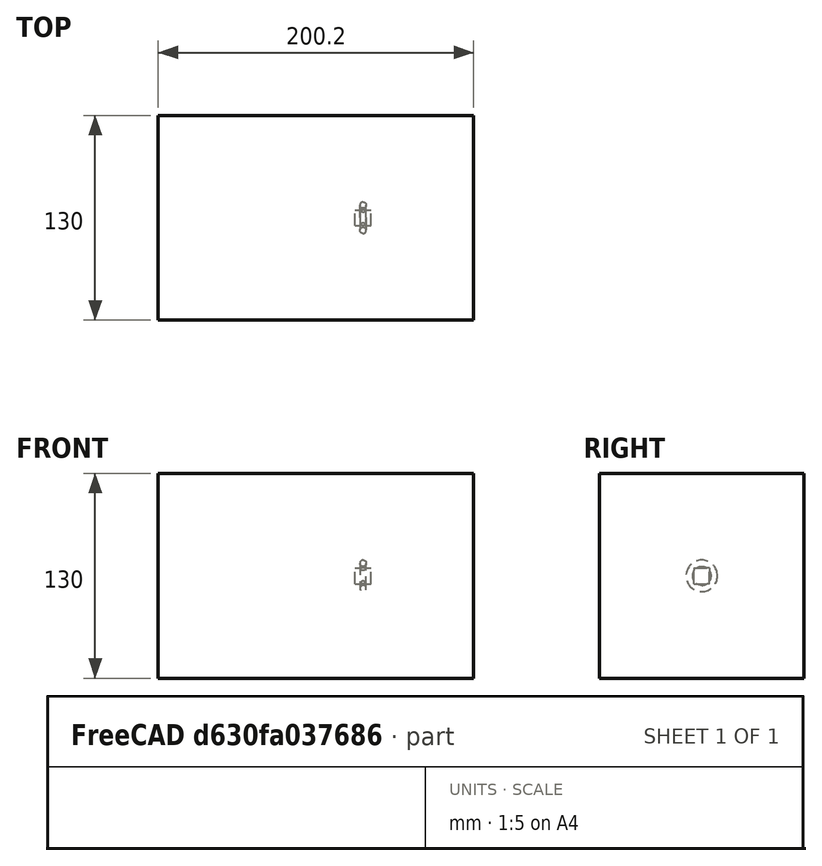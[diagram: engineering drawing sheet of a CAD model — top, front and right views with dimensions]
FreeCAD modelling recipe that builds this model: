
FCSTD DOCUMENT  (FreeCAD 1.0R39109 (Git))
Label: polarArray-7-array-rotated-translated
License: All rights reserved
objects: App::DocumentObjectGroupPython×1251, Part::FeaturePython×4, App::Part×2, Part::MultiFuse×1
note: 4 computed .brp shape members not serialized (recipe doc carries the construction recipe); baked Part::Feature solids carry a one-line shape summary decoded from their .brp

FEATURE [App::DocumentObjectGroupPython] HALFPI  # scripted group (container) (typed FeaturePython)
  name = HALFPI
  value = pi/2.
FEATURE [App::DocumentObjectGroupPython] PI  # scripted group (container) (typed FeaturePython)
  name = PI
  value = 1.*pi
FEATURE [App::DocumentObjectGroupPython] TWOPI  # scripted group (container) (typed FeaturePython)
  name = TWOPI
  value = 2.*pi
FEATURE [App::DocumentObjectGroupPython] Constants  # scripted group (container) (typed FeaturePython)
  Group = -> [HALFPI,PI,TWOPI]
FEATURE [App::DocumentObjectGroupPython] Variables  # scripted group (container) (typed FeaturePython)
FEATURE [App::DocumentObjectGroupPython] Quantities  # scripted group (container) (typed FeaturePython)
FEATURE [App::DocumentObjectGroupPython] Isotopes  # scripted group (container) (typed FeaturePython)
FEATURE [App::DocumentObjectGroupPython] Elements  # scripted group (container) (typed FeaturePython)
FEATURE [App::DocumentObjectGroupPython] Matrix  # scripted group (container) (typed FeaturePython)
FEATURE [App::DocumentObjectGroupPython] Surfaces  # scripted group (container) (typed FeaturePython)
FEATURE [App::DocumentObjectGroupPython] Opticals  # scripted group (container) (typed FeaturePython)
  Group = -> [Matrix,Surfaces]
FEATURE [App::DocumentObjectGroupPython] G4Isotopes  # scripted group (container) (typed FeaturePython)
FEATURE [App::DocumentObjectGroupPython] H_element  # scripted group (container) (typed FeaturePython)
  Z = 1
  atom_value = 1.008
  formula = H
  name = H_element
FEATURE [App::DocumentObjectGroupPython] He_element  # scripted group (container) (typed FeaturePython)
  Z = 2
  atom_value = 4.0026
  formula = He
  name = He_element
FEATURE [App::DocumentObjectGroupPython] Li_element  # scripted group (container) (typed FeaturePython)
  Z = 3
  atom_value = 6.94
  formula = Li
  name = Li_element
FEATURE [App::DocumentObjectGroupPython] Be_element  # scripted group (container) (typed FeaturePython)
  Z = 4
  atom_value = 9.01218
  formula = Be
  name = Be_element
FEATURE [App::DocumentObjectGroupPython] B_element  # scripted group (container) (typed FeaturePython)
  Z = 5
  atom_value = 10.81
  formula = B
  name = B_element
FEATURE [App::DocumentObjectGroupPython] C_element  # scripted group (container) (typed FeaturePython)
  Z = 6
  atom_value = 12.011
  formula = C
  name = C_element
FEATURE [App::DocumentObjectGroupPython] N_element  # scripted group (container) (typed FeaturePython)
  Z = 7
  atom_value = 14.007
  formula = N
  name = N_element
FEATURE [App::DocumentObjectGroupPython] O_element  # scripted group (container) (typed FeaturePython)
  Z = 8
  atom_value = 15.999
  formula = O
  name = O_element
FEATURE [App::DocumentObjectGroupPython] F_element  # scripted group (container) (typed FeaturePython)
  Z = 9
  atom_value = 18.9984
  formula = F
  name = F_element
FEATURE [App::DocumentObjectGroupPython] Ne_element  # scripted group (container) (typed FeaturePython)
  Z = 10
  atom_value = 20.1797
  formula = Ne
  name = Ne_element
FEATURE [App::DocumentObjectGroupPython] Na_element  # scripted group (container) (typed FeaturePython)
  Z = 11
  atom_value = 22.9898
  formula = Na
  name = Na_element
FEATURE [App::DocumentObjectGroupPython] Mg_element  # scripted group (container) (typed FeaturePython)
  Z = 12
  atom_value = 24.305
  formula = Mg
  name = Mg_element
FEATURE [App::DocumentObjectGroupPython] Al_element  # scripted group (container) (typed FeaturePython)
  Z = 13
  atom_value = 26.9815
  formula = Al
  name = Al_element
FEATURE [App::DocumentObjectGroupPython] Si_element  # scripted group (container) (typed FeaturePython)
  Z = 14
  atom_value = 28.085
  formula = Si
  name = Si_element
FEATURE [App::DocumentObjectGroupPython] P_element  # scripted group (container) (typed FeaturePython)
  Z = 15
  atom_value = 30.9738
  formula = P
  name = P_element
FEATURE [App::DocumentObjectGroupPython] S_element  # scripted group (container) (typed FeaturePython)
  Z = 16
  atom_value = 32.06
  formula = S
  name = S_element
FEATURE [App::DocumentObjectGroupPython] Cl_element  # scripted group (container) (typed FeaturePython)
  Z = 17
  atom_value = 35.45
  formula = Cl
  name = Cl_element
FEATURE [App::DocumentObjectGroupPython] Ar_element  # scripted group (container) (typed FeaturePython)
  Z = 18
  atom_value = 39.95
  formula = Ar
  name = Ar_element
FEATURE [App::DocumentObjectGroupPython] K_element  # scripted group (container) (typed FeaturePython)
  Z = 19
  atom_value = 39.0983
  formula = K
  name = K_element
FEATURE [App::DocumentObjectGroupPython] Ca_element  # scripted group (container) (typed FeaturePython)
  Z = 20
  atom_value = 40.078
  formula = Ca
  name = Ca_element
FEATURE [App::DocumentObjectGroupPython] Sc_element  # scripted group (container) (typed FeaturePython)
  Z = 21
  atom_value = 44.9559
  formula = Sc
  name = Sc_element
FEATURE [App::DocumentObjectGroupPython] Ti_element  # scripted group (container) (typed FeaturePython)
  Z = 22
  atom_value = 47.867
  formula = Ti
  name = Ti_element
FEATURE [App::DocumentObjectGroupPython] V_element  # scripted group (container) (typed FeaturePython)
  Z = 23
  atom_value = 50.9415
  formula = V
  name = V_element
FEATURE [App::DocumentObjectGroupPython] Cr_element  # scripted group (container) (typed FeaturePython)
  Z = 24
  atom_value = 51.9961
  formula = Cr
  name = Cr_element
FEATURE [App::DocumentObjectGroupPython] Mn_element  # scripted group (container) (typed FeaturePython)
  Z = 25
  atom_value = 54.938
  formula = Mn
  name = Mn_element
FEATURE [App::DocumentObjectGroupPython] Fe_element  # scripted group (container) (typed FeaturePython)
  Z = 26
  atom_value = 55.845
  formula = Fe
  name = Fe_element
FEATURE [App::DocumentObjectGroupPython] Co_element  # scripted group (container) (typed FeaturePython)
  Z = 27
  atom_value = 58.9332
  formula = Co
  name = Co_element
FEATURE [App::DocumentObjectGroupPython] Ni_element  # scripted group (container) (typed FeaturePython)
  Z = 28
  atom_value = 58.6934
  formula = Ni
  name = Ni_element
FEATURE [App::DocumentObjectGroupPython] Cu_element  # scripted group (container) (typed FeaturePython)
  Z = 29
  atom_value = 63.546
  formula = Cu
  name = Cu_element
FEATURE [App::DocumentObjectGroupPython] Zn_element  # scripted group (container) (typed FeaturePython)
  Z = 30
  atom_value = 65.38
  formula = Zn
  name = Zn_element
FEATURE [App::DocumentObjectGroupPython] Ga_element  # scripted group (container) (typed FeaturePython)
  Z = 31
  atom_value = 69.723
  formula = Ga
  name = Ga_element
FEATURE [App::DocumentObjectGroupPython] Ge_element  # scripted group (container) (typed FeaturePython)
  Z = 32
  atom_value = 72.63
  formula = Ge
  name = Ge_element
FEATURE [App::DocumentObjectGroupPython] As_element  # scripted group (container) (typed FeaturePython)
  Z = 33
  atom_value = 74.9216
  formula = As
  name = As_element
FEATURE [App::DocumentObjectGroupPython] Se_element  # scripted group (container) (typed FeaturePython)
  Z = 34
  atom_value = 78.971
  formula = Se
  name = Se_element
FEATURE [App::DocumentObjectGroupPython] Br_element  # scripted group (container) (typed FeaturePython)
  Z = 35
  atom_value = 79.904
  formula = Br
  name = Br_element
FEATURE [App::DocumentObjectGroupPython] Kr_element  # scripted group (container) (typed FeaturePython)
  Z = 36
  atom_value = 83.798
  formula = Kr
  name = Kr_element
FEATURE [App::DocumentObjectGroupPython] Rb_element  # scripted group (container) (typed FeaturePython)
  Z = 37
  atom_value = 85.4678
  formula = Rb
  name = Rb_element
FEATURE [App::DocumentObjectGroupPython] Sr_element  # scripted group (container) (typed FeaturePython)
  Z = 38
  atom_value = 87.62
  formula = Sr
  name = Sr_element
FEATURE [App::DocumentObjectGroupPython] Y_element  # scripted group (container) (typed FeaturePython)
  Z = 39
  atom_value = 88.9058
  formula = Y
  name = Y_element
FEATURE [App::DocumentObjectGroupPython] Zr_element  # scripted group (container) (typed FeaturePython)
  Z = 40
  atom_value = 91.224
  formula = Zr
  name = Zr_element
FEATURE [App::DocumentObjectGroupPython] Nb_element  # scripted group (container) (typed FeaturePython)
  Z = 41
  atom_value = 92.9064
  formula = Nb
  name = Nb_element
FEATURE [App::DocumentObjectGroupPython] Mo_element  # scripted group (container) (typed FeaturePython)
  Z = 42
  atom_value = 95.95
  formula = Mo
  name = Mo_element
FEATURE [App::DocumentObjectGroupPython] Tc_element  # scripted group (container) (typed FeaturePython)
  Z = 43
  atom_value = 97
  formula = Tc
  name = Tc_element
FEATURE [App::DocumentObjectGroupPython] Ru_element  # scripted group (container) (typed FeaturePython)
  Z = 44
  atom_value = 101.07
  formula = Ru
  name = Ru_element
FEATURE [App::DocumentObjectGroupPython] Rh_element  # scripted group (container) (typed FeaturePython)
  Z = 45
  atom_value = 102.905
  formula = Rh
  name = Rh_element
FEATURE [App::DocumentObjectGroupPython] Pd_element  # scripted group (container) (typed FeaturePython)
  Z = 46
  atom_value = 106.42
  formula = Pd
  name = Pd_element
FEATURE [App::DocumentObjectGroupPython] Ag_element  # scripted group (container) (typed FeaturePython)
  Z = 47
  atom_value = 107.868
  formula = Ag
  name = Ag_element
FEATURE [App::DocumentObjectGroupPython] Cd_element  # scripted group (container) (typed FeaturePython)
  Z = 48
  atom_value = 112.414
  formula = Cd
  name = Cd_element
FEATURE [App::DocumentObjectGroupPython] In_element  # scripted group (container) (typed FeaturePython)
  Z = 49
  atom_value = 114.818
  formula = In
  name = In_element
FEATURE [App::DocumentObjectGroupPython] Sn_element  # scripted group (container) (typed FeaturePython)
  Z = 50
  atom_value = 118.71
  formula = Sn
  name = Sn_element
FEATURE [App::DocumentObjectGroupPython] Sb_element  # scripted group (container) (typed FeaturePython)
  Z = 51
  atom_value = 121.76
  formula = Sb
  name = Sb_element
FEATURE [App::DocumentObjectGroupPython] Te_element  # scripted group (container) (typed FeaturePython)
  Z = 52
  atom_value = 127.6
  formula = Te
  name = Te_element
FEATURE [App::DocumentObjectGroupPython] I_element  # scripted group (container) (typed FeaturePython)
  Z = 53
  atom_value = 126.904
  formula = I
  name = I_element
FEATURE [App::DocumentObjectGroupPython] Xe_element  # scripted group (container) (typed FeaturePython)
  Z = 54
  atom_value = 131.293
  formula = Xe
  name = Xe_element
FEATURE [App::DocumentObjectGroupPython] Cs_element  # scripted group (container) (typed FeaturePython)
  Z = 55
  atom_value = 132.905
  formula = Cs
  name = Cs_element
FEATURE [App::DocumentObjectGroupPython] Ba_element  # scripted group (container) (typed FeaturePython)
  Z = 56
  atom_value = 137.327
  formula = Ba
  name = Ba_element
FEATURE [App::DocumentObjectGroupPython] La_element  # scripted group (container) (typed FeaturePython)
  Z = 57
  atom_value = 138.905
  formula = La
  name = La_element
FEATURE [App::DocumentObjectGroupPython] Ce_element  # scripted group (container) (typed FeaturePython)
  Z = 58
  atom_value = 140.116
  formula = Ce
  name = Ce_element
FEATURE [App::DocumentObjectGroupPython] Pr_element  # scripted group (container) (typed FeaturePython)
  Z = 59
  atom_value = 140.908
  formula = Pr
  name = Pr_element
FEATURE [App::DocumentObjectGroupPython] Nd_element  # scripted group (container) (typed FeaturePython)
  Z = 60
  atom_value = 144.242
  formula = Nd
  name = Nd_element
FEATURE [App::DocumentObjectGroupPython] Pm_element  # scripted group (container) (typed FeaturePython)
  Z = 61
  atom_value = 145
  formula = Pm
  name = Pm_element
FEATURE [App::DocumentObjectGroupPython] Sm_element  # scripted group (container) (typed FeaturePython)
  Z = 62
  atom_value = 150.36
  formula = Sm
  name = Sm_element
FEATURE [App::DocumentObjectGroupPython] Eu_element  # scripted group (container) (typed FeaturePython)
  Z = 63
  atom_value = 151.964
  formula = Eu
  name = Eu_element
FEATURE [App::DocumentObjectGroupPython] Gd_element  # scripted group (container) (typed FeaturePython)
  Z = 64
  atom_value = 157.25
  formula = Gd
  name = Gd_element
FEATURE [App::DocumentObjectGroupPython] Tb_element  # scripted group (container) (typed FeaturePython)
  Z = 65
  atom_value = 158.925
  formula = Tb
  name = Tb_element
FEATURE [App::DocumentObjectGroupPython] Dy_element  # scripted group (container) (typed FeaturePython)
  Z = 66
  atom_value = 162.5
  formula = Dy
  name = Dy_element
FEATURE [App::DocumentObjectGroupPython] Ho_element  # scripted group (container) (typed FeaturePython)
  Z = 67
  atom_value = 164.93
  formula = Ho
  name = Ho_element
FEATURE [App::DocumentObjectGroupPython] Er_element  # scripted group (container) (typed FeaturePython)
  Z = 68
  atom_value = 167.259
  formula = Er
  name = Er_element
FEATURE [App::DocumentObjectGroupPython] Tm_element  # scripted group (container) (typed FeaturePython)
  Z = 69
  atom_value = 168.934
  formula = Tm
  name = Tm_element
FEATURE [App::DocumentObjectGroupPython] Yb_element  # scripted group (container) (typed FeaturePython)
  Z = 70
  atom_value = 173.045
  formula = Yb
  name = Yb_element
FEATURE [App::DocumentObjectGroupPython] Lu_element  # scripted group (container) (typed FeaturePython)
  Z = 71
  atom_value = 174.967
  formula = Lu
  name = Lu_element
FEATURE [App::DocumentObjectGroupPython] Hf_element  # scripted group (container) (typed FeaturePython)
  Z = 72
  atom_value = 178.49
  formula = Hf
  name = Hf_element
FEATURE [App::DocumentObjectGroupPython] Ta_element  # scripted group (container) (typed FeaturePython)
  Z = 73
  atom_value = 180.948
  formula = Ta
  name = Ta_element
FEATURE [App::DocumentObjectGroupPython] W_element  # scripted group (container) (typed FeaturePython)
  Z = 74
  atom_value = 183.84
  formula = W
  name = W_element
FEATURE [App::DocumentObjectGroupPython] Re_element  # scripted group (container) (typed FeaturePython)
  Z = 75
  atom_value = 186.207
  formula = Re
  name = Re_element
FEATURE [App::DocumentObjectGroupPython] Os_element  # scripted group (container) (typed FeaturePython)
  Z = 76
  atom_value = 190.23
  formula = Os
  name = Os_element
FEATURE [App::DocumentObjectGroupPython] Ir_element  # scripted group (container) (typed FeaturePython)
  Z = 77
  atom_value = 192.217
  formula = Ir
  name = Ir_element
FEATURE [App::DocumentObjectGroupPython] Pt_element  # scripted group (container) (typed FeaturePython)
  Z = 78
  atom_value = 195.084
  formula = Pt
  name = Pt_element
FEATURE [App::DocumentObjectGroupPython] Au_element  # scripted group (container) (typed FeaturePython)
  Z = 79
  atom_value = 196.967
  formula = Au
  name = Au_element
FEATURE [App::DocumentObjectGroupPython] Hg_element  # scripted group (container) (typed FeaturePython)
  Z = 80
  atom_value = 200.592
  formula = Hg
  name = Hg_element
FEATURE [App::DocumentObjectGroupPython] Tl_element  # scripted group (container) (typed FeaturePython)
  Z = 81
  atom_value = 204.38
  formula = Tl
  name = Tl_element
FEATURE [App::DocumentObjectGroupPython] Pb_element  # scripted group (container) (typed FeaturePython)
  Z = 82
  atom_value = 207.2
  formula = Pb
  name = Pb_element
FEATURE [App::DocumentObjectGroupPython] Bi_element  # scripted group (container) (typed FeaturePython)
  Z = 83
  atom_value = 208.98
  formula = Bi
  name = Bi_element
FEATURE [App::DocumentObjectGroupPython] Po_element  # scripted group (container) (typed FeaturePython)
  Z = 84
  atom_value = 209
  formula = Po
  name = Po_element
FEATURE [App::DocumentObjectGroupPython] At_element  # scripted group (container) (typed FeaturePython)
  Z = 85
  atom_value = 210
  formula = At
  name = At_element
FEATURE [App::DocumentObjectGroupPython] Rn_element  # scripted group (container) (typed FeaturePython)
  Z = 86
  atom_value = 222
  formula = Rn
  name = Rn_element
FEATURE [App::DocumentObjectGroupPython] Fr_element  # scripted group (container) (typed FeaturePython)
  Z = 87
  atom_value = 223
  formula = Fr
  name = Fr_element
FEATURE [App::DocumentObjectGroupPython] Ra_element  # scripted group (container) (typed FeaturePython)
  Z = 88
  atom_value = 226
  formula = Ra
  name = Ra_element
FEATURE [App::DocumentObjectGroupPython] Ac_element  # scripted group (container) (typed FeaturePython)
  Z = 89
  atom_value = 227
  formula = Ac
  name = Ac_element
FEATURE [App::DocumentObjectGroupPython] Th_element  # scripted group (container) (typed FeaturePython)
  Z = 90
  atom_value = 232.038
  formula = Th
  name = Th_element
FEATURE [App::DocumentObjectGroupPython] Pa_element  # scripted group (container) (typed FeaturePython)
  Z = 91
  atom_value = 231.036
  formula = Pa
  name = Pa_element
FEATURE [App::DocumentObjectGroupPython] U_element  # scripted group (container) (typed FeaturePython)
  Z = 92
  atom_value = 238.029
  formula = U
  name = U_element
FEATURE [App::DocumentObjectGroupPython] Np_element  # scripted group (container) (typed FeaturePython)
  Z = 93
  atom_value = 237
  formula = Np
  name = Np_element
FEATURE [App::DocumentObjectGroupPython] Pu_element  # scripted group (container) (typed FeaturePython)
  Z = 94
  atom_value = 244
  formula = Pu
  name = Pu_element
FEATURE [App::DocumentObjectGroupPython] Am_element  # scripted group (container) (typed FeaturePython)
  Z = 95
  atom_value = 243
  formula = Am
  name = Am_element
FEATURE [App::DocumentObjectGroupPython] Cm_element  # scripted group (container) (typed FeaturePython)
  Z = 96
  atom_value = 247
  formula = Cm
  name = Cm_element
FEATURE [App::DocumentObjectGroupPython] Bk_element  # scripted group (container) (typed FeaturePython)
  Z = 97
  atom_value = 247
  formula = Bk
  name = Bk_element
FEATURE [App::DocumentObjectGroupPython] Cf_element  # scripted group (container) (typed FeaturePython)
  Z = 98
  atom_value = 251
  formula = Cf
  name = Cf_element
FEATURE [App::DocumentObjectGroupPython] G4Elements  # scripted group (container) (typed FeaturePython)
  Group = -> [H_element,He_element,Li_element,Be_element,B_element,C_element,N_element,O_element,F_element,Ne_element,Na_element,Mg_element,Al_element,Si_element,P_element,S_element,Cl_element,Ar_element,K_element,Ca_element,Sc_element,Ti_element,V_element,Cr_element,Mn_element,Fe_element,Co_element,Ni_element,Cu_element,Zn_element,Ga_element,Ge_element,As_element,Se_element,Br_element,Kr_element,Rb_element,+61 more]
FEATURE [App::DocumentObjectGroupPython] H_element001  label="H_element : 0.101"  # scripted group (container) (typed FeaturePython)
  n = 0.101327
FEATURE [App::DocumentObjectGroupPython] C_element001  label="C_element : 0.775"  # scripted group (container) (typed FeaturePython)
  n = 0.7755
FEATURE [App::DocumentObjectGroupPython] N_element001  label="N_element : 0.035"  # scripted group (container) (typed FeaturePython)
  n = 0.035057
FEATURE [App::DocumentObjectGroupPython] O_element001  label="O_element : 0.052"  # scripted group (container) (typed FeaturePython)
  n = 0.0523159
FEATURE [App::DocumentObjectGroupPython] F_element001  label="F_element : 0.017"  # scripted group (container) (typed FeaturePython)
  n = 0.017422
FEATURE [App::DocumentObjectGroupPython] Ca_element001  label="Ca_element : 0.018"  # scripted group (container) (typed FeaturePython)
  n = 0.018378
FEATURE [App::DocumentObjectGroupPython] G4_A_150_TISSUE  label="G4_A-150_TISSUE"  # scripted group (container) (typed FeaturePython)
  Dunit = g/cm3
  Dvalue = 1.127
  Group = -> [H_element001,C_element001,N_element001,O_element001,F_element001,Ca_element001]
  conduct = 2
  density = 1
  expand = 3
  formula = G4_A-150_TISSUE
  name = G4_A-150_TISSUE
  specific = 4
FEATURE [App::DocumentObjectGroupPython] C_element002  label="C_element : 3"  # scripted group (container) (typed FeaturePython)
  n = 3
  ref = C_element
FEATURE [App::DocumentObjectGroupPython] H_element002  label="H_element : 6"  # scripted group (container) (typed FeaturePython)
  n = 6
  ref = H_element
FEATURE [App::DocumentObjectGroupPython] O_element002  label="O_element : 1"  # scripted group (container) (typed FeaturePython)
  n = 1
  ref = O_element
FEATURE [App::DocumentObjectGroupPython] G4_ACETONE  # scripted group (container) (typed FeaturePython)
  Dunit = g/cm3
  Dvalue = 0.7899
  Group = -> [C_element002,H_element002,O_element002]
  conduct = 2
  density = 1
  expand = 3
  formula = G4_ACETONE
  name = G4_ACETONE
  specific = 4
FEATURE [App::DocumentObjectGroupPython] C_element003  label="C_element : 2"  # scripted group (container) (typed FeaturePython)
  n = 2
  ref = C_element
FEATURE [App::DocumentObjectGroupPython] H_element003  label="H_element : 2"  # scripted group (container) (typed FeaturePython)
  n = 2
  ref = H_element
FEATURE [App::DocumentObjectGroupPython] G4_ACETYLENE  # scripted group (container) (typed FeaturePython)
  Dunit = g/cm3
  Dvalue = 0.0010967
  Group = -> [C_element003,H_element003]
  conduct = 2
  density = 1
  expand = 3
  formula = G4_ACETYLENE
  name = G4_ACETYLENE
  specific = 4
FEATURE [App::DocumentObjectGroupPython] C_element004  label="C_element : 5"  # scripted group (container) (typed FeaturePython)
  n = 5
  ref = C_element
FEATURE [App::DocumentObjectGroupPython] H_element004  label="H_element : 5"  # scripted group (container) (typed FeaturePython)
  n = 5
  ref = H_element
FEATURE [App::DocumentObjectGroupPython] N_element002  label="N_element : 5"  # scripted group (container) (typed FeaturePython)
  n = 5
  ref = N_element
FEATURE [App::DocumentObjectGroupPython] G4_ADENINE  # scripted group (container) (typed FeaturePython)
  Dunit = g/cm3
  Dvalue = 1.6
  Group = -> [C_element004,H_element004,N_element002]
  conduct = 2
  density = 1
  expand = 3
  formula = G4_ADENINE
  name = G4_ADENINE
  specific = 4
FEATURE [App::DocumentObjectGroupPython] H_element005  label="H_element : 0.114"  # scripted group (container) (typed FeaturePython)
  n = 0.114
FEATURE [App::DocumentObjectGroupPython] C_element005  label="C_element : 0.598"  # scripted group (container) (typed FeaturePython)
  n = 0.598
FEATURE [App::DocumentObjectGroupPython] N_element003  label="N_element : 0.007"  # scripted group (container) (typed FeaturePython)
  n = 0.007
FEATURE [App::DocumentObjectGroupPython] O_element003  label="O_element : 0.278"  # scripted group (container) (typed FeaturePython)
  n = 0.278
FEATURE [App::DocumentObjectGroupPython] Na_element001  label="Na_element : 0.001"  # scripted group (container) (typed FeaturePython)
  n = 0.001
FEATURE [App::DocumentObjectGroupPython] S_element001  label="S_element : 0.001"  # scripted group (container) (typed FeaturePython)
  n = 0.001
FEATURE [App::DocumentObjectGroupPython] Cl_element001  label="Cl_element : 0.001"  # scripted group (container) (typed FeaturePython)
  n = 0.001
FEATURE [App::DocumentObjectGroupPython] G4_ADIPOSE_TISSUE_ICRP  # scripted group (container) (typed FeaturePython)
  Dunit = g/cm3
  Dvalue = 0.95
  Group = -> [H_element005,C_element005,N_element003,O_element003,Na_element001,S_element001,Cl_element001]
  conduct = 2
  density = 1
  expand = 3
  formula = G4_ADIPOSE_TISSUE_ICRP
  name = G4_ADIPOSE_TISSUE_ICRP
  specific = 4
FEATURE [App::DocumentObjectGroupPython] C_element006  label="C_element : 0.000"  # scripted group (container) (typed FeaturePython)
  n = 0.000124
FEATURE [App::DocumentObjectGroupPython] N_element004  label="N_element : 0.755"  # scripted group (container) (typed FeaturePython)
  n = 0.755268
FEATURE [App::DocumentObjectGroupPython] O_element004  label="O_element : 0.232"  # scripted group (container) (typed FeaturePython)
  n = 0.231781
FEATURE [App::DocumentObjectGroupPython] Ar_element001  label="Ar_element : 0.013"  # scripted group (container) (typed FeaturePython)
  n = 0.012827
FEATURE [App::DocumentObjectGroupPython] G4_AIR  # scripted group (container) (typed FeaturePython)
  Dunit = g/cm3
  Dvalue = 0.00120479
  Group = -> [C_element006,N_element004,O_element004,Ar_element001]
  conduct = 2
  density = 1
  expand = 3
  formula = G4_AIR
  name = G4_AIR
  specific = 4
FEATURE [App::DocumentObjectGroupPython] C_element007  label="C_element : 006"  # scripted group (container) (typed FeaturePython)
  n = 3
  ref = C_element
FEATURE [App::DocumentObjectGroupPython] H_element006  label="H_element : 7"  # scripted group (container) (typed FeaturePython)
  n = 7
  ref = H_element
FEATURE [App::DocumentObjectGroupPython] N_element005  label="N_element : 1"  # scripted group (container) (typed FeaturePython)
  n = 1
  ref = N_element
FEATURE [App::DocumentObjectGroupPython] O_element005  label="O_element : 2"  # scripted group (container) (typed FeaturePython)
  n = 2
  ref = O_element
FEATURE [App::DocumentObjectGroupPython] G4_ALANINE  # scripted group (container) (typed FeaturePython)
  Dunit = g/cm3
  Dvalue = 1.42
  Group = -> [C_element007,H_element006,N_element005,O_element005]
  conduct = 2
  density = 1
  expand = 3
  formula = G4_ALANINE
  name = G4_ALANINE
  specific = 4
FEATURE [App::DocumentObjectGroupPython] Al_element001  label="Al_element : 2"  # scripted group (container) (typed FeaturePython)
  n = 2
  ref = Al_element
FEATURE [App::DocumentObjectGroupPython] O_element006  label="O_element : 3"  # scripted group (container) (typed FeaturePython)
  n = 3
  ref = O_element
FEATURE [App::DocumentObjectGroupPython] G4_ALUMINUM_OXIDE  # scripted group (container) (typed FeaturePython)
  Dunit = g/cm3
  Dvalue = 3.97
  Group = -> [Al_element001,O_element006]
  conduct = 2
  density = 1
  expand = 3
  formula = G4_ALUMINUM_OXIDE
  name = G4_ALUMINUM_OXIDE
  specific = 4
FEATURE [App::DocumentObjectGroupPython] H_element007  label="H_element : 0.106"  # scripted group (container) (typed FeaturePython)
  n = 0.10593
FEATURE [App::DocumentObjectGroupPython] C_element008  label="C_element : 0.789"  # scripted group (container) (typed FeaturePython)
  n = 0.788974
FEATURE [App::DocumentObjectGroupPython] O_element007  label="O_element : 0.105"  # scripted group (container) (typed FeaturePython)
  n = 0.105096
FEATURE [App::DocumentObjectGroupPython] G4_AMBER  # scripted group (container) (typed FeaturePython)
  Dunit = g/cm3
  Dvalue = 1.1
  Group = -> [H_element007,C_element008,O_element007]
  conduct = 2
  density = 1
  expand = 3
  formula = G4_AMBER
  name = G4_AMBER
  specific = 4
FEATURE [App::DocumentObjectGroupPython] N_element006  label="N_element : 006"  # scripted group (container) (typed FeaturePython)
  n = 1
  ref = N_element
FEATURE [App::DocumentObjectGroupPython] H_element008  label="H_element : 3"  # scripted group (container) (typed FeaturePython)
  n = 3
  ref = H_element
FEATURE [App::DocumentObjectGroupPython] G4_AMMONIA  # scripted group (container) (typed FeaturePython)
  Dunit = g/cm3
  Dvalue = 0.000826019
  Group = -> [N_element006,H_element008]
  conduct = 2
  density = 1
  expand = 3
  formula = G4_AMMONIA
  name = G4_AMMONIA
  specific = 4
FEATURE [App::DocumentObjectGroupPython] C_element009  label="C_element : 6"  # scripted group (container) (typed FeaturePython)
  n = 6
  ref = C_element
FEATURE [App::DocumentObjectGroupPython] H_element009  label="H_element : 008"  # scripted group (container) (typed FeaturePython)
  n = 7
  ref = H_element
FEATURE [App::DocumentObjectGroupPython] N_element007  label="N_element : 007"  # scripted group (container) (typed FeaturePython)
  n = 1
  ref = N_element
FEATURE [App::DocumentObjectGroupPython] G4_ANILINE  # scripted group (container) (typed FeaturePython)
  Dunit = g/cm3
  Dvalue = 1.0235
  Group = -> [C_element009,H_element009,N_element007]
  conduct = 2
  density = 1
  expand = 3
  formula = G4_ANILINE
  name = G4_ANILINE
  specific = 4
FEATURE [App::DocumentObjectGroupPython] C_element010  label="C_element : 14"  # scripted group (container) (typed FeaturePython)
  n = 14
  ref = C_element
FEATURE [App::DocumentObjectGroupPython] H_element010  label="H_element : 10"  # scripted group (container) (typed FeaturePython)
  n = 10
  ref = H_element
FEATURE [App::DocumentObjectGroupPython] G4_ANTHRACENE  # scripted group (container) (typed FeaturePython)
  Dunit = g/cm3
  Dvalue = 1.283
  Group = -> [C_element010,H_element010]
  conduct = 2
  density = 1
  expand = 3
  formula = G4_ANTHRACENE
  name = G4_ANTHRACENE
  specific = 4
FEATURE [App::DocumentObjectGroupPython] H_element011  label="H_element : 0.065"  # scripted group (container) (typed FeaturePython)
  n = 0.0654709
FEATURE [App::DocumentObjectGroupPython] C_element011  label="C_element : 0.537"  # scripted group (container) (typed FeaturePython)
  n = 0.536944
FEATURE [App::DocumentObjectGroupPython] N_element008  label="N_element : 0.021"  # scripted group (container) (typed FeaturePython)
  n = 0.0215
FEATURE [App::DocumentObjectGroupPython] O_element008  label="O_element : 0.032"  # scripted group (container) (typed FeaturePython)
  n = 0.032085
FEATURE [App::DocumentObjectGroupPython] F_element002  label="F_element : 0.167"  # scripted group (container) (typed FeaturePython)
  n = 0.167411
FEATURE [App::DocumentObjectGroupPython] Ca_element002  label="Ca_element : 0.177"  # scripted group (container) (typed FeaturePython)
  n = 0.176589
FEATURE [App::DocumentObjectGroupPython] G4_B_100_BONE  label="G4_B-100_BONE"  # scripted group (container) (typed FeaturePython)
  Dunit = g/cm3
  Dvalue = 1.45
  Group = -> [H_element011,C_element011,N_element008,O_element008,F_element002,Ca_element002]
  conduct = 2
  density = 1
  expand = 3
  formula = G4_B-100_BONE
  name = G4_B-100_BONE
  specific = 4
FEATURE [App::DocumentObjectGroupPython] H_element012  label="H_element : 0.057"  # scripted group (container) (typed FeaturePython)
  n = 0.057441
FEATURE [App::DocumentObjectGroupPython] C_element012  label="C_element : 0.790"  # scripted group (container) (typed FeaturePython)
  n = 0.774591
FEATURE [App::DocumentObjectGroupPython] O_element009  label="O_element : 0.168"  # scripted group (container) (typed FeaturePython)
  n = 0.167968
FEATURE [App::DocumentObjectGroupPython] G4_BAKELITE  # scripted group (container) (typed FeaturePython)
  Dunit = g/cm3
  Dvalue = 1.25
  Group = -> [H_element012,C_element012,O_element009]
  conduct = 2
  density = 1
  expand = 3
  formula = G4_BAKELITE
  name = G4_BAKELITE
  specific = 4
FEATURE [App::DocumentObjectGroupPython] Ba_element001  label="Ba_element : 1"  # scripted group (container) (typed FeaturePython)
  n = 1
  ref = Ba_element
FEATURE [App::DocumentObjectGroupPython] F_element003  label="F_element : 2"  # scripted group (container) (typed FeaturePython)
  n = 2
  ref = F_element
FEATURE [App::DocumentObjectGroupPython] G4_BARIUM_FLUORIDE  # scripted group (container) (typed FeaturePython)
  Dunit = g/cm3
  Dvalue = 4.89
  Group = -> [Ba_element001,F_element003]
  conduct = 2
  density = 1
  expand = 3
  formula = G4_BARIUM_FLUORIDE
  name = G4_BARIUM_FLUORIDE
  specific = 4
FEATURE [App::DocumentObjectGroupPython] Ba_element002  label="Ba_element : 002"  # scripted group (container) (typed FeaturePython)
  n = 1
  ref = Ba_element
FEATURE [App::DocumentObjectGroupPython] S_element002  label="S_element : 1"  # scripted group (container) (typed FeaturePython)
  n = 1
  ref = S_element
FEATURE [App::DocumentObjectGroupPython] O_element010  label="O_element : 4"  # scripted group (container) (typed FeaturePython)
  n = 4
  ref = O_element
FEATURE [App::DocumentObjectGroupPython] G4_BARIUM_SULFATE  # scripted group (container) (typed FeaturePython)
  Dunit = g/cm3
  Dvalue = 4.5
  Group = -> [Ba_element002,S_element002,O_element010]
  conduct = 2
  density = 1
  expand = 3
  formula = G4_BARIUM_SULFATE
  name = G4_BARIUM_SULFATE
  specific = 4
FEATURE [App::DocumentObjectGroupPython] C_element013  label="C_element : 007"  # scripted group (container) (typed FeaturePython)
  n = 6
  ref = C_element
FEATURE [App::DocumentObjectGroupPython] H_element013  label="H_element : 009"  # scripted group (container) (typed FeaturePython)
  n = 6
  ref = H_element
FEATURE [App::DocumentObjectGroupPython] G4_BENZENE  # scripted group (container) (typed FeaturePython)
  Dunit = g/cm3
  Dvalue = 0.87865
  Group = -> [C_element013,H_element013]
  conduct = 2
  density = 1
  expand = 3
  formula = G4_BENZENE
  name = G4_BENZENE
  specific = 4
FEATURE [App::DocumentObjectGroupPython] Be_element001  label="Be_element : 1"  # scripted group (container) (typed FeaturePython)
  n = 1
  ref = Be_element
FEATURE [App::DocumentObjectGroupPython] O_element011  label="O_element : 005"  # scripted group (container) (typed FeaturePython)
  n = 1
  ref = O_element
FEATURE [App::DocumentObjectGroupPython] G4_BERYLLIUM_OXIDE  # scripted group (container) (typed FeaturePython)
  Dunit = g/cm3
  Dvalue = 3.01
  Group = -> [Be_element001,O_element011]
  conduct = 2
  density = 1
  expand = 3
  formula = G4_BERYLLIUM_OXIDE
  name = G4_BERYLLIUM_OXIDE
  specific = 4
FEATURE [App::DocumentObjectGroupPython] Bi_element001  label="Bi_element : 4"  # scripted group (container) (typed FeaturePython)
  n = 4
  ref = Bi_element
FEATURE [App::DocumentObjectGroupPython] Ge_element001  label="Ge_element : 3"  # scripted group (container) (typed FeaturePython)
  n = 3
  ref = Ge_element
FEATURE [App::DocumentObjectGroupPython] O_element012  label="O_element : 12"  # scripted group (container) (typed FeaturePython)
  n = 12
  ref = O_element
FEATURE [App::DocumentObjectGroupPython] G4_BGO  # scripted group (container) (typed FeaturePython)
  Dunit = g/cm3
  Dvalue = 7.13
  Group = -> [Bi_element001,Ge_element001,O_element012]
  conduct = 2
  density = 1
  expand = 3
  formula = G4_BGO
  name = G4_BGO
  specific = 4
FEATURE [App::DocumentObjectGroupPython] H_element014  label="H_element : 0.102"  # scripted group (container) (typed FeaturePython)
  n = 0.102
FEATURE [App::DocumentObjectGroupPython] C_element014  label="C_element : 0.110"  # scripted group (container) (typed FeaturePython)
  n = 0.11
FEATURE [App::DocumentObjectGroupPython] N_element009  label="N_element : 0.033"  # scripted group (container) (typed FeaturePython)
  n = 0.033
FEATURE [App::DocumentObjectGroupPython] O_element013  label="O_element : 0.745"  # scripted group (container) (typed FeaturePython)
  n = 0.745
FEATURE [App::DocumentObjectGroupPython] Na_element002  label="Na_element : 0.002"  # scripted group (container) (typed FeaturePython)
  n = 0.001
FEATURE [App::DocumentObjectGroupPython] P_element001  label="P_element : 0.001"  # scripted group (container) (typed FeaturePython)
  n = 0.001
FEATURE [App::DocumentObjectGroupPython] S_element003  label="S_element : 0.002"  # scripted group (container) (typed FeaturePython)
  n = 0.002
FEATURE [App::DocumentObjectGroupPython] Cl_element002  label="Cl_element : 0.003"  # scripted group (container) (typed FeaturePython)
  n = 0.003
FEATURE [App::DocumentObjectGroupPython] K_element001  label="K_element : 0.002"  # scripted group (container) (typed FeaturePython)
  n = 0.002
FEATURE [App::DocumentObjectGroupPython] Fe_element001  label="Fe_element : 0.001"  # scripted group (container) (typed FeaturePython)
  n = 0.001
FEATURE [App::DocumentObjectGroupPython] G4_BLOOD_ICRP  # scripted group (container) (typed FeaturePython)
  Dunit = g/cm3
  Dvalue = 1.06
  Group = -> [H_element014,C_element014,N_element009,O_element013,Na_element002,P_element001,S_element003,Cl_element002,K_element001,Fe_element001]
  conduct = 2
  density = 1
  expand = 3
  formula = G4_BLOOD_ICRP
  name = G4_BLOOD_ICRP
  specific = 4
FEATURE [App::DocumentObjectGroupPython] H_element015  label="H_element : 0.064"  # scripted group (container) (typed FeaturePython)
  n = 0.064
FEATURE [App::DocumentObjectGroupPython] C_element015  label="C_element : 0.278"  # scripted group (container) (typed FeaturePython)
  n = 0.278
FEATURE [App::DocumentObjectGroupPython] N_element010  label="N_element : 0.027"  # scripted group (container) (typed FeaturePython)
  n = 0.027
FEATURE [App::DocumentObjectGroupPython] O_element014  label="O_element : 0.410"  # scripted group (container) (typed FeaturePython)
  n = 0.41
FEATURE [App::DocumentObjectGroupPython] Mg_element001  label="Mg_element : 0.002"  # scripted group (container) (typed FeaturePython)
  n = 0.002
FEATURE [App::DocumentObjectGroupPython] P_element002  label="P_element : 0.070"  # scripted group (container) (typed FeaturePython)
  n = 0.07
FEATURE [App::DocumentObjectGroupPython] S_element004  label="S_element : 0.003"  # scripted group (container) (typed FeaturePython)
  n = 0.002
FEATURE [App::DocumentObjectGroupPython] Ca_element003  label="Ca_element : 0.147"  # scripted group (container) (typed FeaturePython)
  n = 0.147
FEATURE [App::DocumentObjectGroupPython] G4_BONE_COMPACT_ICRU  # scripted group (container) (typed FeaturePython)
  Dunit = g/cm3
  Dvalue = 1.85
  Group = -> [H_element015,C_element015,N_element010,O_element014,Mg_element001,P_element002,S_element004,Ca_element003]
  conduct = 2
  density = 1
  expand = 3
  formula = G4_BONE_COMPACT_ICRU
  name = G4_BONE_COMPACT_ICRU
  specific = 4
FEATURE [App::DocumentObjectGroupPython] H_element016  label="H_element : 0.034"  # scripted group (container) (typed FeaturePython)
  n = 0.034
FEATURE [App::DocumentObjectGroupPython] C_element016  label="C_element : 0.155"  # scripted group (container) (typed FeaturePython)
  n = 0.155
FEATURE [App::DocumentObjectGroupPython] N_element011  label="N_element : 0.042"  # scripted group (container) (typed FeaturePython)
  n = 0.042
FEATURE [App::DocumentObjectGroupPython] O_element015  label="O_element : 0.435"  # scripted group (container) (typed FeaturePython)
  n = 0.435
FEATURE [App::DocumentObjectGroupPython] Na_element003  label="Na_element : 0.003"  # scripted group (container) (typed FeaturePython)
  n = 0.001
FEATURE [App::DocumentObjectGroupPython] Mg_element002  label="Mg_element : 0.003"  # scripted group (container) (typed FeaturePython)
  n = 0.002
FEATURE [App::DocumentObjectGroupPython] P_element003  label="P_element : 0.103"  # scripted group (container) (typed FeaturePython)
  n = 0.103
FEATURE [App::DocumentObjectGroupPython] S_element005  label="S_element : 0.004"  # scripted group (container) (typed FeaturePython)
  n = 0.003
FEATURE [App::DocumentObjectGroupPython] Ca_element004  label="Ca_element : 0.225"  # scripted group (container) (typed FeaturePython)
  n = 0.225
FEATURE [App::DocumentObjectGroupPython] G4_BONE_CORTICAL_ICRP  # scripted group (container) (typed FeaturePython)
  Dunit = g/cm3
  Dvalue = 1.92
  Group = -> [H_element016,C_element016,N_element011,O_element015,Na_element003,Mg_element002,P_element003,S_element005,Ca_element004]
  conduct = 2
  density = 1
  expand = 3
  formula = G4_BONE_CORTICAL_ICRP
  name = G4_BONE_CORTICAL_ICRP
  specific = 4
FEATURE [App::DocumentObjectGroupPython] B_element001  label="B_element : 4"  # scripted group (container) (typed FeaturePython)
  n = 4
  ref = B_element
FEATURE [App::DocumentObjectGroupPython] C_element017  label="C_element : 1"  # scripted group (container) (typed FeaturePython)
  n = 1
  ref = C_element
FEATURE [App::DocumentObjectGroupPython] G4_BORON_CARBIDE  # scripted group (container) (typed FeaturePython)
  Dunit = g/cm3
  Dvalue = 2.52
  Group = -> [B_element001,C_element017]
  conduct = 2
  density = 1
  expand = 3
  formula = G4_BORON_CARBIDE
  name = G4_BORON_CARBIDE
  specific = 4
FEATURE [App::DocumentObjectGroupPython] B_element002  label="B_element : 2"  # scripted group (container) (typed FeaturePython)
  n = 2
  ref = B_element
FEATURE [App::DocumentObjectGroupPython] O_element016  label="O_element : 006"  # scripted group (container) (typed FeaturePython)
  n = 3
  ref = O_element
FEATURE [App::DocumentObjectGroupPython] G4_BORON_OXIDE  # scripted group (container) (typed FeaturePython)
  Dunit = g/cm3
  Dvalue = 1.812
  Group = -> [B_element002,O_element016]
  conduct = 2
  density = 1
  expand = 3
  formula = G4_BORON_OXIDE
  name = G4_BORON_OXIDE
  specific = 4
FEATURE [App::DocumentObjectGroupPython] H_element017  label="H_element : 0.107"  # scripted group (container) (typed FeaturePython)
  n = 0.107
FEATURE [App::DocumentObjectGroupPython] C_element018  label="C_element : 0.145"  # scripted group (container) (typed FeaturePython)
  n = 0.145
FEATURE [App::DocumentObjectGroupPython] N_element012  label="N_element : 0.022"  # scripted group (container) (typed FeaturePython)
  n = 0.022
FEATURE [App::DocumentObjectGroupPython] O_element017  label="O_element : 0.712"  # scripted group (container) (typed FeaturePython)
  n = 0.712
FEATURE [App::DocumentObjectGroupPython] Na_element004  label="Na_element : 0.004"  # scripted group (container) (typed FeaturePython)
  n = 0.002
FEATURE [App::DocumentObjectGroupPython] P_element004  label="P_element : 0.004"  # scripted group (container) (typed FeaturePython)
  n = 0.004
FEATURE [App::DocumentObjectGroupPython] S_element006  label="S_element : 0.005"  # scripted group (container) (typed FeaturePython)
  n = 0.002
FEATURE [App::DocumentObjectGroupPython] Cl_element003  label="Cl_element : 0.004"  # scripted group (container) (typed FeaturePython)
  n = 0.003
FEATURE [App::DocumentObjectGroupPython] K_element002  label="K_element : 0.003"  # scripted group (container) (typed FeaturePython)
  n = 0.003
FEATURE [App::DocumentObjectGroupPython] G4_BRAIN_ICRP  # scripted group (container) (typed FeaturePython)
  Dunit = g/cm3
  Dvalue = 1.04
  Group = -> [H_element017,C_element018,N_element012,O_element017,Na_element004,P_element004,S_element006,Cl_element003,K_element002]
  conduct = 2
  density = 1
  expand = 3
  formula = G4_BRAIN_ICRP
  name = G4_BRAIN_ICRP
  specific = 4
FEATURE [App::DocumentObjectGroupPython] C_element019  label="C_element : 4"  # scripted group (container) (typed FeaturePython)
  n = 4
  ref = C_element
FEATURE [App::DocumentObjectGroupPython] H_element018  label="H_element : 010"  # scripted group (container) (typed FeaturePython)
  n = 10
  ref = H_element
FEATURE [App::DocumentObjectGroupPython] G4_BUTANE  # scripted group (container) (typed FeaturePython)
  Dunit = g/cm3
  Dvalue = 0.00249343
  Group = -> [C_element019,H_element018]
  conduct = 2
  density = 1
  expand = 3
  formula = G4_BUTANE
  name = G4_BUTANE
  specific = 4
FEATURE [App::DocumentObjectGroupPython] C_element020  label="C_element : 008"  # scripted group (container) (typed FeaturePython)
  n = 4
  ref = C_element
FEATURE [App::DocumentObjectGroupPython] H_element019  label="H_element : 011"  # scripted group (container) (typed FeaturePython)
  n = 10
  ref = H_element
FEATURE [App::DocumentObjectGroupPython] O_element018  label="O_element : 007"  # scripted group (container) (typed FeaturePython)
  n = 1
  ref = O_element
FEATURE [App::DocumentObjectGroupPython] G4_N_BUTYL_ALCOHOL  label="G4_N-BUTYL_ALCOHOL"  # scripted group (container) (typed FeaturePython)
  Dunit = g/cm3
  Dvalue = 0.8098
  Group = -> [C_element020,H_element019,O_element018]
  conduct = 2
  density = 1
  expand = 3
  formula = G4_N-BUTYL_ALCOHOL
  name = G4_N-BUTYL_ALCOHOL
  specific = 4
FEATURE [App::DocumentObjectGroupPython] H_element020  label="H_element : 0.025"  # scripted group (container) (typed FeaturePython)
  n = 0.02468
FEATURE [App::DocumentObjectGroupPython] C_element021  label="C_element : 0.502"  # scripted group (container) (typed FeaturePython)
  n = 0.501611
FEATURE [App::DocumentObjectGroupPython] O_element019  label="O_element : 0.005"  # scripted group (container) (typed FeaturePython)
  n = 0.004527
FEATURE [App::DocumentObjectGroupPython] F_element004  label="F_element : 0.465"  # scripted group (container) (typed FeaturePython)
  n = 0.465209
FEATURE [App::DocumentObjectGroupPython] Si_element001  label="Si_element : 0.004"  # scripted group (container) (typed FeaturePython)
  n = 0.003973
FEATURE [App::DocumentObjectGroupPython] G4_C_552  label="G4_C-552"  # scripted group (container) (typed FeaturePython)
  Dunit = g/cm3
  Dvalue = 1.76
  Group = -> [H_element020,C_element021,O_element019,F_element004,Si_element001]
  conduct = 2
  density = 1
  expand = 3
  formula = G4_C-552
  name = G4_C-552
  specific = 4
FEATURE [App::DocumentObjectGroupPython] Cd_element001  label="Cd_element : 1"  # scripted group (container) (typed FeaturePython)
  n = 1
  ref = Cd_element
FEATURE [App::DocumentObjectGroupPython] Te_element001  label="Te_element : 1"  # scripted group (container) (typed FeaturePython)
  n = 1
  ref = Te_element
FEATURE [App::DocumentObjectGroupPython] G4_CADMIUM_TELLURIDE  # scripted group (container) (typed FeaturePython)
  Dunit = g/cm3
  Dvalue = 6.2
  Group = -> [Cd_element001,Te_element001]
  conduct = 2
  density = 1
  expand = 3
  formula = G4_CADMIUM_TELLURIDE
  name = G4_CADMIUM_TELLURIDE
  specific = 4
FEATURE [App::DocumentObjectGroupPython] Cd_element002  label="Cd_element : 002"  # scripted group (container) (typed FeaturePython)
  n = 1
  ref = Cd_element
FEATURE [App::DocumentObjectGroupPython] W_element001  label="W_element : 1"  # scripted group (container) (typed FeaturePython)
  n = 1
  ref = W_element
FEATURE [App::DocumentObjectGroupPython] O_element020  label="O_element : 008"  # scripted group (container) (typed FeaturePython)
  n = 4
  ref = O_element
FEATURE [App::DocumentObjectGroupPython] G4_CADMIUM_TUNGSTATE  # scripted group (container) (typed FeaturePython)
  Dunit = g/cm3
  Dvalue = 7.9
  Group = -> [Cd_element002,W_element001,O_element020]
  conduct = 2
  density = 1
  expand = 3
  formula = G4_CADMIUM_TUNGSTATE
  name = G4_CADMIUM_TUNGSTATE
  specific = 4
FEATURE [App::DocumentObjectGroupPython] Ca_element005  label="Ca_element : 1"  # scripted group (container) (typed FeaturePython)
  n = 1
  ref = Ca_element
FEATURE [App::DocumentObjectGroupPython] C_element022  label="C_element : 009"  # scripted group (container) (typed FeaturePython)
  n = 1
  ref = C_element
FEATURE [App::DocumentObjectGroupPython] O_element021  label="O_element : 009"  # scripted group (container) (typed FeaturePython)
  n = 3
  ref = O_element
FEATURE [App::DocumentObjectGroupPython] G4_CALCIUM_CARBONATE  # scripted group (container) (typed FeaturePython)
  Dunit = g/cm3
  Dvalue = 2.8
  Group = -> [Ca_element005,C_element022,O_element021]
  conduct = 2
  density = 1
  expand = 3
  formula = G4_CALCIUM_CARBONATE
  name = G4_CALCIUM_CARBONATE
  specific = 4
FEATURE [App::DocumentObjectGroupPython] Ca_element006  label="Ca_element : 002"  # scripted group (container) (typed FeaturePython)
  n = 1
  ref = Ca_element
FEATURE [App::DocumentObjectGroupPython] F_element005  label="F_element : 003"  # scripted group (container) (typed FeaturePython)
  n = 2
  ref = F_element
FEATURE [App::DocumentObjectGroupPython] G4_CALCIUM_FLUORIDE  # scripted group (container) (typed FeaturePython)
  Dunit = g/cm3
  Dvalue = 3.18
  Group = -> [Ca_element006,F_element005]
  conduct = 2
  density = 1
  expand = 3
  formula = G4_CALCIUM_FLUORIDE
  name = G4_CALCIUM_FLUORIDE
  specific = 4
FEATURE [App::DocumentObjectGroupPython] Ca_element007  label="Ca_element : 003"  # scripted group (container) (typed FeaturePython)
  n = 1
  ref = Ca_element
FEATURE [App::DocumentObjectGroupPython] O_element022  label="O_element : 010"  # scripted group (container) (typed FeaturePython)
  n = 1
  ref = O_element
FEATURE [App::DocumentObjectGroupPython] G4_CALCIUM_OXIDE  # scripted group (container) (typed FeaturePython)
  Dunit = g/cm3
  Dvalue = 3.3
  Group = -> [Ca_element007,O_element022]
  conduct = 2
  density = 1
  expand = 3
  formula = G4_CALCIUM_OXIDE
  name = G4_CALCIUM_OXIDE
  specific = 4
FEATURE [App::DocumentObjectGroupPython] Ca_element008  label="Ca_element : 004"  # scripted group (container) (typed FeaturePython)
  n = 1
  ref = Ca_element
FEATURE [App::DocumentObjectGroupPython] S_element007  label="S_element : 002"  # scripted group (container) (typed FeaturePython)
  n = 1
  ref = S_element
FEATURE [App::DocumentObjectGroupPython] O_element023  label="O_element : 011"  # scripted group (container) (typed FeaturePython)
  n = 4
  ref = O_element
FEATURE [App::DocumentObjectGroupPython] G4_CALCIUM_SULFATE  # scripted group (container) (typed FeaturePython)
  Dunit = g/cm3
  Dvalue = 2.96
  Group = -> [Ca_element008,S_element007,O_element023]
  conduct = 2
  density = 1
  expand = 3
  formula = G4_CALCIUM_SULFATE
  name = G4_CALCIUM_SULFATE
  specific = 4
FEATURE [App::DocumentObjectGroupPython] Ca_element009  label="Ca_element : 005"  # scripted group (container) (typed FeaturePython)
  n = 1
  ref = Ca_element
FEATURE [App::DocumentObjectGroupPython] W_element002  label="W_element : 002"  # scripted group (container) (typed FeaturePython)
  n = 1
  ref = W_element
FEATURE [App::DocumentObjectGroupPython] O_element024  label="O_element : 012"  # scripted group (container) (typed FeaturePython)
  n = 4
  ref = O_element
FEATURE [App::DocumentObjectGroupPython] G4_CALCIUM_TUNGSTATE  # scripted group (container) (typed FeaturePython)
  Dunit = g/cm3
  Dvalue = 6.062
  Group = -> [Ca_element009,W_element002,O_element024]
  conduct = 2
  density = 1
  expand = 3
  formula = G4_CALCIUM_TUNGSTATE
  name = G4_CALCIUM_TUNGSTATE
  specific = 4
FEATURE [App::DocumentObjectGroupPython] C_element023  label="C_element : 010"  # scripted group (container) (typed FeaturePython)
  n = 1
  ref = C_element
FEATURE [App::DocumentObjectGroupPython] O_element025  label="O_element : 013"  # scripted group (container) (typed FeaturePython)
  n = 2
  ref = O_element
FEATURE [App::DocumentObjectGroupPython] G4_CARBON_DIOXIDE  # scripted group (container) (typed FeaturePython)
  Dunit = g/cm3
  Dvalue = 0.00184212
  Group = -> [C_element023,O_element025]
  conduct = 2
  density = 1
  expand = 3
  formula = G4_CARBON_DIOXIDE
  name = G4_CARBON_DIOXIDE
  specific = 4
FEATURE [App::DocumentObjectGroupPython] C_element024  label="C_element : 011"  # scripted group (container) (typed FeaturePython)
  n = 1
  ref = C_element
FEATURE [App::DocumentObjectGroupPython] Cl_element004  label="Cl_element : 4"  # scripted group (container) (typed FeaturePython)
  n = 4
  ref = Cl_element
FEATURE [App::DocumentObjectGroupPython] G4_CARBON_TETRACHLORIDE  # scripted group (container) (typed FeaturePython)
  Dunit = g/cm3
  Dvalue = 1.594
  Group = -> [C_element024,Cl_element004]
  conduct = 2
  density = 1
  expand = 3
  formula = G4_CARBON_TETRACHLORIDE
  name = G4_CARBON_TETRACHLORIDE
  specific = 4
FEATURE [App::DocumentObjectGroupPython] C_element025  label="C_element : 012"  # scripted group (container) (typed FeaturePython)
  n = 6
  ref = C_element
FEATURE [App::DocumentObjectGroupPython] H_element021  label="H_element : 012"  # scripted group (container) (typed FeaturePython)
  n = 10
  ref = H_element
FEATURE [App::DocumentObjectGroupPython] O_element026  label="O_element : 5"  # scripted group (container) (typed FeaturePython)
  n = 5
  ref = O_element
FEATURE [App::DocumentObjectGroupPython] G4_CELLULOSE_CELLOPHANE  # scripted group (container) (typed FeaturePython)
  Dunit = g/cm3
  Dvalue = 1.42
  Group = -> [C_element025,H_element021,O_element026]
  conduct = 2
  density = 1
  expand = 3
  formula = G4_CELLULOSE_CELLOPHANE
  name = G4_CELLULOSE_CELLOPHANE
  specific = 4
FEATURE [App::DocumentObjectGroupPython] H_element022  label="H_element : 0.067"  # scripted group (container) (typed FeaturePython)
  n = 0.067125
FEATURE [App::DocumentObjectGroupPython] C_element026  label="C_element : 0.545"  # scripted group (container) (typed FeaturePython)
  n = 0.545403
FEATURE [App::DocumentObjectGroupPython] O_element027  label="O_element : 0.387"  # scripted group (container) (typed FeaturePython)
  n = 0.387472
FEATURE [App::DocumentObjectGroupPython] G4_CELLULOSE_BUTYRATE  # scripted group (container) (typed FeaturePython)
  Dunit = g/cm3
  Dvalue = 1.2
  Group = -> [H_element022,C_element026,O_element027]
  conduct = 2
  density = 1
  expand = 3
  formula = G4_CELLULOSE_BUTYRATE
  name = G4_CELLULOSE_BUTYRATE
  specific = 4
FEATURE [App::DocumentObjectGroupPython] H_element023  label="H_element : 0.029"  # scripted group (container) (typed FeaturePython)
  n = 0.029216
FEATURE [App::DocumentObjectGroupPython] C_element027  label="C_element : 0.271"  # scripted group (container) (typed FeaturePython)
  n = 0.271296
FEATURE [App::DocumentObjectGroupPython] N_element013  label="N_element : 0.121"  # scripted group (container) (typed FeaturePython)
  n = 0.121276
FEATURE [App::DocumentObjectGroupPython] O_element028  label="O_element : 0.578"  # scripted group (container) (typed FeaturePython)
  n = 0.578212
FEATURE [App::DocumentObjectGroupPython] G4_CELLULOSE_NITRATE  # scripted group (container) (typed FeaturePython)
  Dunit = g/cm3
  Dvalue = 1.49
  Group = -> [H_element023,C_element027,N_element013,O_element028]
  conduct = 2
  density = 1
  expand = 3
  formula = G4_CELLULOSE_NITRATE
  name = G4_CELLULOSE_NITRATE
  specific = 4
FEATURE [App::DocumentObjectGroupPython] H_element024  label="H_element : 0.108"  # scripted group (container) (typed FeaturePython)
  n = 0.107596
FEATURE [App::DocumentObjectGroupPython] N_element014  label="N_element : 0.001"  # scripted group (container) (typed FeaturePython)
  n = 0.0008
FEATURE [App::DocumentObjectGroupPython] O_element029  label="O_element : 0.875"  # scripted group (container) (typed FeaturePython)
  n = 0.874976
FEATURE [App::DocumentObjectGroupPython] S_element008  label="S_element : 0.015"  # scripted group (container) (typed FeaturePython)
  n = 0.014627
FEATURE [App::DocumentObjectGroupPython] Ce_element001  label="Ce_element : 0.002"  # scripted group (container) (typed FeaturePython)
  n = 0.002001
FEATURE [App::DocumentObjectGroupPython] G4_CERIC_SULFATE  # scripted group (container) (typed FeaturePython)
  Dunit = g/cm3
  Dvalue = 1.03
  Group = -> [H_element024,N_element014,O_element029,S_element008,Ce_element001]
  conduct = 2
  density = 1
  expand = 3
  formula = G4_CERIC_SULFATE
  name = G4_CERIC_SULFATE
  specific = 4
FEATURE [App::DocumentObjectGroupPython] Cs_element001  label="Cs_element : 1"  # scripted group (container) (typed FeaturePython)
  n = 1
  ref = Cs_element
FEATURE [App::DocumentObjectGroupPython] F_element006  label="F_element : 1"  # scripted group (container) (typed FeaturePython)
  n = 1
  ref = F_element
FEATURE [App::DocumentObjectGroupPython] G4_CESIUM_FLUORIDE  # scripted group (container) (typed FeaturePython)
  Dunit = g/cm3
  Dvalue = 4.115
  Group = -> [Cs_element001,F_element006]
  conduct = 2
  density = 1
  expand = 3
  formula = G4_CESIUM_FLUORIDE
  name = G4_CESIUM_FLUORIDE
  specific = 4
FEATURE [App::DocumentObjectGroupPython] Cs_element002  label="Cs_element : 002"  # scripted group (container) (typed FeaturePython)
  n = 1
  ref = Cs_element
FEATURE [App::DocumentObjectGroupPython] I_element001  label="I_element : 1"  # scripted group (container) (typed FeaturePython)
  n = 1
  ref = I_element
FEATURE [App::DocumentObjectGroupPython] G4_CESIUM_IODIDE  # scripted group (container) (typed FeaturePython)
  Dunit = g/cm3
  Dvalue = 4.51
  Group = -> [Cs_element002,I_element001]
  conduct = 2
  density = 1
  expand = 3
  formula = G4_CESIUM_IODIDE
  name = G4_CESIUM_IODIDE
  specific = 4
FEATURE [App::DocumentObjectGroupPython] C_element028  label="C_element : 013"  # scripted group (container) (typed FeaturePython)
  n = 6
  ref = C_element
FEATURE [App::DocumentObjectGroupPython] H_element025  label="H_element : 013"  # scripted group (container) (typed FeaturePython)
  n = 5
  ref = H_element
FEATURE [App::DocumentObjectGroupPython] Cl_element005  label="Cl_element : 1"  # scripted group (container) (typed FeaturePython)
  n = 1
  ref = Cl_element
FEATURE [App::DocumentObjectGroupPython] G4_CHLOROBENZENE  # scripted group (container) (typed FeaturePython)
  Dunit = g/cm3
  Dvalue = 1.1058
  Group = -> [C_element028,H_element025,Cl_element005]
  conduct = 2
  density = 1
  expand = 3
  formula = G4_CHLOROBENZENE
  name = G4_CHLOROBENZENE
  specific = 4
FEATURE [App::DocumentObjectGroupPython] C_element029  label="C_element : 014"  # scripted group (container) (typed FeaturePython)
  n = 1
  ref = C_element
FEATURE [App::DocumentObjectGroupPython] H_element026  label="H_element : 1"  # scripted group (container) (typed FeaturePython)
  n = 1
  ref = H_element
FEATURE [App::DocumentObjectGroupPython] Cl_element006  label="Cl_element : 3"  # scripted group (container) (typed FeaturePython)
  n = 3
  ref = Cl_element
FEATURE [App::DocumentObjectGroupPython] G4_CHLOROFORM  # scripted group (container) (typed FeaturePython)
  Dunit = g/cm3
  Dvalue = 1.4832
  Group = -> [C_element029,H_element026,Cl_element006]
  conduct = 2
  density = 1
  expand = 3
  formula = G4_CHLOROFORM
  name = G4_CHLOROFORM
  specific = 4
FEATURE [App::DocumentObjectGroupPython] H_element027  label="H_element : 0.010"  # scripted group (container) (typed FeaturePython)
  n = 0.01
FEATURE [App::DocumentObjectGroupPython] C_element030  label="C_element : 0.001"  # scripted group (container) (typed FeaturePython)
  n = 0.001
FEATURE [App::DocumentObjectGroupPython] O_element030  label="O_element : 0.529"  # scripted group (container) (typed FeaturePython)
  n = 0.529107
FEATURE [App::DocumentObjectGroupPython] Na_element005  label="Na_element : 0.016"  # scripted group (container) (typed FeaturePython)
  n = 0.016
FEATURE [App::DocumentObjectGroupPython] Mg_element003  label="Mg_element : 0.004"  # scripted group (container) (typed FeaturePython)
  n = 0.002
FEATURE [App::DocumentObjectGroupPython] Al_element002  label="Al_element : 0.034"  # scripted group (container) (typed FeaturePython)
  n = 0.033872
FEATURE [App::DocumentObjectGroupPython] Si_element002  label="Si_element : 0.337"  # scripted group (container) (typed FeaturePython)
  n = 0.337021
FEATURE [App::DocumentObjectGroupPython] K_element003  label="K_element : 0.013"  # scripted group (container) (typed FeaturePython)
  n = 0.013
FEATURE [App::DocumentObjectGroupPython] Ca_element010  label="Ca_element : 0.044"  # scripted group (container) (typed FeaturePython)
  n = 0.044
FEATURE [App::DocumentObjectGroupPython] Fe_element002  label="Fe_element : 0.014"  # scripted group (container) (typed FeaturePython)
  n = 0.014
FEATURE [App::DocumentObjectGroupPython] G4_CONCRETE  # scripted group (container) (typed FeaturePython)
  Dunit = g/cm3
  Dvalue = 2.3
  Group = -> [H_element027,C_element030,O_element030,Na_element005,Mg_element003,Al_element002,Si_element002,K_element003,Ca_element010,Fe_element002]
  conduct = 2
  density = 1
  expand = 3
  formula = G4_CONCRETE
  name = G4_CONCRETE
  specific = 4
FEATURE [App::DocumentObjectGroupPython] C_element031  label="C_element : 015"  # scripted group (container) (typed FeaturePython)
  n = 6
  ref = C_element
FEATURE [App::DocumentObjectGroupPython] H_element028  label="H_element : 12"  # scripted group (container) (typed FeaturePython)
  n = 12
  ref = H_element
FEATURE [App::DocumentObjectGroupPython] G4_CYCLOHEXANE  # scripted group (container) (typed FeaturePython)
  Dunit = g/cm3
  Dvalue = 0.779
  Group = -> [C_element031,H_element028]
  conduct = 2
  density = 1
  expand = 3
  formula = G4_CYCLOHEXANE
  name = G4_CYCLOHEXANE
  specific = 4
FEATURE [App::DocumentObjectGroupPython] C_element032  label="C_element : 016"  # scripted group (container) (typed FeaturePython)
  n = 6
  ref = C_element
FEATURE [App::DocumentObjectGroupPython] H_element029  label="H_element : 4"  # scripted group (container) (typed FeaturePython)
  n = 4
  ref = H_element
FEATURE [App::DocumentObjectGroupPython] Cl_element007  label="Cl_element : 2"  # scripted group (container) (typed FeaturePython)
  n = 2
  ref = Cl_element
FEATURE [App::DocumentObjectGroupPython] G4_1_2_DICHLOROBENZENE  label="G4_1.2-DICHLOROBENZENE"  # scripted group (container) (typed FeaturePython)
  Dunit = g/cm3
  Dvalue = 1.3048
  Group = -> [C_element032,H_element029,Cl_element007]
  conduct = 2
  density = 1
  expand = 3
  formula = G4_1.2-DICHLOROBENZENE
  name = G4_1.2-DICHLOROBENZENE
  specific = 4
FEATURE [App::DocumentObjectGroupPython] C_element033  label="C_element : 017"  # scripted group (container) (typed FeaturePython)
  n = 4
  ref = C_element
FEATURE [App::DocumentObjectGroupPython] H_element030  label="H_element : 8"  # scripted group (container) (typed FeaturePython)
  n = 8
  ref = H_element
FEATURE [App::DocumentObjectGroupPython] O_element031  label="O_element : 014"  # scripted group (container) (typed FeaturePython)
  n = 1
  ref = O_element
FEATURE [App::DocumentObjectGroupPython] Cl_element008  label="Cl_element : 005"  # scripted group (container) (typed FeaturePython)
  n = 2
  ref = Cl_element
FEATURE [App::DocumentObjectGroupPython] G4_DICHLORODIETHYL_ETHER  # scripted group (container) (typed FeaturePython)
  Dunit = g/cm3
  Dvalue = 1.2199
  Group = -> [C_element033,H_element030,O_element031,Cl_element008]
  conduct = 2
  density = 1
  expand = 3
  formula = G4_DICHLORODIETHYL_ETHER
  name = G4_DICHLORODIETHYL_ETHER
  specific = 4
FEATURE [App::DocumentObjectGroupPython] C_element034  label="C_element : 018"  # scripted group (container) (typed FeaturePython)
  n = 2
  ref = C_element
FEATURE [App::DocumentObjectGroupPython] H_element031  label="H_element : 014"  # scripted group (container) (typed FeaturePython)
  n = 4
  ref = H_element
FEATURE [App::DocumentObjectGroupPython] Cl_element009  label="Cl_element : 006"  # scripted group (container) (typed FeaturePython)
  n = 2
  ref = Cl_element
FEATURE [App::DocumentObjectGroupPython] G4_1_2_DICHLOROETHANE  label="G4_1.2-DICHLOROETHANE"  # scripted group (container) (typed FeaturePython)
  Dunit = g/cm3
  Dvalue = 1.2351
  Group = -> [C_element034,H_element031,Cl_element009]
  conduct = 2
  density = 1
  expand = 3
  formula = G4_1.2-DICHLOROETHANE
  name = G4_1.2-DICHLOROETHANE
  specific = 4
FEATURE [App::DocumentObjectGroupPython] C_element035  label="C_element : 019"  # scripted group (container) (typed FeaturePython)
  n = 4
  ref = C_element
FEATURE [App::DocumentObjectGroupPython] H_element032  label="H_element : 015"  # scripted group (container) (typed FeaturePython)
  n = 10
  ref = H_element
FEATURE [App::DocumentObjectGroupPython] O_element032  label="O_element : 015"  # scripted group (container) (typed FeaturePython)
  n = 1
  ref = O_element
FEATURE [App::DocumentObjectGroupPython] G4_DIETHYL_ETHER  # scripted group (container) (typed FeaturePython)
  Dunit = g/cm3
  Dvalue = 0.71378
  Group = -> [C_element035,H_element032,O_element032]
  conduct = 2
  density = 1
  expand = 3
  formula = G4_DIETHYL_ETHER
  name = G4_DIETHYL_ETHER
  specific = 4
FEATURE [App::DocumentObjectGroupPython] C_element036  label="C_element : 020"  # scripted group (container) (typed FeaturePython)
  n = 3
  ref = C_element
FEATURE [App::DocumentObjectGroupPython] H_element033  label="H_element : 016"  # scripted group (container) (typed FeaturePython)
  n = 7
  ref = H_element
FEATURE [App::DocumentObjectGroupPython] N_element015  label="N_element : 008"  # scripted group (container) (typed FeaturePython)
  n = 1
  ref = N_element
FEATURE [App::DocumentObjectGroupPython] O_element033  label="O_element : 016"  # scripted group (container) (typed FeaturePython)
  n = 1
  ref = O_element
FEATURE [App::DocumentObjectGroupPython] G4_N_N_DIMETHYL_FORMAMIDE  label="G4_N.N-DIMETHYL_FORMAMIDE"  # scripted group (container) (typed FeaturePython)
  Dunit = g/cm3
  Dvalue = 0.9487
  Group = -> [C_element036,H_element033,N_element015,O_element033]
  conduct = 2
  density = 1
  expand = 3
  formula = G4_N.N-DIMETHYL_FORMAMIDE
  name = G4_N.N-DIMETHYL_FORMAMIDE
  specific = 4
FEATURE [App::DocumentObjectGroupPython] C_element037  label="C_element : 021"  # scripted group (container) (typed FeaturePython)
  n = 2
  ref = C_element
FEATURE [App::DocumentObjectGroupPython] H_element034  label="H_element : 017"  # scripted group (container) (typed FeaturePython)
  n = 6
  ref = H_element
FEATURE [App::DocumentObjectGroupPython] O_element034  label="O_element : 017"  # scripted group (container) (typed FeaturePython)
  n = 1
  ref = O_element
FEATURE [App::DocumentObjectGroupPython] S_element009  label="S_element : 003"  # scripted group (container) (typed FeaturePython)
  n = 1
  ref = S_element
FEATURE [App::DocumentObjectGroupPython] G4_DIMETHYL_SULFOXIDE  # scripted group (container) (typed FeaturePython)
  Dunit = g/cm3
  Dvalue = 1.1014
  Group = -> [C_element037,H_element034,O_element034,S_element009]
  conduct = 2
  density = 1
  expand = 3
  formula = G4_DIMETHYL_SULFOXIDE
  name = G4_DIMETHYL_SULFOXIDE
  specific = 4
FEATURE [App::DocumentObjectGroupPython] C_element038  label="C_element : 022"  # scripted group (container) (typed FeaturePython)
  n = 2
  ref = C_element
FEATURE [App::DocumentObjectGroupPython] H_element035  label="H_element : 018"  # scripted group (container) (typed FeaturePython)
  n = 6
  ref = H_element
FEATURE [App::DocumentObjectGroupPython] G4_ETHANE  # scripted group (container) (typed FeaturePython)
  Dunit = g/cm3
  Dvalue = 0.00125324
  Group = -> [C_element038,H_element035]
  conduct = 2
  density = 1
  expand = 3
  formula = G4_ETHANE
  name = G4_ETHANE
  specific = 4
FEATURE [App::DocumentObjectGroupPython] C_element039  label="C_element : 023"  # scripted group (container) (typed FeaturePython)
  n = 2
  ref = C_element
FEATURE [App::DocumentObjectGroupPython] H_element036  label="H_element : 019"  # scripted group (container) (typed FeaturePython)
  n = 6
  ref = H_element
FEATURE [App::DocumentObjectGroupPython] O_element035  label="O_element : 018"  # scripted group (container) (typed FeaturePython)
  n = 1
  ref = O_element
FEATURE [App::DocumentObjectGroupPython] G4_ETHYL_ALCOHOL  # scripted group (container) (typed FeaturePython)
  Dunit = g/cm3
  Dvalue = 0.7893
  Group = -> [C_element039,H_element036,O_element035]
  conduct = 2
  density = 1
  expand = 3
  formula = G4_ETHYL_ALCOHOL
  name = G4_ETHYL_ALCOHOL
  specific = 4
FEATURE [App::DocumentObjectGroupPython] H_element037  label="H_element : 0.090"  # scripted group (container) (typed FeaturePython)
  n = 0.090027
FEATURE [App::DocumentObjectGroupPython] C_element040  label="C_element : 0.585"  # scripted group (container) (typed FeaturePython)
  n = 0.585182
FEATURE [App::DocumentObjectGroupPython] O_element036  label="O_element : 0.325"  # scripted group (container) (typed FeaturePython)
  n = 0.324791
FEATURE [App::DocumentObjectGroupPython] G4_ETHYL_CELLULOSE  # scripted group (container) (typed FeaturePython)
  Dunit = g/cm3
  Dvalue = 1.13
  Group = -> [H_element037,C_element040,O_element036]
  conduct = 2
  density = 1
  expand = 3
  formula = G4_ETHYL_CELLULOSE
  name = G4_ETHYL_CELLULOSE
  specific = 4
FEATURE [App::DocumentObjectGroupPython] C_element041  label="C_element : 024"  # scripted group (container) (typed FeaturePython)
  n = 2
  ref = C_element
FEATURE [App::DocumentObjectGroupPython] H_element038  label="H_element : 020"  # scripted group (container) (typed FeaturePython)
  n = 4
  ref = H_element
FEATURE [App::DocumentObjectGroupPython] G4_ETHYLENE  # scripted group (container) (typed FeaturePython)
  Dunit = g/cm3
  Dvalue = 0.00117497
  Group = -> [C_element041,H_element038]
  conduct = 2
  density = 1
  expand = 3
  formula = G4_ETHYLENE
  name = G4_ETHYLENE
  specific = 4
FEATURE [App::DocumentObjectGroupPython] H_element039  label="H_element : 0.096"  # scripted group (container) (typed FeaturePython)
  n = 0.096
FEATURE [App::DocumentObjectGroupPython] C_element042  label="C_element : 0.195"  # scripted group (container) (typed FeaturePython)
  n = 0.195
FEATURE [App::DocumentObjectGroupPython] N_element016  label="N_element : 0.057"  # scripted group (container) (typed FeaturePython)
  n = 0.057
FEATURE [App::DocumentObjectGroupPython] O_element037  label="O_element : 0.646"  # scripted group (container) (typed FeaturePython)
  n = 0.646
FEATURE [App::DocumentObjectGroupPython] Na_element006  label="Na_element : 0.017"  # scripted group (container) (typed FeaturePython)
  n = 0.001
FEATURE [App::DocumentObjectGroupPython] P_element005  label="P_element : 0.104"  # scripted group (container) (typed FeaturePython)
  n = 0.001
FEATURE [App::DocumentObjectGroupPython] S_element010  label="S_element : 0.016"  # scripted group (container) (typed FeaturePython)
  n = 0.003
FEATURE [App::DocumentObjectGroupPython] Cl_element010  label="Cl_element : 0.005"  # scripted group (container) (typed FeaturePython)
  n = 0.001
FEATURE [App::DocumentObjectGroupPython] G4_EYE_LENS_ICRP  # scripted group (container) (typed FeaturePython)
  Dunit = g/cm3
  Dvalue = 1.07
  Group = -> [H_element039,C_element042,N_element016,O_element037,Na_element006,P_element005,S_element010,Cl_element010]
  conduct = 2
  density = 1
  expand = 3
  formula = G4_EYE_LENS_ICRP
  name = G4_EYE_LENS_ICRP
  specific = 4
FEATURE [App::DocumentObjectGroupPython] Fe_element003  label="Fe_element : 2"  # scripted group (container) (typed FeaturePython)
  n = 2
  ref = Fe_element
FEATURE [App::DocumentObjectGroupPython] O_element038  label="O_element : 019"  # scripted group (container) (typed FeaturePython)
  n = 3
  ref = O_element
FEATURE [App::DocumentObjectGroupPython] G4_FERRIC_OXIDE  # scripted group (container) (typed FeaturePython)
  Dunit = g/cm3
  Dvalue = 5.2
  Group = -> [Fe_element003,O_element038]
  conduct = 2
  density = 1
  expand = 3
  formula = G4_FERRIC_OXIDE
  name = G4_FERRIC_OXIDE
  specific = 4
FEATURE [App::DocumentObjectGroupPython] Fe_element004  label="Fe_element : 1"  # scripted group (container) (typed FeaturePython)
  n = 1
  ref = Fe_element
FEATURE [App::DocumentObjectGroupPython] B_element003  label="B_element : 1"  # scripted group (container) (typed FeaturePython)
  n = 1
  ref = B_element
FEATURE [App::DocumentObjectGroupPython] G4_FERROBORIDE  # scripted group (container) (typed FeaturePython)
  Dunit = g/cm3
  Dvalue = 7.15
  Group = -> [Fe_element004,B_element003]
  conduct = 2
  density = 1
  expand = 3
  formula = G4_FERROBORIDE
  name = G4_FERROBORIDE
  specific = 4
FEATURE [App::DocumentObjectGroupPython] Fe_element005  label="Fe_element : 003"  # scripted group (container) (typed FeaturePython)
  n = 1
  ref = Fe_element
FEATURE [App::DocumentObjectGroupPython] O_element039  label="O_element : 020"  # scripted group (container) (typed FeaturePython)
  n = 1
  ref = O_element
FEATURE [App::DocumentObjectGroupPython] G4_FERROUS_OXIDE  # scripted group (container) (typed FeaturePython)
  Dunit = g/cm3
  Dvalue = 5.7
  Group = -> [Fe_element005,O_element039]
  conduct = 2
  density = 1
  expand = 3
  formula = G4_FERROUS_OXIDE
  name = G4_FERROUS_OXIDE
  specific = 4
FEATURE [App::DocumentObjectGroupPython] H_element040  label="H_element : 0.115"  # scripted group (container) (typed FeaturePython)
  n = 0.108259
FEATURE [App::DocumentObjectGroupPython] N_element017  label="N_element : 0.000"  # scripted group (container) (typed FeaturePython)
  n = 2.7e-05
FEATURE [App::DocumentObjectGroupPython] O_element040  label="O_element : 0.879"  # scripted group (container) (typed FeaturePython)
  n = 0.878636
FEATURE [App::DocumentObjectGroupPython] Na_element007  label="Na_element : 0.000"  # scripted group (container) (typed FeaturePython)
  n = 2.2e-05
FEATURE [App::DocumentObjectGroupPython] S_element011  label="S_element : 0.013"  # scripted group (container) (typed FeaturePython)
  n = 0.012968
FEATURE [App::DocumentObjectGroupPython] Cl_element011  label="Cl_element : 0.000"  # scripted group (container) (typed FeaturePython)
  n = 3.4e-05
FEATURE [App::DocumentObjectGroupPython] Fe_element006  label="Fe_element : 0.000"  # scripted group (container) (typed FeaturePython)
  n = 5.4e-05
FEATURE [App::DocumentObjectGroupPython] G4_FERROUS_SULFATE  # scripted group (container) (typed FeaturePython)
  Dunit = g/cm3
  Dvalue = 1.024
  Group = -> [H_element040,N_element017,O_element040,Na_element007,S_element011,Cl_element011,Fe_element006]
  conduct = 2
  density = 1
  expand = 3
  formula = G4_FERROUS_SULFATE
  name = G4_FERROUS_SULFATE
  specific = 4
FEATURE [App::DocumentObjectGroupPython] C_element043  label="C_element : 0.099"  # scripted group (container) (typed FeaturePython)
  n = 0.099335
FEATURE [App::DocumentObjectGroupPython] F_element007  label="F_element : 0.314"  # scripted group (container) (typed FeaturePython)
  n = 0.314247
FEATURE [App::DocumentObjectGroupPython] Cl_element012  label="Cl_element : 0.586"  # scripted group (container) (typed FeaturePython)
  n = 0.586418
FEATURE [App::DocumentObjectGroupPython] G4_FREON_12  label="G4_FREON-12"  # scripted group (container) (typed FeaturePython)
  Dunit = g/cm3
  Dvalue = 1.12
  Group = -> [C_element043,F_element007,Cl_element012]
  conduct = 2
  density = 1
  expand = 3
  formula = G4_FREON-12
  name = G4_FREON-12
  specific = 4
FEATURE [App::DocumentObjectGroupPython] C_element044  label="C_element : 0.057"  # scripted group (container) (typed FeaturePython)
  n = 0.057245
FEATURE [App::DocumentObjectGroupPython] F_element008  label="F_element : 0.181"  # scripted group (container) (typed FeaturePython)
  n = 0.181096
FEATURE [App::DocumentObjectGroupPython] Br_element001  label="Br_element : 0.762"  # scripted group (container) (typed FeaturePython)
  n = 0.761659
FEATURE [App::DocumentObjectGroupPython] G4_FREON_12B2  label="G4_FREON-12B2"  # scripted group (container) (typed FeaturePython)
  Dunit = g/cm3
  Dvalue = 1.8
  Group = -> [C_element044,F_element008,Br_element001]
  conduct = 2
  density = 1
  expand = 3
  formula = G4_FREON-12B2
  name = G4_FREON-12B2
  specific = 4
FEATURE [App::DocumentObjectGroupPython] C_element045  label="C_element : 0.115"  # scripted group (container) (typed FeaturePython)
  n = 0.114983
FEATURE [App::DocumentObjectGroupPython] F_element009  label="F_element : 0.546"  # scripted group (container) (typed FeaturePython)
  n = 0.545621
FEATURE [App::DocumentObjectGroupPython] Cl_element013  label="Cl_element : 0.339"  # scripted group (container) (typed FeaturePython)
  n = 0.339396
FEATURE [App::DocumentObjectGroupPython] G4_FREON_13  label="G4_FREON-13"  # scripted group (container) (typed FeaturePython)
  Dunit = g/cm3
  Dvalue = 0.95
  Group = -> [C_element045,F_element009,Cl_element013]
  conduct = 2
  density = 1
  expand = 3
  formula = G4_FREON-13
  name = G4_FREON-13
  specific = 4
FEATURE [App::DocumentObjectGroupPython] C_element046  label="C_element : 025"  # scripted group (container) (typed FeaturePython)
  n = 1
  ref = C_element
FEATURE [App::DocumentObjectGroupPython] F_element010  label="F_element : 3"  # scripted group (container) (typed FeaturePython)
  n = 3
  ref = F_element
FEATURE [App::DocumentObjectGroupPython] Br_element002  label="Br_element : 1"  # scripted group (container) (typed FeaturePython)
  n = 1
  ref = Br_element
FEATURE [App::DocumentObjectGroupPython] G4_FREON_13B1  label="G4_FREON-13B1"  # scripted group (container) (typed FeaturePython)
  Dunit = g/cm3
  Dvalue = 1.5
  Group = -> [C_element046,F_element010,Br_element002]
  conduct = 2
  density = 1
  expand = 3
  formula = G4_FREON-13B1
  name = G4_FREON-13B1
  specific = 4
FEATURE [App::DocumentObjectGroupPython] C_element047  label="C_element : 0.061"  # scripted group (container) (typed FeaturePython)
  n = 0.061309
FEATURE [App::DocumentObjectGroupPython] F_element011  label="F_element : 0.291"  # scripted group (container) (typed FeaturePython)
  n = 0.290924
FEATURE [App::DocumentObjectGroupPython] I_element002  label="I_element : 0.648"  # scripted group (container) (typed FeaturePython)
  n = 0.647767
FEATURE [App::DocumentObjectGroupPython] G4_FREON_13I1  label="G4_FREON-13I1"  # scripted group (container) (typed FeaturePython)
  Dunit = g/cm3
  Dvalue = 1.8
  Group = -> [C_element047,F_element011,I_element002]
  conduct = 2
  density = 1
  expand = 3
  formula = G4_FREON-13I1
  name = G4_FREON-13I1
  specific = 4
FEATURE [App::DocumentObjectGroupPython] Gd_element001  label="Gd_element : 2"  # scripted group (container) (typed FeaturePython)
  n = 2
  ref = Gd_element
FEATURE [App::DocumentObjectGroupPython] O_element041  label="O_element : 021"  # scripted group (container) (typed FeaturePython)
  n = 2
  ref = O_element
FEATURE [App::DocumentObjectGroupPython] S_element012  label="S_element : 004"  # scripted group (container) (typed FeaturePython)
  n = 1
  ref = S_element
FEATURE [App::DocumentObjectGroupPython] G4_GADOLINIUM_OXYSULFIDE  # scripted group (container) (typed FeaturePython)
  Dunit = g/cm3
  Dvalue = 7.44
  Group = -> [Gd_element001,O_element041,S_element012]
  conduct = 2
  density = 1
  expand = 3
  formula = G4_GADOLINIUM_OXYSULFIDE
  name = G4_GADOLINIUM_OXYSULFIDE
  specific = 4
FEATURE [App::DocumentObjectGroupPython] Ga_element001  label="Ga_element : 1"  # scripted group (container) (typed FeaturePython)
  n = 1
  ref = Ga_element
FEATURE [App::DocumentObjectGroupPython] As_element001  label="As_element : 1"  # scripted group (container) (typed FeaturePython)
  n = 1
  ref = As_element
FEATURE [App::DocumentObjectGroupPython] G4_GALLIUM_ARSENIDE  # scripted group (container) (typed FeaturePython)
  Dunit = g/cm3
  Dvalue = 5.31
  Group = -> [Ga_element001,As_element001]
  conduct = 2
  density = 1
  expand = 3
  formula = G4_GALLIUM_ARSENIDE
  name = G4_GALLIUM_ARSENIDE
  specific = 4
FEATURE [App::DocumentObjectGroupPython] H_element041  label="H_element : 0.081"  # scripted group (container) (typed FeaturePython)
  n = 0.08118
FEATURE [App::DocumentObjectGroupPython] C_element048  label="C_element : 0.416"  # scripted group (container) (typed FeaturePython)
  n = 0.41606
FEATURE [App::DocumentObjectGroupPython] N_element018  label="N_element : 0.111"  # scripted group (container) (typed FeaturePython)
  n = 0.11124
FEATURE [App::DocumentObjectGroupPython] O_element042  label="O_element : 0.381"  # scripted group (container) (typed FeaturePython)
  n = 0.38064
FEATURE [App::DocumentObjectGroupPython] S_element013  label="S_element : 0.011"  # scripted group (container) (typed FeaturePython)
  n = 0.01088
FEATURE [App::DocumentObjectGroupPython] G4_GEL_PHOTO_EMULSION  # scripted group (container) (typed FeaturePython)
  Dunit = g/cm3
  Dvalue = 1.2914
  Group = -> [H_element041,C_element048,N_element018,O_element042,S_element013]
  conduct = 2
  density = 1
  expand = 3
  formula = G4_GEL_PHOTO_EMULSION
  name = G4_GEL_PHOTO_EMULSION
  specific = 4
FEATURE [App::DocumentObjectGroupPython] B_element004  label="B_element : 0.040"  # scripted group (container) (typed FeaturePython)
  n = 0.0400639
FEATURE [App::DocumentObjectGroupPython] O_element043  label="O_element : 0.540"  # scripted group (container) (typed FeaturePython)
  n = 0.539561
FEATURE [App::DocumentObjectGroupPython] Na_element008  label="Na_element : 0.028"  # scripted group (container) (typed FeaturePython)
  n = 0.0281909
FEATURE [App::DocumentObjectGroupPython] Al_element003  label="Al_element : 0.012"  # scripted group (container) (typed FeaturePython)
  n = 0.011644
FEATURE [App::DocumentObjectGroupPython] Si_element003  label="Si_element : 0.377"  # scripted group (container) (typed FeaturePython)
  n = 0.377219
FEATURE [App::DocumentObjectGroupPython] K_element004  label="K_element : 0.014"  # scripted group (container) (typed FeaturePython)
  n = 0.00332099
FEATURE [App::DocumentObjectGroupPython] G4_Pyrex_Glass  # scripted group (container) (typed FeaturePython)
  Dunit = g/cm3
  Dvalue = 2.23
  Group = -> [B_element004,O_element043,Na_element008,Al_element003,Si_element003,K_element004]
  conduct = 2
  density = 1
  expand = 3
  formula = G4_Pyrex_Glass
  name = G4_Pyrex_Glass
  specific = 4
FEATURE [App::DocumentObjectGroupPython] O_element044  label="O_element : 0.156"  # scripted group (container) (typed FeaturePython)
  n = 0.156453
FEATURE [App::DocumentObjectGroupPython] Si_element004  label="Si_element : 0.081"  # scripted group (container) (typed FeaturePython)
  n = 0.080866
FEATURE [App::DocumentObjectGroupPython] Ti_element001  label="Ti_element : 0.008"  # scripted group (container) (typed FeaturePython)
  n = 0.008092
FEATURE [App::DocumentObjectGroupPython] As_element002  label="As_element : 0.003"  # scripted group (container) (typed FeaturePython)
  n = 0.002651
FEATURE [App::DocumentObjectGroupPython] Pb_element001  label="Pb_element : 0.752"  # scripted group (container) (typed FeaturePython)
  n = 0.751938
FEATURE [App::DocumentObjectGroupPython] G4_GLASS_LEAD  # scripted group (container) (typed FeaturePython)
  Dunit = g/cm3
  Dvalue = 6.22
  Group = -> [O_element044,Si_element004,Ti_element001,As_element002,Pb_element001]
  conduct = 2
  density = 1
  expand = 3
  formula = G4_GLASS_LEAD
  name = G4_GLASS_LEAD
  specific = 4
FEATURE [App::DocumentObjectGroupPython] O_element045  label="O_element : 0.460"  # scripted group (container) (typed FeaturePython)
  n = 0.4598
FEATURE [App::DocumentObjectGroupPython] Na_element009  label="Na_element : 0.096"  # scripted group (container) (typed FeaturePython)
  n = 0.0964411
FEATURE [App::DocumentObjectGroupPython] Si_element005  label="Si_element : 0.378"  # scripted group (container) (typed FeaturePython)
  n = 0.336553
FEATURE [App::DocumentObjectGroupPython] Ca_element011  label="Ca_element : 0.107"  # scripted group (container) (typed FeaturePython)
  n = 0.107205
FEATURE [App::DocumentObjectGroupPython] G4_GLASS_PLATE  # scripted group (container) (typed FeaturePython)
  Dunit = g/cm3
  Dvalue = 2.4
  Group = -> [O_element045,Na_element009,Si_element005,Ca_element011]
  conduct = 2
  density = 1
  expand = 3
  formula = G4_GLASS_PLATE
  name = G4_GLASS_PLATE
  specific = 4
FEATURE [App::DocumentObjectGroupPython] C_element049  label="C_element : 026"  # scripted group (container) (typed FeaturePython)
  n = 5
  ref = C_element
FEATURE [App::DocumentObjectGroupPython] H_element042  label="H_element : 021"  # scripted group (container) (typed FeaturePython)
  n = 10
  ref = H_element
FEATURE [App::DocumentObjectGroupPython] N_element019  label="N_element : 2"  # scripted group (container) (typed FeaturePython)
  n = 2
  ref = N_element
FEATURE [App::DocumentObjectGroupPython] O_element046  label="O_element : 022"  # scripted group (container) (typed FeaturePython)
  n = 3
  ref = O_element
FEATURE [App::DocumentObjectGroupPython] G4_GLUTAMINE  # scripted group (container) (typed FeaturePython)
  Dunit = g/cm3
  Dvalue = 1.46
  Group = -> [C_element049,H_element042,N_element019,O_element046]
  conduct = 2
  density = 1
  expand = 3
  formula = G4_GLUTAMINE
  name = G4_GLUTAMINE
  specific = 4
FEATURE [App::DocumentObjectGroupPython] C_element050  label="C_element : 027"  # scripted group (container) (typed FeaturePython)
  n = 3
  ref = C_element
FEATURE [App::DocumentObjectGroupPython] H_element043  label="H_element : 022"  # scripted group (container) (typed FeaturePython)
  n = 8
  ref = H_element
FEATURE [App::DocumentObjectGroupPython] O_element047  label="O_element : 023"  # scripted group (container) (typed FeaturePython)
  n = 3
  ref = O_element
FEATURE [App::DocumentObjectGroupPython] G4_GLYCEROL  # scripted group (container) (typed FeaturePython)
  Dunit = g/cm3
  Dvalue = 1.2613
  Group = -> [C_element050,H_element043,O_element047]
  conduct = 2
  density = 1
  expand = 3
  formula = G4_GLYCEROL
  name = G4_GLYCEROL
  specific = 4
FEATURE [App::DocumentObjectGroupPython] C_element051  label="C_element : 028"  # scripted group (container) (typed FeaturePython)
  n = 5
  ref = C_element
FEATURE [App::DocumentObjectGroupPython] H_element044  label="H_element : 023"  # scripted group (container) (typed FeaturePython)
  n = 5
  ref = H_element
FEATURE [App::DocumentObjectGroupPython] N_element020  label="N_element : 009"  # scripted group (container) (typed FeaturePython)
  n = 5
  ref = N_element
FEATURE [App::DocumentObjectGroupPython] O_element048  label="O_element : 024"  # scripted group (container) (typed FeaturePython)
  n = 1
  ref = O_element
FEATURE [App::DocumentObjectGroupPython] G4_GUANINE  # scripted group (container) (typed FeaturePython)
  Dunit = g/cm3
  Dvalue = 2.2
  Group = -> [C_element051,H_element044,N_element020,O_element048]
  conduct = 2
  density = 1
  expand = 3
  formula = G4_GUANINE
  name = G4_GUANINE
  specific = 4
FEATURE [App::DocumentObjectGroupPython] Ca_element012  label="Ca_element : 006"  # scripted group (container) (typed FeaturePython)
  n = 1
  ref = Ca_element
FEATURE [App::DocumentObjectGroupPython] S_element014  label="S_element : 005"  # scripted group (container) (typed FeaturePython)
  n = 1
  ref = S_element
FEATURE [App::DocumentObjectGroupPython] O_element049  label="O_element : 6"  # scripted group (container) (typed FeaturePython)
  n = 6
  ref = O_element
FEATURE [App::DocumentObjectGroupPython] H_element045  label="H_element : 024"  # scripted group (container) (typed FeaturePython)
  n = 4
  ref = H_element
FEATURE [App::DocumentObjectGroupPython] G4_GYPSUM  # scripted group (container) (typed FeaturePython)
  Dunit = g/cm3
  Dvalue = 2.32
  Group = -> [Ca_element012,S_element014,O_element049,H_element045]
  conduct = 2
  density = 1
  expand = 3
  formula = G4_GYPSUM
  name = G4_GYPSUM
  specific = 4
FEATURE [App::DocumentObjectGroupPython] C_element052  label="C_element : 7"  # scripted group (container) (typed FeaturePython)
  n = 7
  ref = C_element
FEATURE [App::DocumentObjectGroupPython] H_element046  label="H_element : 16"  # scripted group (container) (typed FeaturePython)
  n = 16
  ref = H_element
FEATURE [App::DocumentObjectGroupPython] G4_N_HEPTANE  label="G4_N-HEPTANE"  # scripted group (container) (typed FeaturePython)
  Dunit = g/cm3
  Dvalue = 0.68376
  Group = -> [C_element052,H_element046]
  conduct = 2
  density = 1
  expand = 3
  formula = G4_N-HEPTANE
  name = G4_N-HEPTANE
  specific = 4
FEATURE [App::DocumentObjectGroupPython] C_element053  label="C_element : 029"  # scripted group (container) (typed FeaturePython)
  n = 6
  ref = C_element
FEATURE [App::DocumentObjectGroupPython] H_element047  label="H_element : 14"  # scripted group (container) (typed FeaturePython)
  n = 14
  ref = H_element
FEATURE [App::DocumentObjectGroupPython] G4_N_HEXANE  label="G4_N-HEXANE"  # scripted group (container) (typed FeaturePython)
  Dunit = g/cm3
  Dvalue = 0.6603
  Group = -> [C_element053,H_element047]
  conduct = 2
  density = 1
  expand = 3
  formula = G4_N-HEXANE
  name = G4_N-HEXANE
  specific = 4
FEATURE [App::DocumentObjectGroupPython] C_element054  label="C_element : 22"  # scripted group (container) (typed FeaturePython)
  n = 22
  ref = C_element
FEATURE [App::DocumentObjectGroupPython] H_element048  label="H_element : 025"  # scripted group (container) (typed FeaturePython)
  n = 10
  ref = H_element
FEATURE [App::DocumentObjectGroupPython] N_element021  label="N_element : 010"  # scripted group (container) (typed FeaturePython)
  n = 2
  ref = N_element
FEATURE [App::DocumentObjectGroupPython] O_element050  label="O_element : 025"  # scripted group (container) (typed FeaturePython)
  n = 5
  ref = O_element
FEATURE [App::DocumentObjectGroupPython] G4_KAPTON  # scripted group (container) (typed FeaturePython)
  Dunit = g/cm3
  Dvalue = 1.42
  Group = -> [C_element054,H_element048,N_element021,O_element050]
  conduct = 2
  density = 1
  expand = 3
  formula = G4_KAPTON
  name = G4_KAPTON
  specific = 4
FEATURE [App::DocumentObjectGroupPython] La_element001  label="La_element : 1"  # scripted group (container) (typed FeaturePython)
  n = 1
  ref = La_element
FEATURE [App::DocumentObjectGroupPython] Br_element003  label="Br_element : 002"  # scripted group (container) (typed FeaturePython)
  n = 1
  ref = Br_element
FEATURE [App::DocumentObjectGroupPython] O_element051  label="O_element : 026"  # scripted group (container) (typed FeaturePython)
  n = 1
  ref = O_element
FEATURE [App::DocumentObjectGroupPython] G4_LANTHANUM_OXYBROMIDE  # scripted group (container) (typed FeaturePython)
  Dunit = g/cm3
  Dvalue = 6.28
  Group = -> [La_element001,Br_element003,O_element051]
  conduct = 2
  density = 1
  expand = 3
  formula = G4_LANTHANUM_OXYBROMIDE
  name = G4_LANTHANUM_OXYBROMIDE
  specific = 4
FEATURE [App::DocumentObjectGroupPython] La_element002  label="La_element : 2"  # scripted group (container) (typed FeaturePython)
  n = 2
  ref = La_element
FEATURE [App::DocumentObjectGroupPython] O_element052  label="O_element : 027"  # scripted group (container) (typed FeaturePython)
  n = 2
  ref = O_element
FEATURE [App::DocumentObjectGroupPython] S_element015  label="S_element : 006"  # scripted group (container) (typed FeaturePython)
  n = 1
  ref = S_element
FEATURE [App::DocumentObjectGroupPython] G4_LANTHANUM_OXYSULFIDE  # scripted group (container) (typed FeaturePython)
  Dunit = g/cm3
  Dvalue = 5.86
  Group = -> [La_element002,O_element052,S_element015]
  conduct = 2
  density = 1
  expand = 3
  formula = G4_LANTHANUM_OXYSULFIDE
  name = G4_LANTHANUM_OXYSULFIDE
  specific = 4
FEATURE [App::DocumentObjectGroupPython] O_element053  label="O_element : 0.072"  # scripted group (container) (typed FeaturePython)
  n = 0.071682
FEATURE [App::DocumentObjectGroupPython] Pb_element002  label="Pb_element : 0.928"  # scripted group (container) (typed FeaturePython)
  n = 0.928318
FEATURE [App::DocumentObjectGroupPython] G4_LEAD_OXIDE  # scripted group (container) (typed FeaturePython)
  Dunit = g/cm3
  Dvalue = 9.53
  Group = -> [O_element053,Pb_element002]
  conduct = 2
  density = 1
  expand = 3
  formula = G4_LEAD_OXIDE
  name = G4_LEAD_OXIDE
  specific = 4
FEATURE [App::DocumentObjectGroupPython] Li_element001  label="Li_element : 1"  # scripted group (container) (typed FeaturePython)
  n = 1
  ref = Li_element
FEATURE [App::DocumentObjectGroupPython] N_element022  label="N_element : 011"  # scripted group (container) (typed FeaturePython)
  n = 1
  ref = N_element
FEATURE [App::DocumentObjectGroupPython] H_element049  label="H_element : 026"  # scripted group (container) (typed FeaturePython)
  n = 2
  ref = H_element
FEATURE [App::DocumentObjectGroupPython] G4_LITHIUM_AMIDE  # scripted group (container) (typed FeaturePython)
  Dunit = g/cm3
  Dvalue = 1.178
  Group = -> [Li_element001,N_element022,H_element049]
  conduct = 2
  density = 1
  expand = 3
  formula = G4_LITHIUM_AMIDE
  name = G4_LITHIUM_AMIDE
  specific = 4
FEATURE [App::DocumentObjectGroupPython] Li_element002  label="Li_element : 2"  # scripted group (container) (typed FeaturePython)
  n = 2
  ref = Li_element
FEATURE [App::DocumentObjectGroupPython] C_element055  label="C_element : 030"  # scripted group (container) (typed FeaturePython)
  n = 1
  ref = C_element
FEATURE [App::DocumentObjectGroupPython] O_element054  label="O_element : 028"  # scripted group (container) (typed FeaturePython)
  n = 3
  ref = O_element
FEATURE [App::DocumentObjectGroupPython] G4_LITHIUM_CARBONATE  # scripted group (container) (typed FeaturePython)
  Dunit = g/cm3
  Dvalue = 2.11
  Group = -> [Li_element002,C_element055,O_element054]
  conduct = 2
  density = 1
  expand = 3
  formula = G4_LITHIUM_CARBONATE
  name = G4_LITHIUM_CARBONATE
  specific = 4
FEATURE [App::DocumentObjectGroupPython] Li_element003  label="Li_element : 003"  # scripted group (container) (typed FeaturePython)
  n = 1
  ref = Li_element
FEATURE [App::DocumentObjectGroupPython] F_element012  label="F_element : 004"  # scripted group (container) (typed FeaturePython)
  n = 1
  ref = F_element
FEATURE [App::DocumentObjectGroupPython] G4_LITHIUM_FLUORIDE  # scripted group (container) (typed FeaturePython)
  Dunit = g/cm3
  Dvalue = 2.635
  Group = -> [Li_element003,F_element012]
  conduct = 2
  density = 1
  expand = 3
  formula = G4_LITHIUM_FLUORIDE
  name = G4_LITHIUM_FLUORIDE
  specific = 4
FEATURE [App::DocumentObjectGroupPython] Li_element004  label="Li_element : 004"  # scripted group (container) (typed FeaturePython)
  n = 1
  ref = Li_element
FEATURE [App::DocumentObjectGroupPython] H_element050  label="H_element : 027"  # scripted group (container) (typed FeaturePython)
  n = 1
  ref = H_element
FEATURE [App::DocumentObjectGroupPython] G4_LITHIUM_HYDRIDE  # scripted group (container) (typed FeaturePython)
  Dunit = g/cm3
  Dvalue = 0.82
  Group = -> [Li_element004,H_element050]
  conduct = 2
  density = 1
  expand = 3
  formula = G4_LITHIUM_HYDRIDE
  name = G4_LITHIUM_HYDRIDE
  specific = 4
FEATURE [App::DocumentObjectGroupPython] Li_element005  label="Li_element : 005"  # scripted group (container) (typed FeaturePython)
  n = 1
  ref = Li_element
FEATURE [App::DocumentObjectGroupPython] I_element003  label="I_element : 002"  # scripted group (container) (typed FeaturePython)
  n = 1
  ref = I_element
FEATURE [App::DocumentObjectGroupPython] G4_LITHIUM_IODIDE  # scripted group (container) (typed FeaturePython)
  Dunit = g/cm3
  Dvalue = 3.494
  Group = -> [Li_element005,I_element003]
  conduct = 2
  density = 1
  expand = 3
  formula = G4_LITHIUM_IODIDE
  name = G4_LITHIUM_IODIDE
  specific = 4
FEATURE [App::DocumentObjectGroupPython] Li_element006  label="Li_element : 006"  # scripted group (container) (typed FeaturePython)
  n = 2
  ref = Li_element
FEATURE [App::DocumentObjectGroupPython] O_element055  label="O_element : 029"  # scripted group (container) (typed FeaturePython)
  n = 1
  ref = O_element
FEATURE [App::DocumentObjectGroupPython] G4_LITHIUM_OXIDE  # scripted group (container) (typed FeaturePython)
  Dunit = g/cm3
  Dvalue = 2.013
  Group = -> [Li_element006,O_element055]
  conduct = 2
  density = 1
  expand = 3
  formula = G4_LITHIUM_OXIDE
  name = G4_LITHIUM_OXIDE
  specific = 4
FEATURE [App::DocumentObjectGroupPython] Li_element007  label="Li_element : 007"  # scripted group (container) (typed FeaturePython)
  n = 2
  ref = Li_element
FEATURE [App::DocumentObjectGroupPython] B_element005  label="B_element : 005"  # scripted group (container) (typed FeaturePython)
  n = 4
  ref = B_element
FEATURE [App::DocumentObjectGroupPython] O_element056  label="O_element : 7"  # scripted group (container) (typed FeaturePython)
  n = 7
  ref = O_element
FEATURE [App::DocumentObjectGroupPython] G4_LITHIUM_TETRABORATE  # scripted group (container) (typed FeaturePython)
  Dunit = g/cm3
  Dvalue = 2.44
  Group = -> [Li_element007,B_element005,O_element056]
  conduct = 2
  density = 1
  expand = 3
  formula = G4_LITHIUM_TETRABORATE
  name = G4_LITHIUM_TETRABORATE
  specific = 4
FEATURE [App::DocumentObjectGroupPython] H_element051  label="H_element : 0.105"  # scripted group (container) (typed FeaturePython)
  n = 0.105
FEATURE [App::DocumentObjectGroupPython] C_element056  label="C_element : 0.083"  # scripted group (container) (typed FeaturePython)
  n = 0.083
FEATURE [App::DocumentObjectGroupPython] N_element023  label="N_element : 0.023"  # scripted group (container) (typed FeaturePython)
  n = 0.023
FEATURE [App::DocumentObjectGroupPython] O_element057  label="O_element : 0.779"  # scripted group (container) (typed FeaturePython)
  n = 0.779
FEATURE [App::DocumentObjectGroupPython] Na_element010  label="Na_element : 0.097"  # scripted group (container) (typed FeaturePython)
  n = 0.002
FEATURE [App::DocumentObjectGroupPython] P_element006  label="P_element : 0.105"  # scripted group (container) (typed FeaturePython)
  n = 0.001
FEATURE [App::DocumentObjectGroupPython] S_element016  label="S_element : 0.017"  # scripted group (container) (typed FeaturePython)
  n = 0.002
FEATURE [App::DocumentObjectGroupPython] Cl_element014  label="Cl_element : 0.587"  # scripted group (container) (typed FeaturePython)
  n = 0.003
FEATURE [App::DocumentObjectGroupPython] K_element005  label="K_element : 0.015"  # scripted group (container) (typed FeaturePython)
  n = 0.002
FEATURE [App::DocumentObjectGroupPython] G4_LUNG_ICRP  # scripted group (container) (typed FeaturePython)
  Dunit = g/cm3
  Dvalue = 1.04
  Group = -> [H_element051,C_element056,N_element023,O_element057,Na_element010,P_element006,S_element016,Cl_element014,K_element005]
  conduct = 2
  density = 1
  expand = 3
  formula = G4_LUNG_ICRP
  name = G4_LUNG_ICRP
  specific = 4
FEATURE [App::DocumentObjectGroupPython] H_element052  label="H_element : 0.116"  # scripted group (container) (typed FeaturePython)
  n = 0.114318
FEATURE [App::DocumentObjectGroupPython] C_element057  label="C_element : 0.656"  # scripted group (container) (typed FeaturePython)
  n = 0.655824
FEATURE [App::DocumentObjectGroupPython] O_element058  label="O_element : 0.092"  # scripted group (container) (typed FeaturePython)
  n = 0.0921831
FEATURE [App::DocumentObjectGroupPython] Mg_element004  label="Mg_element : 0.135"  # scripted group (container) (typed FeaturePython)
  n = 0.134792
FEATURE [App::DocumentObjectGroupPython] Ca_element013  label="Ca_element : 0.003"  # scripted group (container) (typed FeaturePython)
  n = 0.002883
FEATURE [App::DocumentObjectGroupPython] G4_M3_WAX  # scripted group (container) (typed FeaturePython)
  Dunit = g/cm3
  Dvalue = 1.05
  Group = -> [H_element052,C_element057,O_element058,Mg_element004,Ca_element013]
  conduct = 2
  density = 1
  expand = 3
  formula = G4_M3_WAX
  name = G4_M3_WAX
  specific = 4
FEATURE [App::DocumentObjectGroupPython] Mg_element005  label="Mg_element : 1"  # scripted group (container) (typed FeaturePython)
  n = 1
  ref = Mg_element
FEATURE [App::DocumentObjectGroupPython] C_element058  label="C_element : 031"  # scripted group (container) (typed FeaturePython)
  n = 1
  ref = C_element
FEATURE [App::DocumentObjectGroupPython] O_element059  label="O_element : 030"  # scripted group (container) (typed FeaturePython)
  n = 3
  ref = O_element
FEATURE [App::DocumentObjectGroupPython] G4_MAGNESIUM_CARBONATE  # scripted group (container) (typed FeaturePython)
  Dunit = g/cm3
  Dvalue = 2.958
  Group = -> [Mg_element005,C_element058,O_element059]
  conduct = 2
  density = 1
  expand = 3
  formula = G4_MAGNESIUM_CARBONATE
  name = G4_MAGNESIUM_CARBONATE
  specific = 4
FEATURE [App::DocumentObjectGroupPython] Mg_element006  label="Mg_element : 002"  # scripted group (container) (typed FeaturePython)
  n = 1
  ref = Mg_element
FEATURE [App::DocumentObjectGroupPython] F_element013  label="F_element : 005"  # scripted group (container) (typed FeaturePython)
  n = 2
  ref = F_element
FEATURE [App::DocumentObjectGroupPython] G4_MAGNESIUM_FLUORIDE  # scripted group (container) (typed FeaturePython)
  Dunit = g/cm3
  Dvalue = 3
  Group = -> [Mg_element006,F_element013]
  conduct = 2
  density = 1
  expand = 3
  formula = G4_MAGNESIUM_FLUORIDE
  name = G4_MAGNESIUM_FLUORIDE
  specific = 4
FEATURE [App::DocumentObjectGroupPython] Mg_element007  label="Mg_element : 003"  # scripted group (container) (typed FeaturePython)
  n = 1
  ref = Mg_element
FEATURE [App::DocumentObjectGroupPython] O_element060  label="O_element : 031"  # scripted group (container) (typed FeaturePython)
  n = 1
  ref = O_element
FEATURE [App::DocumentObjectGroupPython] G4_MAGNESIUM_OXIDE  # scripted group (container) (typed FeaturePython)
  Dunit = g/cm3
  Dvalue = 3.58
  Group = -> [Mg_element007,O_element060]
  conduct = 2
  density = 1
  expand = 3
  formula = G4_MAGNESIUM_OXIDE
  name = G4_MAGNESIUM_OXIDE
  specific = 4
FEATURE [App::DocumentObjectGroupPython] Mg_element008  label="Mg_element : 004"  # scripted group (container) (typed FeaturePython)
  n = 1
  ref = Mg_element
FEATURE [App::DocumentObjectGroupPython] B_element006  label="B_element : 006"  # scripted group (container) (typed FeaturePython)
  n = 4
  ref = B_element
FEATURE [App::DocumentObjectGroupPython] O_element061  label="O_element : 032"  # scripted group (container) (typed FeaturePython)
  n = 7
  ref = O_element
FEATURE [App::DocumentObjectGroupPython] G4_MAGNESIUM_TETRABORATE  # scripted group (container) (typed FeaturePython)
  Dunit = g/cm3
  Dvalue = 2.53
  Group = -> [Mg_element008,B_element006,O_element061]
  conduct = 2
  density = 1
  expand = 3
  formula = G4_MAGNESIUM_TETRABORATE
  name = G4_MAGNESIUM_TETRABORATE
  specific = 4
FEATURE [App::DocumentObjectGroupPython] Hg_element001  label="Hg_element : 1"  # scripted group (container) (typed FeaturePython)
  n = 1
  ref = Hg_element
FEATURE [App::DocumentObjectGroupPython] I_element004  label="I_element : 2"  # scripted group (container) (typed FeaturePython)
  n = 2
  ref = I_element
FEATURE [App::DocumentObjectGroupPython] G4_MERCURIC_IODIDE  # scripted group (container) (typed FeaturePython)
  Dunit = g/cm3
  Dvalue = 6.36
  Group = -> [Hg_element001,I_element004]
  conduct = 2
  density = 1
  expand = 3
  formula = G4_MERCURIC_IODIDE
  name = G4_MERCURIC_IODIDE
  specific = 4
FEATURE [App::DocumentObjectGroupPython] C_element059  label="C_element : 032"  # scripted group (container) (typed FeaturePython)
  n = 1
  ref = C_element
FEATURE [App::DocumentObjectGroupPython] H_element053  label="H_element : 028"  # scripted group (container) (typed FeaturePython)
  n = 4
  ref = H_element
FEATURE [App::DocumentObjectGroupPython] G4_METHANE  # scripted group (container) (typed FeaturePython)
  Dunit = g/cm3
  Dvalue = 0.000667151
  Group = -> [C_element059,H_element053]
  conduct = 2
  density = 1
  expand = 3
  formula = G4_METHANE
  name = G4_METHANE
  specific = 4
FEATURE [App::DocumentObjectGroupPython] C_element060  label="C_element : 033"  # scripted group (container) (typed FeaturePython)
  n = 1
  ref = C_element
FEATURE [App::DocumentObjectGroupPython] H_element054  label="H_element : 029"  # scripted group (container) (typed FeaturePython)
  n = 4
  ref = H_element
FEATURE [App::DocumentObjectGroupPython] O_element062  label="O_element : 033"  # scripted group (container) (typed FeaturePython)
  n = 1
  ref = O_element
FEATURE [App::DocumentObjectGroupPython] G4_METHANOL  # scripted group (container) (typed FeaturePython)
  Dunit = g/cm3
  Dvalue = 0.7914
  Group = -> [C_element060,H_element054,O_element062]
  conduct = 2
  density = 1
  expand = 3
  formula = G4_METHANOL
  name = G4_METHANOL
  specific = 4
FEATURE [App::DocumentObjectGroupPython] H_element055  label="H_element : 0.134"  # scripted group (container) (typed FeaturePython)
  n = 0.13404
FEATURE [App::DocumentObjectGroupPython] C_element061  label="C_element : 0.778"  # scripted group (container) (typed FeaturePython)
  n = 0.77796
FEATURE [App::DocumentObjectGroupPython] O_element063  label="O_element : 0.035"  # scripted group (container) (typed FeaturePython)
  n = 0.03502
FEATURE [App::DocumentObjectGroupPython] Mg_element009  label="Mg_element : 0.039"  # scripted group (container) (typed FeaturePython)
  n = 0.038594
FEATURE [App::DocumentObjectGroupPython] Ti_element002  label="Ti_element : 0.014"  # scripted group (container) (typed FeaturePython)
  n = 0.014386
FEATURE [App::DocumentObjectGroupPython] G4_MIX_D_WAX  # scripted group (container) (typed FeaturePython)
  Dunit = g/cm3
  Dvalue = 0.99
  Group = -> [H_element055,C_element061,O_element063,Mg_element009,Ti_element002]
  conduct = 2
  density = 1
  expand = 3
  formula = G4_MIX_D_WAX
  name = G4_MIX_D_WAX
  specific = 4
FEATURE [App::DocumentObjectGroupPython] H_element056  label="H_element : 0.135"  # scripted group (container) (typed FeaturePython)
  n = 0.081192
FEATURE [App::DocumentObjectGroupPython] C_element062  label="C_element : 0.583"  # scripted group (container) (typed FeaturePython)
  n = 0.583442
FEATURE [App::DocumentObjectGroupPython] N_element024  label="N_element : 0.018"  # scripted group (container) (typed FeaturePython)
  n = 0.017798
FEATURE [App::DocumentObjectGroupPython] O_element064  label="O_element : 0.186"  # scripted group (container) (typed FeaturePython)
  n = 0.186381
FEATURE [App::DocumentObjectGroupPython] Mg_element010  label="Mg_element : 0.130"  # scripted group (container) (typed FeaturePython)
  n = 0.130287
FEATURE [App::DocumentObjectGroupPython] Cl_element015  label="Cl_element : 0.588"  # scripted group (container) (typed FeaturePython)
  n = 0.0009
FEATURE [App::DocumentObjectGroupPython] G4_MS20_TISSUE  # scripted group (container) (typed FeaturePython)
  Dunit = g/cm3
  Dvalue = 1
  Group = -> [H_element056,C_element062,N_element024,O_element064,Mg_element010,Cl_element015]
  conduct = 2
  density = 1
  expand = 3
  formula = G4_MS20_TISSUE
  name = G4_MS20_TISSUE
  specific = 4
FEATURE [App::DocumentObjectGroupPython] H_element057  label="H_element : 0.136"  # scripted group (container) (typed FeaturePython)
  n = 0.102
FEATURE [App::DocumentObjectGroupPython] C_element063  label="C_element : 0.143"  # scripted group (container) (typed FeaturePython)
  n = 0.143
FEATURE [App::DocumentObjectGroupPython] N_element025  label="N_element : 0.034"  # scripted group (container) (typed FeaturePython)
  n = 0.034
FEATURE [App::DocumentObjectGroupPython] O_element065  label="O_element : 0.710"  # scripted group (container) (typed FeaturePython)
  n = 0.71
FEATURE [App::DocumentObjectGroupPython] Na_element011  label="Na_element : 0.098"  # scripted group (container) (typed FeaturePython)
  n = 0.001
FEATURE [App::DocumentObjectGroupPython] P_element007  label="P_element : 0.002"  # scripted group (container) (typed FeaturePython)
  n = 0.002
FEATURE [App::DocumentObjectGroupPython] S_element017  label="S_element : 0.018"  # scripted group (container) (typed FeaturePython)
  n = 0.003
FEATURE [App::DocumentObjectGroupPython] Cl_element016  label="Cl_element : 0.589"  # scripted group (container) (typed FeaturePython)
  n = 0.001
FEATURE [App::DocumentObjectGroupPython] K_element006  label="K_element : 0.004"  # scripted group (container) (typed FeaturePython)
  n = 0.004
FEATURE [App::DocumentObjectGroupPython] G4_MUSCLE_SKELETAL_ICRP  # scripted group (container) (typed FeaturePython)
  Dunit = g/cm3
  Dvalue = 1.05
  Group = -> [H_element057,C_element063,N_element025,O_element065,Na_element011,P_element007,S_element017,Cl_element016,K_element006]
  conduct = 2
  density = 1
  expand = 3
  formula = G4_MUSCLE_SKELETAL_ICRP
  name = G4_MUSCLE_SKELETAL_ICRP
  specific = 4
FEATURE [App::DocumentObjectGroupPython] H_element058  label="H_element : 0.137"  # scripted group (container) (typed FeaturePython)
  n = 0.102102
FEATURE [App::DocumentObjectGroupPython] C_element064  label="C_element : 0.123"  # scripted group (container) (typed FeaturePython)
  n = 0.123123
FEATURE [App::DocumentObjectGroupPython] N_element026  label="N_element : 0.756"  # scripted group (container) (typed FeaturePython)
  n = 0.035035
FEATURE [App::DocumentObjectGroupPython] O_element066  label="O_element : 0.730"  # scripted group (container) (typed FeaturePython)
  n = 0.72973
FEATURE [App::DocumentObjectGroupPython] Na_element012  label="Na_element : 0.099"  # scripted group (container) (typed FeaturePython)
  n = 0.001001
FEATURE [App::DocumentObjectGroupPython] P_element008  label="P_element : 0.106"  # scripted group (container) (typed FeaturePython)
  n = 0.002002
FEATURE [App::DocumentObjectGroupPython] S_element018  label="S_element : 0.019"  # scripted group (container) (typed FeaturePython)
  n = 0.004004
FEATURE [App::DocumentObjectGroupPython] K_element007  label="K_element : 0.016"  # scripted group (container) (typed FeaturePython)
  n = 0.003003
FEATURE [App::DocumentObjectGroupPython] G4_MUSCLE_STRIATED_ICRU  # scripted group (container) (typed FeaturePython)
  Dunit = g/cm3
  Dvalue = 1.04
  Group = -> [H_element058,C_element064,N_element026,O_element066,Na_element012,P_element008,S_element018,K_element007]
  conduct = 2
  density = 1
  expand = 3
  formula = G4_MUSCLE_STRIATED_ICRU
  name = G4_MUSCLE_STRIATED_ICRU
  specific = 4
FEATURE [App::DocumentObjectGroupPython] H_element059  label="H_element : 0.098"  # scripted group (container) (typed FeaturePython)
  n = 0.0982341
FEATURE [App::DocumentObjectGroupPython] C_element065  label="C_element : 0.156"  # scripted group (container) (typed FeaturePython)
  n = 0.156214
FEATURE [App::DocumentObjectGroupPython] N_element027  label="N_element : 0.757"  # scripted group (container) (typed FeaturePython)
  n = 0.035451
FEATURE [App::DocumentObjectGroupPython] O_element067  label="O_element : 0.880"  # scripted group (container) (typed FeaturePython)
  n = 0.710101
FEATURE [App::DocumentObjectGroupPython] G4_MUSCLE_WITH_SUCROSE  # scripted group (container) (typed FeaturePython)
  Dunit = g/cm3
  Dvalue = 1.11
  Group = -> [H_element059,C_element065,N_element027,O_element067]
  conduct = 2
  density = 1
  expand = 3
  formula = G4_MUSCLE_WITH_SUCROSE
  name = G4_MUSCLE_WITH_SUCROSE
  specific = 4
FEATURE [App::DocumentObjectGroupPython] H_element060  label="H_element : 0.138"  # scripted group (container) (typed FeaturePython)
  n = 0.101969
FEATURE [App::DocumentObjectGroupPython] C_element066  label="C_element : 0.120"  # scripted group (container) (typed FeaturePython)
  n = 0.120058
FEATURE [App::DocumentObjectGroupPython] N_element028  label="N_element : 0.758"  # scripted group (container) (typed FeaturePython)
  n = 0.035451
FEATURE [App::DocumentObjectGroupPython] O_element068  label="O_element : 0.743"  # scripted group (container) (typed FeaturePython)
  n = 0.742522
FEATURE [App::DocumentObjectGroupPython] G4_MUSCLE_WITHOUT_SUCROSE  # scripted group (container) (typed FeaturePython)
  Dunit = g/cm3
  Dvalue = 1.07
  Group = -> [H_element060,C_element066,N_element028,O_element068]
  conduct = 2
  density = 1
  expand = 3
  formula = G4_MUSCLE_WITHOUT_SUCROSE
  name = G4_MUSCLE_WITHOUT_SUCROSE
  specific = 4
FEATURE [App::DocumentObjectGroupPython] C_element067  label="C_element : 10"  # scripted group (container) (typed FeaturePython)
  n = 10
  ref = C_element
FEATURE [App::DocumentObjectGroupPython] H_element061  label="H_element : 030"  # scripted group (container) (typed FeaturePython)
  n = 8
  ref = H_element
FEATURE [App::DocumentObjectGroupPython] G4_NAPHTHALENE  # scripted group (container) (typed FeaturePython)
  Dunit = g/cm3
  Dvalue = 1.145
  Group = -> [C_element067,H_element061]
  conduct = 2
  density = 1
  expand = 3
  formula = G4_NAPHTHALENE
  name = G4_NAPHTHALENE
  specific = 4
FEATURE [App::DocumentObjectGroupPython] C_element068  label="C_element : 034"  # scripted group (container) (typed FeaturePython)
  n = 6
  ref = C_element
FEATURE [App::DocumentObjectGroupPython] H_element062  label="H_element : 031"  # scripted group (container) (typed FeaturePython)
  n = 5
  ref = H_element
FEATURE [App::DocumentObjectGroupPython] N_element029  label="N_element : 012"  # scripted group (container) (typed FeaturePython)
  n = 1
  ref = N_element
FEATURE [App::DocumentObjectGroupPython] O_element069  label="O_element : 034"  # scripted group (container) (typed FeaturePython)
  n = 2
  ref = O_element
FEATURE [App::DocumentObjectGroupPython] G4_NITROBENZENE  # scripted group (container) (typed FeaturePython)
  Dunit = g/cm3
  Dvalue = 1.19867
  Group = -> [C_element068,H_element062,N_element029,O_element069]
  conduct = 2
  density = 1
  expand = 3
  formula = G4_NITROBENZENE
  name = G4_NITROBENZENE
  specific = 4
FEATURE [App::DocumentObjectGroupPython] N_element030  label="N_element : 013"  # scripted group (container) (typed FeaturePython)
  n = 2
  ref = N_element
FEATURE [App::DocumentObjectGroupPython] O_element070  label="O_element : 035"  # scripted group (container) (typed FeaturePython)
  n = 1
  ref = O_element
FEATURE [App::DocumentObjectGroupPython] G4_NITROUS_OXIDE  # scripted group (container) (typed FeaturePython)
  Dunit = g/cm3
  Dvalue = 0.00183094
  Group = -> [N_element030,O_element070]
  conduct = 2
  density = 1
  expand = 3
  formula = G4_NITROUS_OXIDE
  name = G4_NITROUS_OXIDE
  specific = 4
FEATURE [App::DocumentObjectGroupPython] H_element063  label="H_element : 0.104"  # scripted group (container) (typed FeaturePython)
  n = 0.103509
FEATURE [App::DocumentObjectGroupPython] C_element069  label="C_element : 0.648"  # scripted group (container) (typed FeaturePython)
  n = 0.648416
FEATURE [App::DocumentObjectGroupPython] N_element031  label="N_element : 0.100"  # scripted group (container) (typed FeaturePython)
  n = 0.0995361
FEATURE [App::DocumentObjectGroupPython] O_element071  label="O_element : 0.149"  # scripted group (container) (typed FeaturePython)
  n = 0.148539
FEATURE [App::DocumentObjectGroupPython] G4_NYLON_8062  label="G4_NYLON-8062"  # scripted group (container) (typed FeaturePython)
  Dunit = g/cm3
  Dvalue = 1.08
  Group = -> [H_element063,C_element069,N_element031,O_element071]
  conduct = 2
  density = 1
  expand = 3
  formula = G4_NYLON-8062
  name = G4_NYLON-8062
  specific = 4
FEATURE [App::DocumentObjectGroupPython] C_element070  label="C_element : 035"  # scripted group (container) (typed FeaturePython)
  n = 6
  ref = C_element
FEATURE [App::DocumentObjectGroupPython] H_element064  label="H_element : 11"  # scripted group (container) (typed FeaturePython)
  n = 11
  ref = H_element
FEATURE [App::DocumentObjectGroupPython] N_element032  label="N_element : 014"  # scripted group (container) (typed FeaturePython)
  n = 1
  ref = N_element
FEATURE [App::DocumentObjectGroupPython] O_element072  label="O_element : 036"  # scripted group (container) (typed FeaturePython)
  n = 1
  ref = O_element
FEATURE [App::DocumentObjectGroupPython] G4_NYLON_6_6  label="G4_NYLON-6-6"  # scripted group (container) (typed FeaturePython)
  Dunit = g/cm3
  Dvalue = 1.14
  Group = -> [C_element070,H_element064,N_element032,O_element072]
  conduct = 2
  density = 1
  expand = 3
  formula = G4_NYLON-6-6
  name = G4_NYLON-6-6
  specific = 4
FEATURE [App::DocumentObjectGroupPython] H_element065  label="H_element : 0.139"  # scripted group (container) (typed FeaturePython)
  n = 0.107062
FEATURE [App::DocumentObjectGroupPython] C_element071  label="C_element : 0.680"  # scripted group (container) (typed FeaturePython)
  n = 0.680449
FEATURE [App::DocumentObjectGroupPython] N_element033  label="N_element : 0.099"  # scripted group (container) (typed FeaturePython)
  n = 0.099189
FEATURE [App::DocumentObjectGroupPython] O_element073  label="O_element : 0.113"  # scripted group (container) (typed FeaturePython)
  n = 0.1133
FEATURE [App::DocumentObjectGroupPython] G4_NYLON_6_10  label="G4_NYLON-6-10"  # scripted group (container) (typed FeaturePython)
  Dunit = g/cm3
  Dvalue = 1.14
  Group = -> [H_element065,C_element071,N_element033,O_element073]
  conduct = 2
  density = 1
  expand = 3
  formula = G4_NYLON-6-10
  name = G4_NYLON-6-10
  specific = 4
FEATURE [App::DocumentObjectGroupPython] H_element066  label="H_element : 0.140"  # scripted group (container) (typed FeaturePython)
  n = 0.115476
FEATURE [App::DocumentObjectGroupPython] C_element072  label="C_element : 0.721"  # scripted group (container) (typed FeaturePython)
  n = 0.720818
FEATURE [App::DocumentObjectGroupPython] N_element034  label="N_element : 0.076"  # scripted group (container) (typed FeaturePython)
  n = 0.0764169
FEATURE [App::DocumentObjectGroupPython] O_element074  label="O_element : 0.087"  # scripted group (container) (typed FeaturePython)
  n = 0.0872889
FEATURE [App::DocumentObjectGroupPython] G4_NYLON_11_RILSAN  label="G4_NYLON-11_RILSAN"  # scripted group (container) (typed FeaturePython)
  Dunit = g/cm3
  Dvalue = 1.425
  Group = -> [H_element066,C_element072,N_element034,O_element074]
  conduct = 2
  density = 1
  expand = 3
  formula = G4_NYLON-11_RILSAN
  name = G4_NYLON-11_RILSAN
  specific = 4
FEATURE [App::DocumentObjectGroupPython] C_element073  label="C_element : 8"  # scripted group (container) (typed FeaturePython)
  n = 8
  ref = C_element
FEATURE [App::DocumentObjectGroupPython] H_element067  label="H_element : 18"  # scripted group (container) (typed FeaturePython)
  n = 18
  ref = H_element
FEATURE [App::DocumentObjectGroupPython] G4_OCTANE  # scripted group (container) (typed FeaturePython)
  Dunit = g/cm3
  Dvalue = 0.7026
  Group = -> [C_element073,H_element067]
  conduct = 2
  density = 1
  expand = 3
  formula = G4_OCTANE
  name = G4_OCTANE
  specific = 4
FEATURE [App::DocumentObjectGroupPython] C_element074  label="C_element : 25"  # scripted group (container) (typed FeaturePython)
  n = 25
  ref = C_element
FEATURE [App::DocumentObjectGroupPython] H_element068  label="H_element : 52"  # scripted group (container) (typed FeaturePython)
  n = 52
  ref = H_element
FEATURE [App::DocumentObjectGroupPython] G4_PARAFFIN  # scripted group (container) (typed FeaturePython)
  Dunit = g/cm3
  Dvalue = 0.93
  Group = -> [C_element074,H_element068]
  conduct = 2
  density = 1
  expand = 3
  formula = G4_PARAFFIN
  name = G4_PARAFFIN
  specific = 4
FEATURE [App::DocumentObjectGroupPython] C_element075  label="C_element : 036"  # scripted group (container) (typed FeaturePython)
  n = 5
  ref = C_element
FEATURE [App::DocumentObjectGroupPython] H_element069  label="H_element : 032"  # scripted group (container) (typed FeaturePython)
  n = 12
  ref = H_element
FEATURE [App::DocumentObjectGroupPython] G4_N_PENTANE  label="G4_N-PENTANE"  # scripted group (container) (typed FeaturePython)
  Dunit = g/cm3
  Dvalue = 0.6262
  Group = -> [C_element075,H_element069]
  conduct = 2
  density = 1
  expand = 3
  formula = G4_N-PENTANE
  name = G4_N-PENTANE
  specific = 4
FEATURE [App::DocumentObjectGroupPython] H_element070  label="H_element : 0.014"  # scripted group (container) (typed FeaturePython)
  n = 0.0141
FEATURE [App::DocumentObjectGroupPython] C_element076  label="C_element : 0.072"  # scripted group (container) (typed FeaturePython)
  n = 0.072261
FEATURE [App::DocumentObjectGroupPython] N_element035  label="N_element : 0.019"  # scripted group (container) (typed FeaturePython)
  n = 0.01932
FEATURE [App::DocumentObjectGroupPython] O_element075  label="O_element : 0.066"  # scripted group (container) (typed FeaturePython)
  n = 0.066101
FEATURE [App::DocumentObjectGroupPython] S_element019  label="S_element : 0.020"  # scripted group (container) (typed FeaturePython)
  n = 0.00189
FEATURE [App::DocumentObjectGroupPython] Br_element004  label="Br_element : 0.349"  # scripted group (container) (typed FeaturePython)
  n = 0.349103
FEATURE [App::DocumentObjectGroupPython] Ag_element001  label="Ag_element : 0.474"  # scripted group (container) (typed FeaturePython)
  n = 0.474105
FEATURE [App::DocumentObjectGroupPython] I_element005  label="I_element : 0.003"  # scripted group (container) (typed FeaturePython)
  n = 0.00312
FEATURE [App::DocumentObjectGroupPython] G4_PHOTO_EMULSION  # scripted group (container) (typed FeaturePython)
  Dunit = g/cm3
  Dvalue = 3.815
  Group = -> [H_element070,C_element076,N_element035,O_element075,S_element019,Br_element004,Ag_element001,I_element005]
  conduct = 2
  density = 1
  expand = 3
  formula = G4_PHOTO_EMULSION
  name = G4_PHOTO_EMULSION
  specific = 4
FEATURE [App::DocumentObjectGroupPython] C_element077  label="C_element : 9"  # scripted group (container) (typed FeaturePython)
  n = 9
  ref = C_element
FEATURE [App::DocumentObjectGroupPython] H_element071  label="H_element : 033"  # scripted group (container) (typed FeaturePython)
  n = 10
  ref = H_element
FEATURE [App::DocumentObjectGroupPython] G4_PLASTIC_SC_VINYLTOLUENE  # scripted group (container) (typed FeaturePython)
  Dunit = g/cm3
  Dvalue = 1.032
  Group = -> [C_element077,H_element071]
  conduct = 2
  density = 1
  expand = 3
  formula = G4_PLASTIC_SC_VINYLTOLUENE
  name = G4_PLASTIC_SC_VINYLTOLUENE
  specific = 4
FEATURE [App::DocumentObjectGroupPython] Pu_element001  label="Pu_element : 1"  # scripted group (container) (typed FeaturePython)
  n = 1
  ref = Pu_element
FEATURE [App::DocumentObjectGroupPython] O_element076  label="O_element : 037"  # scripted group (container) (typed FeaturePython)
  n = 2
  ref = O_element
FEATURE [App::DocumentObjectGroupPython] G4_PLUTONIUM_DIOXIDE  # scripted group (container) (typed FeaturePython)
  Dunit = g/cm3
  Dvalue = 11.46
  Group = -> [Pu_element001,O_element076]
  conduct = 2
  density = 1
  expand = 3
  formula = G4_PLUTONIUM_DIOXIDE
  name = G4_PLUTONIUM_DIOXIDE
  specific = 4
FEATURE [App::DocumentObjectGroupPython] C_element078  label="C_element : 037"  # scripted group (container) (typed FeaturePython)
  n = 3
  ref = C_element
FEATURE [App::DocumentObjectGroupPython] H_element072  label="H_element : 034"  # scripted group (container) (typed FeaturePython)
  n = 3
  ref = H_element
FEATURE [App::DocumentObjectGroupPython] N_element036  label="N_element : 015"  # scripted group (container) (typed FeaturePython)
  n = 1
  ref = N_element
FEATURE [App::DocumentObjectGroupPython] G4_POLYACRYLONITRILE  # scripted group (container) (typed FeaturePython)
  Dunit = g/cm3
  Dvalue = 1.17
  Group = -> [C_element078,H_element072,N_element036]
  conduct = 2
  density = 1
  expand = 3
  formula = G4_POLYACRYLONITRILE
  name = G4_POLYACRYLONITRILE
  specific = 4
FEATURE [App::DocumentObjectGroupPython] C_element079  label="C_element : 16"  # scripted group (container) (typed FeaturePython)
  n = 16
  ref = C_element
FEATURE [App::DocumentObjectGroupPython] H_element073  label="H_element : 035"  # scripted group (container) (typed FeaturePython)
  n = 14
  ref = H_element
FEATURE [App::DocumentObjectGroupPython] O_element077  label="O_element : 038"  # scripted group (container) (typed FeaturePython)
  n = 3
  ref = O_element
FEATURE [App::DocumentObjectGroupPython] G4_POLYCARBONATE  # scripted group (container) (typed FeaturePython)
  Dunit = g/cm3
  Dvalue = 1.2
  Group = -> [C_element079,H_element073,O_element077]
  conduct = 2
  density = 1
  expand = 3
  formula = G4_POLYCARBONATE
  name = G4_POLYCARBONATE
  specific = 4
FEATURE [App::DocumentObjectGroupPython] C_element080  label="C_element : 038"  # scripted group (container) (typed FeaturePython)
  n = 8
  ref = C_element
FEATURE [App::DocumentObjectGroupPython] H_element074  label="H_element : 036"  # scripted group (container) (typed FeaturePython)
  n = 7
  ref = H_element
FEATURE [App::DocumentObjectGroupPython] Cl_element017  label="Cl_element : 007"  # scripted group (container) (typed FeaturePython)
  n = 1
  ref = Cl_element
FEATURE [App::DocumentObjectGroupPython] G4_POLYCHLOROSTYRENE  # scripted group (container) (typed FeaturePython)
  Dunit = g/cm3
  Dvalue = 1.3
  Group = -> [C_element080,H_element074,Cl_element017]
  conduct = 2
  density = 1
  expand = 3
  formula = G4_POLYCHLOROSTYRENE
  name = G4_POLYCHLOROSTYRENE
  specific = 4
FEATURE [App::DocumentObjectGroupPython] C_element081  label="C_element : 039"  # scripted group (container) (typed FeaturePython)
  n = 1
  ref = C_element
FEATURE [App::DocumentObjectGroupPython] H_element075  label="H_element : 037"  # scripted group (container) (typed FeaturePython)
  n = 2
  ref = H_element
FEATURE [App::DocumentObjectGroupPython] G4_POLYETHYLENE  # scripted group (container) (typed FeaturePython)
  Dunit = g/cm3
  Dvalue = 0.94
  Group = -> [C_element081,H_element075]
  conduct = 2
  density = 1
  expand = 3
  formula = G4_POLYETHYLENE
  name = G4_POLYETHYLENE
  specific = 4
FEATURE [App::DocumentObjectGroupPython] C_element082  label="C_element : 040"  # scripted group (container) (typed FeaturePython)
  n = 10
  ref = C_element
FEATURE [App::DocumentObjectGroupPython] H_element076  label="H_element : 038"  # scripted group (container) (typed FeaturePython)
  n = 8
  ref = H_element
FEATURE [App::DocumentObjectGroupPython] O_element078  label="O_element : 039"  # scripted group (container) (typed FeaturePython)
  n = 4
  ref = O_element
FEATURE [App::DocumentObjectGroupPython] G4_MYLAR  # scripted group (container) (typed FeaturePython)
  Dunit = g/cm3
  Dvalue = 1.4
  Group = -> [C_element082,H_element076,O_element078]
  conduct = 2
  density = 1
  expand = 3
  formula = G4_MYLAR
  name = G4_MYLAR
  specific = 4
FEATURE [App::DocumentObjectGroupPython] C_element083  label="C_element : 041"  # scripted group (container) (typed FeaturePython)
  n = 5
  ref = C_element
FEATURE [App::DocumentObjectGroupPython] H_element077  label="H_element : 039"  # scripted group (container) (typed FeaturePython)
  n = 8
  ref = H_element
FEATURE [App::DocumentObjectGroupPython] O_element079  label="O_element : 040"  # scripted group (container) (typed FeaturePython)
  n = 2
  ref = O_element
FEATURE [App::DocumentObjectGroupPython] G4_PLEXIGLASS  # scripted group (container) (typed FeaturePython)
  Dunit = g/cm3
  Dvalue = 1.19
  Group = -> [C_element083,H_element077,O_element079]
  conduct = 2
  density = 1
  expand = 3
  formula = G4_PLEXIGLASS
  name = G4_PLEXIGLASS
  specific = 4
FEATURE [App::DocumentObjectGroupPython] C_element084  label="C_element : 042"  # scripted group (container) (typed FeaturePython)
  n = 1
  ref = C_element
FEATURE [App::DocumentObjectGroupPython] H_element078  label="H_element : 040"  # scripted group (container) (typed FeaturePython)
  n = 2
  ref = H_element
FEATURE [App::DocumentObjectGroupPython] O_element080  label="O_element : 041"  # scripted group (container) (typed FeaturePython)
  n = 1
  ref = O_element
FEATURE [App::DocumentObjectGroupPython] G4_POLYOXYMETHYLENE  # scripted group (container) (typed FeaturePython)
  Dunit = g/cm3
  Dvalue = 1.425
  Group = -> [C_element084,H_element078,O_element080]
  conduct = 2
  density = 1
  expand = 3
  formula = G4_POLYOXYMETHYLENE
  name = G4_POLYOXYMETHYLENE
  specific = 4
FEATURE [App::DocumentObjectGroupPython] C_element085  label="C_element : 043"  # scripted group (container) (typed FeaturePython)
  n = 2
  ref = C_element
FEATURE [App::DocumentObjectGroupPython] H_element079  label="H_element : 041"  # scripted group (container) (typed FeaturePython)
  n = 4
  ref = H_element
FEATURE [App::DocumentObjectGroupPython] G4_POLYPROPYLENE  # scripted group (container) (typed FeaturePython)
  Dunit = g/cm3
  Dvalue = 0.9
  Group = -> [C_element085,H_element079]
  conduct = 2
  density = 1
  expand = 3
  formula = G4_POLYPROPYLENE
  name = G4_POLYPROPYLENE
  specific = 4
FEATURE [App::DocumentObjectGroupPython] C_element086  label="C_element : 044"  # scripted group (container) (typed FeaturePython)
  n = 8
  ref = C_element
FEATURE [App::DocumentObjectGroupPython] H_element080  label="H_element : 042"  # scripted group (container) (typed FeaturePython)
  n = 8
  ref = H_element
FEATURE [App::DocumentObjectGroupPython] G4_POLYSTYRENE  # scripted group (container) (typed FeaturePython)
  Dunit = g/cm3
  Dvalue = 1.06
  Group = -> [C_element086,H_element080]
  conduct = 2
  density = 1
  expand = 3
  formula = G4_POLYSTYRENE
  name = G4_POLYSTYRENE
  specific = 4
FEATURE [App::DocumentObjectGroupPython] C_element087  label="C_element : 045"  # scripted group (container) (typed FeaturePython)
  n = 2
  ref = C_element
FEATURE [App::DocumentObjectGroupPython] F_element014  label="F_element : 4"  # scripted group (container) (typed FeaturePython)
  n = 4
  ref = F_element
FEATURE [App::DocumentObjectGroupPython] G4_TEFLON  # scripted group (container) (typed FeaturePython)
  Dunit = g/cm3
  Dvalue = 2.2
  Group = -> [C_element087,F_element014]
  conduct = 2
  density = 1
  expand = 3
  formula = G4_TEFLON
  name = G4_TEFLON
  specific = 4
FEATURE [App::DocumentObjectGroupPython] C_element088  label="C_element : 046"  # scripted group (container) (typed FeaturePython)
  n = 2
  ref = C_element
FEATURE [App::DocumentObjectGroupPython] F_element015  label="F_element : 006"  # scripted group (container) (typed FeaturePython)
  n = 3
  ref = F_element
FEATURE [App::DocumentObjectGroupPython] Cl_element018  label="Cl_element : 008"  # scripted group (container) (typed FeaturePython)
  n = 1
  ref = Cl_element
FEATURE [App::DocumentObjectGroupPython] G4_POLYTRIFLUOROCHLOROETHYLENE  # scripted group (container) (typed FeaturePython)
  Dunit = g/cm3
  Dvalue = 2.1
  Group = -> [C_element088,F_element015,Cl_element018]
  conduct = 2
  density = 1
  expand = 3
  formula = G4_POLYTRIFLUOROCHLOROETHYLENE
  name = G4_POLYTRIFLUOROCHLOROETHYLENE
  specific = 4
FEATURE [App::DocumentObjectGroupPython] C_element089  label="C_element : 047"  # scripted group (container) (typed FeaturePython)
  n = 4
  ref = C_element
FEATURE [App::DocumentObjectGroupPython] H_element081  label="H_element : 043"  # scripted group (container) (typed FeaturePython)
  n = 6
  ref = H_element
FEATURE [App::DocumentObjectGroupPython] O_element081  label="O_element : 042"  # scripted group (container) (typed FeaturePython)
  n = 2
  ref = O_element
FEATURE [App::DocumentObjectGroupPython] G4_POLYVINYL_ACETATE  # scripted group (container) (typed FeaturePython)
  Dunit = g/cm3
  Dvalue = 1.19
  Group = -> [C_element089,H_element081,O_element081]
  conduct = 2
  density = 1
  expand = 3
  formula = G4_POLYVINYL_ACETATE
  name = G4_POLYVINYL_ACETATE
  specific = 4
FEATURE [App::DocumentObjectGroupPython] C_element090  label="C_element : 048"  # scripted group (container) (typed FeaturePython)
  n = 2
  ref = C_element
FEATURE [App::DocumentObjectGroupPython] H_element082  label="H_element : 044"  # scripted group (container) (typed FeaturePython)
  n = 4
  ref = H_element
FEATURE [App::DocumentObjectGroupPython] O_element082  label="O_element : 043"  # scripted group (container) (typed FeaturePython)
  n = 1
  ref = O_element
FEATURE [App::DocumentObjectGroupPython] G4_POLYVINYL_ALCOHOL  # scripted group (container) (typed FeaturePython)
  Dunit = g/cm3
  Dvalue = 1.3
  Group = -> [C_element090,H_element082,O_element082]
  conduct = 2
  density = 1
  expand = 3
  formula = G4_POLYVINYL_ALCOHOL
  name = G4_POLYVINYL_ALCOHOL
  specific = 4
FEATURE [App::DocumentObjectGroupPython] C_element091  label="C_element : 049"  # scripted group (container) (typed FeaturePython)
  n = 8
  ref = C_element
FEATURE [App::DocumentObjectGroupPython] H_element083  label="H_element : 045"  # scripted group (container) (typed FeaturePython)
  n = 14
  ref = H_element
FEATURE [App::DocumentObjectGroupPython] O_element083  label="O_element : 044"  # scripted group (container) (typed FeaturePython)
  n = 2
  ref = O_element
FEATURE [App::DocumentObjectGroupPython] G4_POLYVINYL_BUTYRAL  # scripted group (container) (typed FeaturePython)
  Dunit = g/cm3
  Dvalue = 1.12
  Group = -> [C_element091,H_element083,O_element083]
  conduct = 2
  density = 1
  expand = 3
  formula = G4_POLYVINYL_BUTYRAL
  name = G4_POLYVINYL_BUTYRAL
  specific = 4
FEATURE [App::DocumentObjectGroupPython] C_element092  label="C_element : 050"  # scripted group (container) (typed FeaturePython)
  n = 2
  ref = C_element
FEATURE [App::DocumentObjectGroupPython] H_element084  label="H_element : 046"  # scripted group (container) (typed FeaturePython)
  n = 3
  ref = H_element
FEATURE [App::DocumentObjectGroupPython] Cl_element019  label="Cl_element : 009"  # scripted group (container) (typed FeaturePython)
  n = 1
  ref = Cl_element
FEATURE [App::DocumentObjectGroupPython] G4_POLYVINYL_CHLORIDE  # scripted group (container) (typed FeaturePython)
  Dunit = g/cm3
  Dvalue = 1.3
  Group = -> [C_element092,H_element084,Cl_element019]
  conduct = 2
  density = 1
  expand = 3
  formula = G4_POLYVINYL_CHLORIDE
  name = G4_POLYVINYL_CHLORIDE
  specific = 4
FEATURE [App::DocumentObjectGroupPython] C_element093  label="C_element : 051"  # scripted group (container) (typed FeaturePython)
  n = 2
  ref = C_element
FEATURE [App::DocumentObjectGroupPython] H_element085  label="H_element : 047"  # scripted group (container) (typed FeaturePython)
  n = 2
  ref = H_element
FEATURE [App::DocumentObjectGroupPython] Cl_element020  label="Cl_element : 010"  # scripted group (container) (typed FeaturePython)
  n = 2
  ref = Cl_element
FEATURE [App::DocumentObjectGroupPython] G4_POLYVINYLIDENE_CHLORIDE  # scripted group (container) (typed FeaturePython)
  Dunit = g/cm3
  Dvalue = 1.7
  Group = -> [C_element093,H_element085,Cl_element020]
  conduct = 2
  density = 1
  expand = 3
  formula = G4_POLYVINYLIDENE_CHLORIDE
  name = G4_POLYVINYLIDENE_CHLORIDE
  specific = 4
FEATURE [App::DocumentObjectGroupPython] C_element094  label="C_element : 052"  # scripted group (container) (typed FeaturePython)
  n = 2
  ref = C_element
FEATURE [App::DocumentObjectGroupPython] H_element086  label="H_element : 048"  # scripted group (container) (typed FeaturePython)
  n = 2
  ref = H_element
FEATURE [App::DocumentObjectGroupPython] F_element016  label="F_element : 007"  # scripted group (container) (typed FeaturePython)
  n = 2
  ref = F_element
FEATURE [App::DocumentObjectGroupPython] G4_POLYVINYLIDENE_FLUORIDE  # scripted group (container) (typed FeaturePython)
  Dunit = g/cm3
  Dvalue = 1.76
  Group = -> [C_element094,H_element086,F_element016]
  conduct = 2
  density = 1
  expand = 3
  formula = G4_POLYVINYLIDENE_FLUORIDE
  name = G4_POLYVINYLIDENE_FLUORIDE
  specific = 4
FEATURE [App::DocumentObjectGroupPython] C_element095  label="C_element : 053"  # scripted group (container) (typed FeaturePython)
  n = 6
  ref = C_element
FEATURE [App::DocumentObjectGroupPython] H_element087  label="H_element : 9"  # scripted group (container) (typed FeaturePython)
  n = 9
  ref = H_element
FEATURE [App::DocumentObjectGroupPython] N_element037  label="N_element : 016"  # scripted group (container) (typed FeaturePython)
  n = 1
  ref = N_element
FEATURE [App::DocumentObjectGroupPython] O_element084  label="O_element : 045"  # scripted group (container) (typed FeaturePython)
  n = 1
  ref = O_element
FEATURE [App::DocumentObjectGroupPython] G4_POLYVINYL_PYRROLIDONE  # scripted group (container) (typed FeaturePython)
  Dunit = g/cm3
  Dvalue = 1.25
  Group = -> [C_element095,H_element087,N_element037,O_element084]
  conduct = 2
  density = 1
  expand = 3
  formula = G4_POLYVINYL_PYRROLIDONE
  name = G4_POLYVINYL_PYRROLIDONE
  specific = 4
FEATURE [App::DocumentObjectGroupPython] K_element008  label="K_element : 1"  # scripted group (container) (typed FeaturePython)
  n = 1
  ref = K_element
FEATURE [App::DocumentObjectGroupPython] I_element006  label="I_element : 003"  # scripted group (container) (typed FeaturePython)
  n = 1
  ref = I_element
FEATURE [App::DocumentObjectGroupPython] G4_POTASSIUM_IODIDE  # scripted group (container) (typed FeaturePython)
  Dunit = g/cm3
  Dvalue = 3.13
  Group = -> [K_element008,I_element006]
  conduct = 2
  density = 1
  expand = 3
  formula = G4_POTASSIUM_IODIDE
  name = G4_POTASSIUM_IODIDE
  specific = 4
FEATURE [App::DocumentObjectGroupPython] K_element009  label="K_element : 2"  # scripted group (container) (typed FeaturePython)
  n = 2
  ref = K_element
FEATURE [App::DocumentObjectGroupPython] O_element085  label="O_element : 046"  # scripted group (container) (typed FeaturePython)
  n = 1
  ref = O_element
FEATURE [App::DocumentObjectGroupPython] G4_POTASSIUM_OXIDE  # scripted group (container) (typed FeaturePython)
  Dunit = g/cm3
  Dvalue = 2.32
  Group = -> [K_element009,O_element085]
  conduct = 2
  density = 1
  expand = 3
  formula = G4_POTASSIUM_OXIDE
  name = G4_POTASSIUM_OXIDE
  specific = 4
FEATURE [App::DocumentObjectGroupPython] C_element096  label="C_element : 054"  # scripted group (container) (typed FeaturePython)
  n = 3
  ref = C_element
FEATURE [App::DocumentObjectGroupPython] H_element088  label="H_element : 049"  # scripted group (container) (typed FeaturePython)
  n = 8
  ref = H_element
FEATURE [App::DocumentObjectGroupPython] G4_PROPANE  # scripted group (container) (typed FeaturePython)
  Dunit = g/cm3
  Dvalue = 0.00187939
  Group = -> [C_element096,H_element088]
  conduct = 2
  density = 1
  expand = 3
  formula = G4_PROPANE
  name = G4_PROPANE
  specific = 4
FEATURE [App::DocumentObjectGroupPython] C_element097  label="C_element : 055"  # scripted group (container) (typed FeaturePython)
  n = 3
  ref = C_element
FEATURE [App::DocumentObjectGroupPython] H_element089  label="H_element : 050"  # scripted group (container) (typed FeaturePython)
  n = 8
  ref = H_element
FEATURE [App::DocumentObjectGroupPython] G4_lPROPANE  # scripted group (container) (typed FeaturePython)
  Dunit = g/cm3
  Dvalue = 0.43
  Group = -> [C_element097,H_element089]
  conduct = 2
  density = 1
  expand = 3
  formula = G4_lPROPANE
  name = G4_lPROPANE
  specific = 4
FEATURE [App::DocumentObjectGroupPython] C_element098  label="C_element : 056"  # scripted group (container) (typed FeaturePython)
  n = 3
  ref = C_element
FEATURE [App::DocumentObjectGroupPython] H_element090  label="H_element : 051"  # scripted group (container) (typed FeaturePython)
  n = 8
  ref = H_element
FEATURE [App::DocumentObjectGroupPython] O_element086  label="O_element : 047"  # scripted group (container) (typed FeaturePython)
  n = 1
  ref = O_element
FEATURE [App::DocumentObjectGroupPython] G4_N_PROPYL_ALCOHOL  label="G4_N-PROPYL_ALCOHOL"  # scripted group (container) (typed FeaturePython)
  Dunit = g/cm3
  Dvalue = 0.8035
  Group = -> [C_element098,H_element090,O_element086]
  conduct = 2
  density = 1
  expand = 3
  formula = G4_N-PROPYL_ALCOHOL
  name = G4_N-PROPYL_ALCOHOL
  specific = 4
FEATURE [App::DocumentObjectGroupPython] C_element099  label="C_element : 057"  # scripted group (container) (typed FeaturePython)
  n = 5
  ref = C_element
FEATURE [App::DocumentObjectGroupPython] H_element091  label="H_element : 052"  # scripted group (container) (typed FeaturePython)
  n = 5
  ref = H_element
FEATURE [App::DocumentObjectGroupPython] N_element038  label="N_element : 017"  # scripted group (container) (typed FeaturePython)
  n = 1
  ref = N_element
FEATURE [App::DocumentObjectGroupPython] G4_PYRIDINE  # scripted group (container) (typed FeaturePython)
  Dunit = g/cm3
  Dvalue = 0.9819
  Group = -> [C_element099,H_element091,N_element038]
  conduct = 2
  density = 1
  expand = 3
  formula = G4_PYRIDINE
  name = G4_PYRIDINE
  specific = 4
FEATURE [App::DocumentObjectGroupPython] H_element092  label="H_element : 0.144"  # scripted group (container) (typed FeaturePython)
  n = 0.143711
FEATURE [App::DocumentObjectGroupPython] C_element100  label="C_element : 0.856"  # scripted group (container) (typed FeaturePython)
  n = 0.856289
FEATURE [App::DocumentObjectGroupPython] G4_RUBBER_BUTYL  # scripted group (container) (typed FeaturePython)
  Dunit = g/cm3
  Dvalue = 0.92
  Group = -> [H_element092,C_element100]
  conduct = 2
  density = 1
  expand = 3
  formula = G4_RUBBER_BUTYL
  name = G4_RUBBER_BUTYL
  specific = 4
FEATURE [App::DocumentObjectGroupPython] H_element093  label="H_element : 0.118"  # scripted group (container) (typed FeaturePython)
  n = 0.118371
FEATURE [App::DocumentObjectGroupPython] C_element101  label="C_element : 0.882"  # scripted group (container) (typed FeaturePython)
  n = 0.881629
FEATURE [App::DocumentObjectGroupPython] G4_RUBBER_NATURAL  # scripted group (container) (typed FeaturePython)
  Dunit = g/cm3
  Dvalue = 0.92
  Group = -> [H_element093,C_element101]
  conduct = 2
  density = 1
  expand = 3
  formula = G4_RUBBER_NATURAL
  name = G4_RUBBER_NATURAL
  specific = 4
FEATURE [App::DocumentObjectGroupPython] H_element094  label="H_element : 0.145"  # scripted group (container) (typed FeaturePython)
  n = 0.05692
FEATURE [App::DocumentObjectGroupPython] C_element102  label="C_element : 0.543"  # scripted group (container) (typed FeaturePython)
  n = 0.542646
FEATURE [App::DocumentObjectGroupPython] Cl_element021  label="Cl_element : 0.400"  # scripted group (container) (typed FeaturePython)
  n = 0.400434
FEATURE [App::DocumentObjectGroupPython] G4_RUBBER_NEOPRENE  # scripted group (container) (typed FeaturePython)
  Dunit = g/cm3
  Dvalue = 1.23
  Group = -> [H_element094,C_element102,Cl_element021]
  conduct = 2
  density = 1
  expand = 3
  formula = G4_RUBBER_NEOPRENE
  name = G4_RUBBER_NEOPRENE
  specific = 4
FEATURE [App::DocumentObjectGroupPython] Si_element006  label="Si_element : 1"  # scripted group (container) (typed FeaturePython)
  n = 1
  ref = Si_element
FEATURE [App::DocumentObjectGroupPython] O_element087  label="O_element : 048"  # scripted group (container) (typed FeaturePython)
  n = 2
  ref = O_element
FEATURE [App::DocumentObjectGroupPython] G4_SILICON_DIOXIDE  # scripted group (container) (typed FeaturePython)
  Dunit = g/cm3
  Dvalue = 2.32
  Group = -> [Si_element006,O_element087]
  conduct = 2
  density = 1
  expand = 3
  formula = G4_SILICON_DIOXIDE
  name = G4_SILICON_DIOXIDE
  specific = 4
FEATURE [App::DocumentObjectGroupPython] Ag_element002  label="Ag_element : 1"  # scripted group (container) (typed FeaturePython)
  n = 1
  ref = Ag_element
FEATURE [App::DocumentObjectGroupPython] Br_element005  label="Br_element : 003"  # scripted group (container) (typed FeaturePython)
  n = 1
  ref = Br_element
FEATURE [App::DocumentObjectGroupPython] G4_SILVER_BROMIDE  # scripted group (container) (typed FeaturePython)
  Dunit = g/cm3
  Dvalue = 6.473
  Group = -> [Ag_element002,Br_element005]
  conduct = 2
  density = 1
  expand = 3
  formula = G4_SILVER_BROMIDE
  name = G4_SILVER_BROMIDE
  specific = 4
FEATURE [App::DocumentObjectGroupPython] Ag_element003  label="Ag_element : 002"  # scripted group (container) (typed FeaturePython)
  n = 1
  ref = Ag_element
FEATURE [App::DocumentObjectGroupPython] Cl_element022  label="Cl_element : 011"  # scripted group (container) (typed FeaturePython)
  n = 1
  ref = Cl_element
FEATURE [App::DocumentObjectGroupPython] G4_SILVER_CHLORIDE  # scripted group (container) (typed FeaturePython)
  Dunit = g/cm3
  Dvalue = 5.56
  Group = -> [Ag_element003,Cl_element022]
  conduct = 2
  density = 1
  expand = 3
  formula = G4_SILVER_CHLORIDE
  name = G4_SILVER_CHLORIDE
  specific = 4
FEATURE [App::DocumentObjectGroupPython] Br_element006  label="Br_element : 0.423"  # scripted group (container) (typed FeaturePython)
  n = 0.422895
FEATURE [App::DocumentObjectGroupPython] Ag_element004  label="Ag_element : 0.574"  # scripted group (container) (typed FeaturePython)
  n = 0.573748
FEATURE [App::DocumentObjectGroupPython] I_element007  label="I_element : 0.649"  # scripted group (container) (typed FeaturePython)
  n = 0.003357
FEATURE [App::DocumentObjectGroupPython] G4_SILVER_HALIDES  # scripted group (container) (typed FeaturePython)
  Dunit = g/cm3
  Dvalue = 6.47
  Group = -> [Br_element006,Ag_element004,I_element007]
  conduct = 2
  density = 1
  expand = 3
  formula = G4_SILVER_HALIDES
  name = G4_SILVER_HALIDES
  specific = 4
FEATURE [App::DocumentObjectGroupPython] Ag_element005  label="Ag_element : 003"  # scripted group (container) (typed FeaturePython)
  n = 1
  ref = Ag_element
FEATURE [App::DocumentObjectGroupPython] I_element008  label="I_element : 004"  # scripted group (container) (typed FeaturePython)
  n = 1
  ref = I_element
FEATURE [App::DocumentObjectGroupPython] G4_SILVER_IODIDE  # scripted group (container) (typed FeaturePython)
  Dunit = g/cm3
  Dvalue = 6.01
  Group = -> [Ag_element005,I_element008]
  conduct = 2
  density = 1
  expand = 3
  formula = G4_SILVER_IODIDE
  name = G4_SILVER_IODIDE
  specific = 4
FEATURE [App::DocumentObjectGroupPython] H_element095  label="H_element : 0.100"  # scripted group (container) (typed FeaturePython)
  n = 0.1
FEATURE [App::DocumentObjectGroupPython] C_element103  label="C_element : 0.204"  # scripted group (container) (typed FeaturePython)
  n = 0.204
FEATURE [App::DocumentObjectGroupPython] N_element039  label="N_element : 0.759"  # scripted group (container) (typed FeaturePython)
  n = 0.042
FEATURE [App::DocumentObjectGroupPython] O_element088  label="O_element : 0.645"  # scripted group (container) (typed FeaturePython)
  n = 0.645
FEATURE [App::DocumentObjectGroupPython] Na_element013  label="Na_element : 0.100"  # scripted group (container) (typed FeaturePython)
  n = 0.002
FEATURE [App::DocumentObjectGroupPython] P_element009  label="P_element : 0.107"  # scripted group (container) (typed FeaturePython)
  n = 0.001
FEATURE [App::DocumentObjectGroupPython] S_element020  label="S_element : 0.021"  # scripted group (container) (typed FeaturePython)
  n = 0.002
FEATURE [App::DocumentObjectGroupPython] Cl_element023  label="Cl_element : 0.590"  # scripted group (container) (typed FeaturePython)
  n = 0.003
FEATURE [App::DocumentObjectGroupPython] K_element010  label="K_element : 0.001"  # scripted group (container) (typed FeaturePython)
  n = 0.001
FEATURE [App::DocumentObjectGroupPython] G4_SKIN_ICRP  # scripted group (container) (typed FeaturePython)
  Dunit = g/cm3
  Dvalue = 1.09
  Group = -> [H_element095,C_element103,N_element039,O_element088,Na_element013,P_element009,S_element020,Cl_element023,K_element010]
  conduct = 2
  density = 1
  expand = 3
  formula = G4_SKIN_ICRP
  name = G4_SKIN_ICRP
  specific = 4
FEATURE [App::DocumentObjectGroupPython] Na_element014  label="Na_element : 2"  # scripted group (container) (typed FeaturePython)
  n = 2
  ref = Na_element
FEATURE [App::DocumentObjectGroupPython] C_element104  label="C_element : 058"  # scripted group (container) (typed FeaturePython)
  n = 1
  ref = C_element
FEATURE [App::DocumentObjectGroupPython] O_element089  label="O_element : 049"  # scripted group (container) (typed FeaturePython)
  n = 3
  ref = O_element
FEATURE [App::DocumentObjectGroupPython] G4_SODIUM_CARBONATE  # scripted group (container) (typed FeaturePython)
  Dunit = g/cm3
  Dvalue = 2.532
  Group = -> [Na_element014,C_element104,O_element089]
  conduct = 2
  density = 1
  expand = 3
  formula = G4_SODIUM_CARBONATE
  name = G4_SODIUM_CARBONATE
  specific = 4
FEATURE [App::DocumentObjectGroupPython] Na_element015  label="Na_element : 1"  # scripted group (container) (typed FeaturePython)
  n = 1
  ref = Na_element
FEATURE [App::DocumentObjectGroupPython] I_element009  label="I_element : 005"  # scripted group (container) (typed FeaturePython)
  n = 1
  ref = I_element
FEATURE [App::DocumentObjectGroupPython] G4_SODIUM_IODIDE  # scripted group (container) (typed FeaturePython)
  Dunit = g/cm3
  Dvalue = 3.667
  Group = -> [Na_element015,I_element009]
  conduct = 2
  density = 1
  expand = 3
  formula = G4_SODIUM_IODIDE
  name = G4_SODIUM_IODIDE
  specific = 4
FEATURE [App::DocumentObjectGroupPython] Na_element016  label="Na_element : 003"  # scripted group (container) (typed FeaturePython)
  n = 2
  ref = Na_element
FEATURE [App::DocumentObjectGroupPython] O_element090  label="O_element : 050"  # scripted group (container) (typed FeaturePython)
  n = 1
  ref = O_element
FEATURE [App::DocumentObjectGroupPython] G4_SODIUM_MONOXIDE  # scripted group (container) (typed FeaturePython)
  Dunit = g/cm3
  Dvalue = 2.27
  Group = -> [Na_element016,O_element090]
  conduct = 2
  density = 1
  expand = 3
  formula = G4_SODIUM_MONOXIDE
  name = G4_SODIUM_MONOXIDE
  specific = 4
FEATURE [App::DocumentObjectGroupPython] Na_element017  label="Na_element : 004"  # scripted group (container) (typed FeaturePython)
  n = 1
  ref = Na_element
FEATURE [App::DocumentObjectGroupPython] N_element040  label="N_element : 018"  # scripted group (container) (typed FeaturePython)
  n = 1
  ref = N_element
FEATURE [App::DocumentObjectGroupPython] O_element091  label="O_element : 051"  # scripted group (container) (typed FeaturePython)
  n = 3
  ref = O_element
FEATURE [App::DocumentObjectGroupPython] G4_SODIUM_NITRATE  # scripted group (container) (typed FeaturePython)
  Dunit = g/cm3
  Dvalue = 2.261
  Group = -> [Na_element017,N_element040,O_element091]
  conduct = 2
  density = 1
  expand = 3
  formula = G4_SODIUM_NITRATE
  name = G4_SODIUM_NITRATE
  specific = 4
FEATURE [App::DocumentObjectGroupPython] C_element105  label="C_element : 059"  # scripted group (container) (typed FeaturePython)
  n = 14
  ref = C_element
FEATURE [App::DocumentObjectGroupPython] H_element096  label="H_element : 053"  # scripted group (container) (typed FeaturePython)
  n = 12
  ref = H_element
FEATURE [App::DocumentObjectGroupPython] G4_STILBENE  # scripted group (container) (typed FeaturePython)
  Dunit = g/cm3
  Dvalue = 0.9707
  Group = -> [C_element105,H_element096]
  conduct = 2
  density = 1
  expand = 3
  formula = G4_STILBENE
  name = G4_STILBENE
  specific = 4
FEATURE [App::DocumentObjectGroupPython] C_element106  label="C_element : 12"  # scripted group (container) (typed FeaturePython)
  n = 12
  ref = C_element
FEATURE [App::DocumentObjectGroupPython] H_element097  label="H_element : 22"  # scripted group (container) (typed FeaturePython)
  n = 22
  ref = H_element
FEATURE [App::DocumentObjectGroupPython] O_element092  label="O_element : 11"  # scripted group (container) (typed FeaturePython)
  n = 11
  ref = O_element
FEATURE [App::DocumentObjectGroupPython] G4_SUCROSE  # scripted group (container) (typed FeaturePython)
  Dunit = g/cm3
  Dvalue = 1.5805
  Group = -> [C_element106,H_element097,O_element092]
  conduct = 2
  density = 1
  expand = 3
  formula = G4_SUCROSE
  name = G4_SUCROSE
  specific = 4
FEATURE [App::DocumentObjectGroupPython] C_element107  label="C_element : 18"  # scripted group (container) (typed FeaturePython)
  n = 18
  ref = C_element
FEATURE [App::DocumentObjectGroupPython] H_element098  label="H_element : 054"  # scripted group (container) (typed FeaturePython)
  n = 14
  ref = H_element
FEATURE [App::DocumentObjectGroupPython] G4_TERPHENYL  # scripted group (container) (typed FeaturePython)
  Dunit = g/cm3
  Dvalue = 1.24
  Group = -> [C_element107,H_element098]
  conduct = 2
  density = 1
  expand = 3
  formula = G4_TERPHENYL
  name = G4_TERPHENYL
  specific = 4
FEATURE [App::DocumentObjectGroupPython] H_element099  label="H_element : 0.146"  # scripted group (container) (typed FeaturePython)
  n = 0.106
FEATURE [App::DocumentObjectGroupPython] C_element108  label="C_element : 0.883"  # scripted group (container) (typed FeaturePython)
  n = 0.099
FEATURE [App::DocumentObjectGroupPython] N_element041  label="N_element : 0.020"  # scripted group (container) (typed FeaturePython)
  n = 0.02
FEATURE [App::DocumentObjectGroupPython] O_element093  label="O_element : 0.766"  # scripted group (container) (typed FeaturePython)
  n = 0.766
FEATURE [App::DocumentObjectGroupPython] Na_element018  label="Na_element : 0.101"  # scripted group (container) (typed FeaturePython)
  n = 0.002
FEATURE [App::DocumentObjectGroupPython] P_element010  label="P_element : 0.108"  # scripted group (container) (typed FeaturePython)
  n = 0.001
FEATURE [App::DocumentObjectGroupPython] S_element021  label="S_element : 0.022"  # scripted group (container) (typed FeaturePython)
  n = 0.002
FEATURE [App::DocumentObjectGroupPython] Cl_element024  label="Cl_element : 0.002"  # scripted group (container) (typed FeaturePython)
  n = 0.002
FEATURE [App::DocumentObjectGroupPython] K_element011  label="K_element : 0.017"  # scripted group (container) (typed FeaturePython)
  n = 0.002
FEATURE [App::DocumentObjectGroupPython] G4_TESTIS_ICRP  # scripted group (container) (typed FeaturePython)
  Dunit = g/cm3
  Dvalue = 1.04
  Group = -> [H_element099,C_element108,N_element041,O_element093,Na_element018,P_element010,S_element021,Cl_element024,K_element011]
  conduct = 2
  density = 1
  expand = 3
  formula = G4_TESTIS_ICRP
  name = G4_TESTIS_ICRP
  specific = 4
FEATURE [App::DocumentObjectGroupPython] C_element109  label="C_element : 060"  # scripted group (container) (typed FeaturePython)
  n = 2
  ref = C_element
FEATURE [App::DocumentObjectGroupPython] Cl_element025  label="Cl_element : 012"  # scripted group (container) (typed FeaturePython)
  n = 4
  ref = Cl_element
FEATURE [App::DocumentObjectGroupPython] G4_TETRACHLOROETHYLENE  # scripted group (container) (typed FeaturePython)
  Dunit = g/cm3
  Dvalue = 1.625
  Group = -> [C_element109,Cl_element025]
  conduct = 2
  density = 1
  expand = 3
  formula = G4_TETRACHLOROETHYLENE
  name = G4_TETRACHLOROETHYLENE
  specific = 4
FEATURE [App::DocumentObjectGroupPython] Tl_element001  label="Tl_element : 1"  # scripted group (container) (typed FeaturePython)
  n = 1
  ref = Tl_element
FEATURE [App::DocumentObjectGroupPython] Cl_element026  label="Cl_element : 013"  # scripted group (container) (typed FeaturePython)
  n = 1
  ref = Cl_element
FEATURE [App::DocumentObjectGroupPython] G4_THALLIUM_CHLORIDE  # scripted group (container) (typed FeaturePython)
  Dunit = g/cm3
  Dvalue = 7.004
  Group = -> [Tl_element001,Cl_element026]
  conduct = 2
  density = 1
  expand = 3
  formula = G4_THALLIUM_CHLORIDE
  name = G4_THALLIUM_CHLORIDE
  specific = 4
FEATURE [App::DocumentObjectGroupPython] H_element100  label="H_element : 0.147"  # scripted group (container) (typed FeaturePython)
  n = 0.105
FEATURE [App::DocumentObjectGroupPython] C_element110  label="C_element : 0.256"  # scripted group (container) (typed FeaturePython)
  n = 0.256
FEATURE [App::DocumentObjectGroupPython] N_element042  label="N_element : 0.760"  # scripted group (container) (typed FeaturePython)
  n = 0.027
FEATURE [App::DocumentObjectGroupPython] O_element094  label="O_element : 0.602"  # scripted group (container) (typed FeaturePython)
  n = 0.602
FEATURE [App::DocumentObjectGroupPython] Na_element019  label="Na_element : 0.102"  # scripted group (container) (typed FeaturePython)
  n = 0.001
FEATURE [App::DocumentObjectGroupPython] P_element011  label="P_element : 0.109"  # scripted group (container) (typed FeaturePython)
  n = 0.002
FEATURE [App::DocumentObjectGroupPython] S_element022  label="S_element : 0.023"  # scripted group (container) (typed FeaturePython)
  n = 0.003
FEATURE [App::DocumentObjectGroupPython] Cl_element027  label="Cl_element : 0.591"  # scripted group (container) (typed FeaturePython)
  n = 0.002
FEATURE [App::DocumentObjectGroupPython] K_element012  label="K_element : 0.018"  # scripted group (container) (typed FeaturePython)
  n = 0.002
FEATURE [App::DocumentObjectGroupPython] G4_TISSUE_SOFT_ICRP  # scripted group (container) (typed FeaturePython)
  Dunit = g/cm3
  Dvalue = 1.03
  Group = -> [H_element100,C_element110,N_element042,O_element094,Na_element019,P_element011,S_element022,Cl_element027,K_element012]
  conduct = 2
  density = 1
  expand = 3
  formula = G4_TISSUE_SOFT_ICRP
  name = G4_TISSUE_SOFT_ICRP
  specific = 4
FEATURE [App::DocumentObjectGroupPython] H_element101  label="H_element : 0.148"  # scripted group (container) (typed FeaturePython)
  n = 0.101
FEATURE [App::DocumentObjectGroupPython] C_element111  label="C_element : 0.111"  # scripted group (container) (typed FeaturePython)
  n = 0.111
FEATURE [App::DocumentObjectGroupPython] N_element043  label="N_element : 0.026"  # scripted group (container) (typed FeaturePython)
  n = 0.026
FEATURE [App::DocumentObjectGroupPython] O_element095  label="O_element : 0.762"  # scripted group (container) (typed FeaturePython)
  n = 0.762
FEATURE [App::DocumentObjectGroupPython] G4_TISSUE_SOFT_ICRU_4  label="G4_TISSUE_SOFT_ICRU-4"  # scripted group (container) (typed FeaturePython)
  Dunit = g/cm3
  Dvalue = 1
  Group = -> [H_element101,C_element111,N_element043,O_element095]
  conduct = 2
  density = 1
  expand = 3
  formula = G4_TISSUE_SOFT_ICRU-4
  name = G4_TISSUE_SOFT_ICRU-4
  specific = 4
FEATURE [App::DocumentObjectGroupPython] H_element102  label="H_element : 0.149"  # scripted group (container) (typed FeaturePython)
  n = 0.101869
FEATURE [App::DocumentObjectGroupPython] C_element112  label="C_element : 0.456"  # scripted group (container) (typed FeaturePython)
  n = 0.456179
FEATURE [App::DocumentObjectGroupPython] N_element044  label="N_element : 0.761"  # scripted group (container) (typed FeaturePython)
  n = 0.035172
FEATURE [App::DocumentObjectGroupPython] O_element096  label="O_element : 0.407"  # scripted group (container) (typed FeaturePython)
  n = 0.40678
FEATURE [App::DocumentObjectGroupPython] G4_TISSUE_METHANE  label="G4_TISSUE-METHANE"  # scripted group (container) (typed FeaturePython)
  Dunit = g/cm3
  Dvalue = 0.00106409
  Group = -> [H_element102,C_element112,N_element044,O_element096]
  conduct = 2
  density = 1
  expand = 3
  formula = G4_TISSUE-METHANE
  name = G4_TISSUE-METHANE
  specific = 4
FEATURE [App::DocumentObjectGroupPython] H_element103  label="H_element : 0.103"  # scripted group (container) (typed FeaturePython)
  n = 0.102672
FEATURE [App::DocumentObjectGroupPython] C_element113  label="C_element : 0.569"  # scripted group (container) (typed FeaturePython)
  n = 0.56894
FEATURE [App::DocumentObjectGroupPython] N_element045  label="N_element : 0.762"  # scripted group (container) (typed FeaturePython)
  n = 0.035022
FEATURE [App::DocumentObjectGroupPython] O_element097  label="O_element : 0.293"  # scripted group (container) (typed FeaturePython)
  n = 0.293366
FEATURE [App::DocumentObjectGroupPython] G4_TISSUE_PROPANE  label="G4_TISSUE-PROPANE"  # scripted group (container) (typed FeaturePython)
  Dunit = g/cm3
  Dvalue = 0.00182628
  Group = -> [H_element103,C_element113,N_element045,O_element097]
  conduct = 2
  density = 1
  expand = 3
  formula = G4_TISSUE-PROPANE
  name = G4_TISSUE-PROPANE
  specific = 4
FEATURE [App::DocumentObjectGroupPython] Ti_element003  label="Ti_element : 1"  # scripted group (container) (typed FeaturePython)
  n = 1
  ref = Ti_element
FEATURE [App::DocumentObjectGroupPython] O_element098  label="O_element : 052"  # scripted group (container) (typed FeaturePython)
  n = 2
  ref = O_element
FEATURE [App::DocumentObjectGroupPython] G4_TITANIUM_DIOXIDE  # scripted group (container) (typed FeaturePython)
  Dunit = g/cm3
  Dvalue = 4.26
  Group = -> [Ti_element003,O_element098]
  conduct = 2
  density = 1
  expand = 3
  formula = G4_TITANIUM_DIOXIDE
  name = G4_TITANIUM_DIOXIDE
  specific = 4
FEATURE [App::DocumentObjectGroupPython] C_element114  label="C_element : 061"  # scripted group (container) (typed FeaturePython)
  n = 7
  ref = C_element
FEATURE [App::DocumentObjectGroupPython] H_element104  label="H_element : 055"  # scripted group (container) (typed FeaturePython)
  n = 8
  ref = H_element
FEATURE [App::DocumentObjectGroupPython] G4_TOLUENE  # scripted group (container) (typed FeaturePython)
  Dunit = g/cm3
  Dvalue = 0.8669
  Group = -> [C_element114,H_element104]
  conduct = 2
  density = 1
  expand = 3
  formula = G4_TOLUENE
  name = G4_TOLUENE
  specific = 4
FEATURE [App::DocumentObjectGroupPython] C_element115  label="C_element : 062"  # scripted group (container) (typed FeaturePython)
  n = 2
  ref = C_element
FEATURE [App::DocumentObjectGroupPython] H_element105  label="H_element : 056"  # scripted group (container) (typed FeaturePython)
  n = 1
  ref = H_element
FEATURE [App::DocumentObjectGroupPython] Cl_element028  label="Cl_element : 014"  # scripted group (container) (typed FeaturePython)
  n = 3
  ref = Cl_element
FEATURE [App::DocumentObjectGroupPython] G4_TRICHLOROETHYLENE  # scripted group (container) (typed FeaturePython)
  Dunit = g/cm3
  Dvalue = 1.46
  Group = -> [C_element115,H_element105,Cl_element028]
  conduct = 2
  density = 1
  expand = 3
  formula = G4_TRICHLOROETHYLENE
  name = G4_TRICHLOROETHYLENE
  specific = 4
FEATURE [App::DocumentObjectGroupPython] C_element116  label="C_element : 063"  # scripted group (container) (typed FeaturePython)
  n = 6
  ref = C_element
FEATURE [App::DocumentObjectGroupPython] H_element106  label="H_element : 15"  # scripted group (container) (typed FeaturePython)
  n = 15
  ref = H_element
FEATURE [App::DocumentObjectGroupPython] O_element099  label="O_element : 053"  # scripted group (container) (typed FeaturePython)
  n = 4
  ref = O_element
FEATURE [App::DocumentObjectGroupPython] P_element012  label="P_element : 1"  # scripted group (container) (typed FeaturePython)
  n = 1
  ref = P_element
FEATURE [App::DocumentObjectGroupPython] G4_TRIETHYL_PHOSPHATE  # scripted group (container) (typed FeaturePython)
  Dunit = g/cm3
  Dvalue = 1.07
  Group = -> [C_element116,H_element106,O_element099,P_element012]
  conduct = 2
  density = 1
  expand = 3
  formula = G4_TRIETHYL_PHOSPHATE
  name = G4_TRIETHYL_PHOSPHATE
  specific = 4
FEATURE [App::DocumentObjectGroupPython] W_element003  label="W_element : 003"  # scripted group (container) (typed FeaturePython)
  n = 1
  ref = W_element
FEATURE [App::DocumentObjectGroupPython] F_element017  label="F_element : 6"  # scripted group (container) (typed FeaturePython)
  n = 6
  ref = F_element
FEATURE [App::DocumentObjectGroupPython] G4_TUNGSTEN_HEXAFLUORIDE  # scripted group (container) (typed FeaturePython)
  Dunit = g/cm3
  Dvalue = 2.4
  Group = -> [W_element003,F_element017]
  conduct = 2
  density = 1
  expand = 3
  formula = G4_TUNGSTEN_HEXAFLUORIDE
  name = G4_TUNGSTEN_HEXAFLUORIDE
  specific = 4
FEATURE [App::DocumentObjectGroupPython] U_element001  label="U_element : 1"  # scripted group (container) (typed FeaturePython)
  n = 1
  ref = U_element
FEATURE [App::DocumentObjectGroupPython] C_element117  label="C_element : 064"  # scripted group (container) (typed FeaturePython)
  n = 2
  ref = C_element
FEATURE [App::DocumentObjectGroupPython] G4_URANIUM_DICARBIDE  # scripted group (container) (typed FeaturePython)
  Dunit = g/cm3
  Dvalue = 11.28
  Group = -> [U_element001,C_element117]
  conduct = 2
  density = 1
  expand = 3
  formula = G4_URANIUM_DICARBIDE
  name = G4_URANIUM_DICARBIDE
  specific = 4
FEATURE [App::DocumentObjectGroupPython] U_element002  label="U_element : 002"  # scripted group (container) (typed FeaturePython)
  n = 1
  ref = U_element
FEATURE [App::DocumentObjectGroupPython] C_element118  label="C_element : 065"  # scripted group (container) (typed FeaturePython)
  n = 1
  ref = C_element
FEATURE [App::DocumentObjectGroupPython] G4_URANIUM_MONOCARBIDE  # scripted group (container) (typed FeaturePython)
  Dunit = g/cm3
  Dvalue = 13.63
  Group = -> [U_element002,C_element118]
  conduct = 2
  density = 1
  expand = 3
  formula = G4_URANIUM_MONOCARBIDE
  name = G4_URANIUM_MONOCARBIDE
  specific = 4
FEATURE [App::DocumentObjectGroupPython] U_element003  label="U_element : 003"  # scripted group (container) (typed FeaturePython)
  n = 1
  ref = U_element
FEATURE [App::DocumentObjectGroupPython] O_element100  label="O_element : 054"  # scripted group (container) (typed FeaturePython)
  n = 2
  ref = O_element
FEATURE [App::DocumentObjectGroupPython] G4_URANIUM_OXIDE  # scripted group (container) (typed FeaturePython)
  Dunit = g/cm3
  Dvalue = 10.96
  Group = -> [U_element003,O_element100]
  conduct = 2
  density = 1
  expand = 3
  formula = G4_URANIUM_OXIDE
  name = G4_URANIUM_OXIDE
  specific = 4
FEATURE [App::DocumentObjectGroupPython] C_element119  label="C_element : 066"  # scripted group (container) (typed FeaturePython)
  n = 1
  ref = C_element
FEATURE [App::DocumentObjectGroupPython] H_element107  label="H_element : 057"  # scripted group (container) (typed FeaturePython)
  n = 4
  ref = H_element
FEATURE [App::DocumentObjectGroupPython] N_element046  label="N_element : 019"  # scripted group (container) (typed FeaturePython)
  n = 2
  ref = N_element
FEATURE [App::DocumentObjectGroupPython] O_element101  label="O_element : 055"  # scripted group (container) (typed FeaturePython)
  n = 1
  ref = O_element
FEATURE [App::DocumentObjectGroupPython] G4_UREA  # scripted group (container) (typed FeaturePython)
  Dunit = g/cm3
  Dvalue = 1.323
  Group = -> [C_element119,H_element107,N_element046,O_element101]
  conduct = 2
  density = 1
  expand = 3
  formula = G4_UREA
  name = G4_UREA
  specific = 4
FEATURE [App::DocumentObjectGroupPython] C_element120  label="C_element : 067"  # scripted group (container) (typed FeaturePython)
  n = 5
  ref = C_element
FEATURE [App::DocumentObjectGroupPython] H_element108  label="H_element : 058"  # scripted group (container) (typed FeaturePython)
  n = 11
  ref = H_element
FEATURE [App::DocumentObjectGroupPython] N_element047  label="N_element : 020"  # scripted group (container) (typed FeaturePython)
  n = 1
  ref = N_element
FEATURE [App::DocumentObjectGroupPython] O_element102  label="O_element : 056"  # scripted group (container) (typed FeaturePython)
  n = 2
  ref = O_element
FEATURE [App::DocumentObjectGroupPython] G4_VALINE  # scripted group (container) (typed FeaturePython)
  Dunit = g/cm3
  Dvalue = 1.23
  Group = -> [C_element120,H_element108,N_element047,O_element102]
  conduct = 2
  density = 1
  expand = 3
  formula = G4_VALINE
  name = G4_VALINE
  specific = 4
FEATURE [App::DocumentObjectGroupPython] H_element109  label="H_element : 0.009"  # scripted group (container) (typed FeaturePython)
  n = 0.009417
FEATURE [App::DocumentObjectGroupPython] C_element121  label="C_element : 0.281"  # scripted group (container) (typed FeaturePython)
  n = 0.280555
FEATURE [App::DocumentObjectGroupPython] F_element018  label="F_element : 0.710"  # scripted group (container) (typed FeaturePython)
  n = 0.710028
FEATURE [App::DocumentObjectGroupPython] G4_VITON  # scripted group (container) (typed FeaturePython)
  Dunit = g/cm3
  Dvalue = 1.8
  Group = -> [H_element109,C_element121,F_element018]
  conduct = 2
  density = 1
  expand = 3
  formula = G4_VITON
  name = G4_VITON
  specific = 4
FEATURE [App::DocumentObjectGroupPython] H_element110  label="H_element : 059"  # scripted group (container) (typed FeaturePython)
  n = 2
  ref = H_element
FEATURE [App::DocumentObjectGroupPython] O_element103  label="O_element : 057"  # scripted group (container) (typed FeaturePython)
  n = 1
  ref = O_element
FEATURE [App::DocumentObjectGroupPython] G4_WATER  # scripted group (container) (typed FeaturePython)
  Dunit = g/cm3
  Dvalue = 1
  Group = -> [H_element110,O_element103]
  conduct = 2
  density = 1
  expand = 3
  formula = G4_WATER
  name = G4_WATER
  specific = 4
FEATURE [App::DocumentObjectGroupPython] H_element111  label="H_element : 060"  # scripted group (container) (typed FeaturePython)
  n = 2
  ref = H_element
FEATURE [App::DocumentObjectGroupPython] O_element104  label="O_element : 058"  # scripted group (container) (typed FeaturePython)
  n = 1
  ref = O_element
FEATURE [App::DocumentObjectGroupPython] G4_WATER_VAPOR  # scripted group (container) (typed FeaturePython)
  Dunit = g/cm3
  Dvalue = 0.000756182
  Group = -> [H_element111,O_element104]
  conduct = 2
  density = 1
  expand = 3
  formula = G4_WATER_VAPOR
  name = G4_WATER_VAPOR
  specific = 4
FEATURE [App::DocumentObjectGroupPython] C_element122  label="C_element : 068"  # scripted group (container) (typed FeaturePython)
  n = 8
  ref = C_element
FEATURE [App::DocumentObjectGroupPython] H_element112  label="H_element : 061"  # scripted group (container) (typed FeaturePython)
  n = 10
  ref = H_element
FEATURE [App::DocumentObjectGroupPython] G4_XYLENE  # scripted group (container) (typed FeaturePython)
  Dunit = g/cm3
  Dvalue = 0.87
  Group = -> [C_element122,H_element112]
  conduct = 2
  density = 1
  expand = 3
  formula = G4_XYLENE
  name = G4_XYLENE
  specific = 4
FEATURE [App::DocumentObjectGroupPython] C_element123  label="C_element : 069"  # scripted group (container) (typed FeaturePython)
  n = 1
  ref = C_element
FEATURE [App::DocumentObjectGroupPython] G4_GRAPHITE  # scripted group (container) (typed FeaturePython)
  Dunit = g/cm3
  Dvalue = 2.21
  Group = -> [C_element123]
  conduct = 2
  density = 1
  expand = 3
  formula = G4_GRAPHITE
  name = G4_GRAPHITE
  specific = 4
FEATURE [App::DocumentObjectGroupPython] NIST  # scripted group (container) (typed FeaturePython)
  Group = -> [G4_A_150_TISSUE,G4_ACETONE,G4_ACETYLENE,G4_ADENINE,G4_ADIPOSE_TISSUE_ICRP,G4_AIR,G4_ALANINE,G4_ALUMINUM_OXIDE,G4_AMBER,G4_AMMONIA,G4_ANILINE,G4_ANTHRACENE,G4_B_100_BONE,G4_BAKELITE,G4_BARIUM_FLUORIDE,G4_BARIUM_SULFATE,G4_BENZENE,G4_BERYLLIUM_OXIDE,G4_BGO,G4_BLOOD_ICRP,G4_BONE_COMPACT_ICRU,G4_BONE_CORTICAL_ICRP,G4_BORON_CARBIDE,G4_BORON_OXIDE,G4_BRAIN_ICRP,G4_BUTANE,G4_N_BUTYL_ALCOHOL,G4_C_552,+152 more]
FEATURE [App::DocumentObjectGroupPython] H_element113  label="H_element : 062"  # scripted group (container) (typed FeaturePython)
  n = 1
  ref = H_element
FEATURE [App::DocumentObjectGroupPython] G4_H  # scripted group (container) (typed FeaturePython)
  Dunit = g/cm3
  Dvalue = 8.3748e-05
  Group = -> [H_element113]
  conduct = 2
  density = 1
  expand = 3
  formula = H
  name = G4_H
  specific = 4
FEATURE [App::DocumentObjectGroupPython] He_element001  label="He_element : 1"  # scripted group (container) (typed FeaturePython)
  n = 1
  ref = He_element
FEATURE [App::DocumentObjectGroupPython] G4_He  # scripted group (container) (typed FeaturePython)
  Dunit = g/cm3
  Dvalue = 0.000166322
  Group = -> [He_element001]
  conduct = 2
  density = 1
  expand = 3
  formula = He
  name = G4_He
  specific = 4
FEATURE [App::DocumentObjectGroupPython] Li_element008  label="Li_element : 008"  # scripted group (container) (typed FeaturePython)
  n = 1
  ref = Li_element
FEATURE [App::DocumentObjectGroupPython] G4_Li  # scripted group (container) (typed FeaturePython)
  Dunit = g/cm3
  Dvalue = 0.534
  Group = -> [Li_element008]
  conduct = 2
  density = 1
  expand = 3
  formula = Li
  name = G4_Li
  specific = 4
FEATURE [App::DocumentObjectGroupPython] Be_element002  label="Be_element : 002"  # scripted group (container) (typed FeaturePython)
  n = 1
  ref = Be_element
FEATURE [App::DocumentObjectGroupPython] G4_Be  # scripted group (container) (typed FeaturePython)
  Dunit = g/cm3
  Dvalue = 1.848
  Group = -> [Be_element002]
  conduct = 2
  density = 1
  expand = 3
  formula = Be
  name = G4_Be
  specific = 4
FEATURE [App::DocumentObjectGroupPython] B_element007  label="B_element : 007"  # scripted group (container) (typed FeaturePython)
  n = 1
  ref = B_element
FEATURE [App::DocumentObjectGroupPython] G4_B  # scripted group (container) (typed FeaturePython)
  Dunit = g/cm3
  Dvalue = 2.37
  Group = -> [B_element007]
  conduct = 2
  density = 1
  expand = 3
  formula = B
  name = G4_B
  specific = 4
FEATURE [App::DocumentObjectGroupPython] C_element124  label="C_element : 070"  # scripted group (container) (typed FeaturePython)
  n = 1
  ref = C_element
FEATURE [App::DocumentObjectGroupPython] G4_C  # scripted group (container) (typed FeaturePython)
  Dunit = g/cm3
  Dvalue = 2
  Group = -> [C_element124]
  conduct = 2
  density = 1
  expand = 3
  formula = C
  name = G4_C
  specific = 4
FEATURE [App::DocumentObjectGroupPython] N_element048  label="N_element : 021"  # scripted group (container) (typed FeaturePython)
  n = 1
  ref = N_element
FEATURE [App::DocumentObjectGroupPython] G4_N  # scripted group (container) (typed FeaturePython)
  Dunit = g/cm3
  Dvalue = 0.0011652
  Group = -> [N_element048]
  conduct = 2
  density = 1
  expand = 3
  formula = N
  name = G4_N
  specific = 4
FEATURE [App::DocumentObjectGroupPython] O_element105  label="O_element : 059"  # scripted group (container) (typed FeaturePython)
  n = 1
  ref = O_element
FEATURE [App::DocumentObjectGroupPython] G4_O  # scripted group (container) (typed FeaturePython)
  Dunit = g/cm3
  Dvalue = 0.00133151
  Group = -> [O_element105]
  conduct = 2
  density = 1
  expand = 3
  formula = O
  name = G4_O
  specific = 4
FEATURE [App::DocumentObjectGroupPython] F_element019  label="F_element : 008"  # scripted group (container) (typed FeaturePython)
  n = 1
  ref = F_element
FEATURE [App::DocumentObjectGroupPython] G4_F  # scripted group (container) (typed FeaturePython)
  Dunit = g/cm3
  Dvalue = 0.00158029
  Group = -> [F_element019]
  conduct = 2
  density = 1
  expand = 3
  formula = F
  name = G4_F
  specific = 4
FEATURE [App::DocumentObjectGroupPython] Ne_element001  label="Ne_element : 1"  # scripted group (container) (typed FeaturePython)
  n = 1
  ref = Ne_element
FEATURE [App::DocumentObjectGroupPython] G4_Ne  # scripted group (container) (typed FeaturePython)
  Dunit = g/cm3
  Dvalue = 0.000838505
  Group = -> [Ne_element001]
  conduct = 2
  density = 1
  expand = 3
  formula = Ne
  name = G4_Ne
  specific = 4
FEATURE [App::DocumentObjectGroupPython] Na_element020  label="Na_element : 005"  # scripted group (container) (typed FeaturePython)
  n = 1
  ref = Na_element
FEATURE [App::DocumentObjectGroupPython] G4_Na  # scripted group (container) (typed FeaturePython)
  Dunit = g/cm3
  Dvalue = 0.971
  Group = -> [Na_element020]
  conduct = 2
  density = 1
  expand = 3
  formula = Na
  name = G4_Na
  specific = 4
FEATURE [App::DocumentObjectGroupPython] Mg_element011  label="Mg_element : 005"  # scripted group (container) (typed FeaturePython)
  n = 1
  ref = Mg_element
FEATURE [App::DocumentObjectGroupPython] G4_Mg  # scripted group (container) (typed FeaturePython)
  Dunit = g/cm3
  Dvalue = 1.74
  Group = -> [Mg_element011]
  conduct = 2
  density = 1
  expand = 3
  formula = Mg
  name = G4_Mg
  specific = 4
FEATURE [App::DocumentObjectGroupPython] Al_element004  label="Al_element : 1"  # scripted group (container) (typed FeaturePython)
  n = 1
  ref = Al_element
FEATURE [App::DocumentObjectGroupPython] G4_Al  # scripted group (container) (typed FeaturePython)
  Dunit = g/cm3
  Dvalue = 2.699
  Group = -> [Al_element004]
  conduct = 2
  density = 1
  expand = 3
  formula = Al
  name = G4_Al
  specific = 4
FEATURE [App::DocumentObjectGroupPython] Si_element007  label="Si_element : 002"  # scripted group (container) (typed FeaturePython)
  n = 1
  ref = Si_element
FEATURE [App::DocumentObjectGroupPython] G4_Si  # scripted group (container) (typed FeaturePython)
  Dunit = g/cm3
  Dvalue = 2.33
  Group = -> [Si_element007]
  conduct = 2
  density = 1
  expand = 3
  formula = Si
  name = G4_Si
  specific = 4
FEATURE [App::DocumentObjectGroupPython] P_element013  label="P_element : 002"  # scripted group (container) (typed FeaturePython)
  n = 1
  ref = P_element
FEATURE [App::DocumentObjectGroupPython] G4_P  # scripted group (container) (typed FeaturePython)
  Dunit = g/cm3
  Dvalue = 2.2
  Group = -> [P_element013]
  conduct = 2
  density = 1
  expand = 3
  formula = P
  name = G4_P
  specific = 4
FEATURE [App::DocumentObjectGroupPython] S_element023  label="S_element : 007"  # scripted group (container) (typed FeaturePython)
  n = 1
  ref = S_element
FEATURE [App::DocumentObjectGroupPython] G4_S  # scripted group (container) (typed FeaturePython)
  Dunit = g/cm3
  Dvalue = 2
  Group = -> [S_element023]
  conduct = 2
  density = 1
  expand = 3
  formula = S
  name = G4_S
  specific = 4
FEATURE [App::DocumentObjectGroupPython] Cl_element029  label="Cl_element : 015"  # scripted group (container) (typed FeaturePython)
  n = 1
  ref = Cl_element
FEATURE [App::DocumentObjectGroupPython] G4_Cl  # scripted group (container) (typed FeaturePython)
  Dunit = g/cm3
  Dvalue = 0.00299473
  Group = -> [Cl_element029]
  conduct = 2
  density = 1
  expand = 3
  formula = Cl
  name = G4_Cl
  specific = 4
FEATURE [App::DocumentObjectGroupPython] Ar_element002  label="Ar_element : 1"  # scripted group (container) (typed FeaturePython)
  n = 1
  ref = Ar_element
FEATURE [App::DocumentObjectGroupPython] G4_Ar  # scripted group (container) (typed FeaturePython)
  Dunit = g/cm3
  Dvalue = 0.00166201
  Group = -> [Ar_element002]
  conduct = 2
  density = 1
  expand = 3
  formula = Ar
  name = G4_Ar
  specific = 4
FEATURE [App::DocumentObjectGroupPython] K_element013  label="K_element : 003"  # scripted group (container) (typed FeaturePython)
  n = 1
  ref = K_element
FEATURE [App::DocumentObjectGroupPython] G4_K  # scripted group (container) (typed FeaturePython)
  Dunit = g/cm3
  Dvalue = 0.862
  Group = -> [K_element013]
  conduct = 2
  density = 1
  expand = 3
  formula = K
  name = G4_K
  specific = 4
FEATURE [App::DocumentObjectGroupPython] Ca_element014  label="Ca_element : 007"  # scripted group (container) (typed FeaturePython)
  n = 1
  ref = Ca_element
FEATURE [App::DocumentObjectGroupPython] G4_Ca  # scripted group (container) (typed FeaturePython)
  Dunit = g/cm3
  Dvalue = 1.55
  Group = -> [Ca_element014]
  conduct = 2
  density = 1
  expand = 3
  formula = Ca
  name = G4_Ca
  specific = 4
FEATURE [App::DocumentObjectGroupPython] Sc_element001  label="Sc_element : 1"  # scripted group (container) (typed FeaturePython)
  n = 1
  ref = Sc_element
FEATURE [App::DocumentObjectGroupPython] G4_Sc  # scripted group (container) (typed FeaturePython)
  Dunit = g/cm3
  Dvalue = 2.989
  Group = -> [Sc_element001]
  conduct = 2
  density = 1
  expand = 3
  formula = Sc
  name = G4_Sc
  specific = 4
FEATURE [App::DocumentObjectGroupPython] Ti_element004  label="Ti_element : 002"  # scripted group (container) (typed FeaturePython)
  n = 1
  ref = Ti_element
FEATURE [App::DocumentObjectGroupPython] G4_Ti  # scripted group (container) (typed FeaturePython)
  Dunit = g/cm3
  Dvalue = 4.54
  Group = -> [Ti_element004]
  conduct = 2
  density = 1
  expand = 3
  formula = Ti
  name = G4_Ti
  specific = 4
FEATURE [App::DocumentObjectGroupPython] V_element001  label="V_element : 1"  # scripted group (container) (typed FeaturePython)
  n = 1
  ref = V_element
FEATURE [App::DocumentObjectGroupPython] G4_V  # scripted group (container) (typed FeaturePython)
  Dunit = g/cm3
  Dvalue = 6.11
  Group = -> [V_element001]
  conduct = 2
  density = 1
  expand = 3
  formula = V
  name = G4_V
  specific = 4
FEATURE [App::DocumentObjectGroupPython] Cr_element001  label="Cr_element : 1"  # scripted group (container) (typed FeaturePython)
  n = 1
  ref = Cr_element
FEATURE [App::DocumentObjectGroupPython] G4_Cr  # scripted group (container) (typed FeaturePython)
  Dunit = g/cm3
  Dvalue = 7.18
  Group = -> [Cr_element001]
  conduct = 2
  density = 1
  expand = 3
  formula = Cr
  name = G4_Cr
  specific = 4
FEATURE [App::DocumentObjectGroupPython] Mn_element001  label="Mn_element : 1"  # scripted group (container) (typed FeaturePython)
  n = 1
  ref = Mn_element
FEATURE [App::DocumentObjectGroupPython] G4_Mn  # scripted group (container) (typed FeaturePython)
  Dunit = g/cm3
  Dvalue = 7.44
  Group = -> [Mn_element001]
  conduct = 2
  density = 1
  expand = 3
  formula = Mn
  name = G4_Mn
  specific = 4
FEATURE [App::DocumentObjectGroupPython] Fe_element007  label="Fe_element : 004"  # scripted group (container) (typed FeaturePython)
  n = 1
  ref = Fe_element
FEATURE [App::DocumentObjectGroupPython] G4_Fe  # scripted group (container) (typed FeaturePython)
  Dunit = g/cm3
  Dvalue = 7.874
  Group = -> [Fe_element007]
  conduct = 2
  density = 1
  expand = 3
  formula = Fe
  name = G4_Fe
  specific = 4
FEATURE [App::DocumentObjectGroupPython] Co_element001  label="Co_element : 1"  # scripted group (container) (typed FeaturePython)
  n = 1
  ref = Co_element
FEATURE [App::DocumentObjectGroupPython] G4_Co  # scripted group (container) (typed FeaturePython)
  Dunit = g/cm3
  Dvalue = 8.9
  Group = -> [Co_element001]
  conduct = 2
  density = 1
  expand = 3
  formula = Co
  name = G4_Co
  specific = 4
FEATURE [App::DocumentObjectGroupPython] Ni_element001  label="Ni_element : 1"  # scripted group (container) (typed FeaturePython)
  n = 1
  ref = Ni_element
FEATURE [App::DocumentObjectGroupPython] G4_Ni  # scripted group (container) (typed FeaturePython)
  Dunit = g/cm3
  Dvalue = 8.902
  Group = -> [Ni_element001]
  conduct = 2
  density = 1
  expand = 3
  formula = Ni
  name = G4_Ni
  specific = 4
FEATURE [App::DocumentObjectGroupPython] Cu_element001  label="Cu_element : 1"  # scripted group (container) (typed FeaturePython)
  n = 1
  ref = Cu_element
FEATURE [App::DocumentObjectGroupPython] G4_Cu  # scripted group (container) (typed FeaturePython)
  Dunit = g/cm3
  Dvalue = 8.96
  Group = -> [Cu_element001]
  conduct = 2
  density = 1
  expand = 3
  formula = Cu
  name = G4_Cu
  specific = 4
FEATURE [App::DocumentObjectGroupPython] Zn_element001  label="Zn_element : 1"  # scripted group (container) (typed FeaturePython)
  n = 1
  ref = Zn_element
FEATURE [App::DocumentObjectGroupPython] G4_Zn  # scripted group (container) (typed FeaturePython)
  Dunit = g/cm3
  Dvalue = 7.133
  Group = -> [Zn_element001]
  conduct = 2
  density = 1
  expand = 3
  formula = Zn
  name = G4_Zn
  specific = 4
FEATURE [App::DocumentObjectGroupPython] Ga_element002  label="Ga_element : 002"  # scripted group (container) (typed FeaturePython)
  n = 1
  ref = Ga_element
FEATURE [App::DocumentObjectGroupPython] G4_Ga  # scripted group (container) (typed FeaturePython)
  Dunit = g/cm3
  Dvalue = 5.904
  Group = -> [Ga_element002]
  conduct = 2
  density = 1
  expand = 3
  formula = Ga
  name = G4_Ga
  specific = 4
FEATURE [App::DocumentObjectGroupPython] Ge_element002  label="Ge_element : 1"  # scripted group (container) (typed FeaturePython)
  n = 1
  ref = Ge_element
FEATURE [App::DocumentObjectGroupPython] G4_Ge  # scripted group (container) (typed FeaturePython)
  Dunit = g/cm3
  Dvalue = 5.323
  Group = -> [Ge_element002]
  conduct = 2
  density = 1
  expand = 3
  formula = Ge
  name = G4_Ge
  specific = 4
FEATURE [App::DocumentObjectGroupPython] As_element003  label="As_element : 002"  # scripted group (container) (typed FeaturePython)
  n = 1
  ref = As_element
FEATURE [App::DocumentObjectGroupPython] G4_As  # scripted group (container) (typed FeaturePython)
  Dunit = g/cm3
  Dvalue = 5.73
  Group = -> [As_element003]
  conduct = 2
  density = 1
  expand = 3
  formula = As
  name = G4_As
  specific = 4
FEATURE [App::DocumentObjectGroupPython] Se_element001  label="Se_element : 1"  # scripted group (container) (typed FeaturePython)
  n = 1
  ref = Se_element
FEATURE [App::DocumentObjectGroupPython] G4_Se  # scripted group (container) (typed FeaturePython)
  Dunit = g/cm3
  Dvalue = 4.5
  Group = -> [Se_element001]
  conduct = 2
  density = 1
  expand = 3
  formula = Se
  name = G4_Se
  specific = 4
FEATURE [App::DocumentObjectGroupPython] Br_element007  label="Br_element : 004"  # scripted group (container) (typed FeaturePython)
  n = 1
  ref = Br_element
FEATURE [App::DocumentObjectGroupPython] G4_Br  # scripted group (container) (typed FeaturePython)
  Dunit = g/cm3
  Dvalue = 0.0070721
  Group = -> [Br_element007]
  conduct = 2
  density = 1
  expand = 3
  formula = Br
  name = G4_Br
  specific = 4
FEATURE [App::DocumentObjectGroupPython] Kr_element001  label="Kr_element : 1"  # scripted group (container) (typed FeaturePython)
  n = 1
  ref = Kr_element
FEATURE [App::DocumentObjectGroupPython] G4_Kr  # scripted group (container) (typed FeaturePython)
  Dunit = g/cm3
  Dvalue = 0.00347832
  Group = -> [Kr_element001]
  conduct = 2
  density = 1
  expand = 3
  formula = Kr
  name = G4_Kr
  specific = 4
FEATURE [App::DocumentObjectGroupPython] Rb_element001  label="Rb_element : 1"  # scripted group (container) (typed FeaturePython)
  n = 1
  ref = Rb_element
FEATURE [App::DocumentObjectGroupPython] G4_Rb  # scripted group (container) (typed FeaturePython)
  Dunit = g/cm3
  Dvalue = 1.532
  Group = -> [Rb_element001]
  conduct = 2
  density = 1
  expand = 3
  formula = Rb
  name = G4_Rb
  specific = 4
FEATURE [App::DocumentObjectGroupPython] Sr_element001  label="Sr_element : 1"  # scripted group (container) (typed FeaturePython)
  n = 1
  ref = Sr_element
FEATURE [App::DocumentObjectGroupPython] G4_Sr  # scripted group (container) (typed FeaturePython)
  Dunit = g/cm3
  Dvalue = 2.54
  Group = -> [Sr_element001]
  conduct = 2
  density = 1
  expand = 3
  formula = Sr
  name = G4_Sr
  specific = 4
FEATURE [App::DocumentObjectGroupPython] Y_element001  label="Y_element : 1"  # scripted group (container) (typed FeaturePython)
  n = 1
  ref = Y_element
FEATURE [App::DocumentObjectGroupPython] G4_Y  # scripted group (container) (typed FeaturePython)
  Dunit = g/cm3
  Dvalue = 4.469
  Group = -> [Y_element001]
  conduct = 2
  density = 1
  expand = 3
  formula = Y
  name = G4_Y
  specific = 4
FEATURE [App::DocumentObjectGroupPython] Zr_element001  label="Zr_element : 1"  # scripted group (container) (typed FeaturePython)
  n = 1
  ref = Zr_element
FEATURE [App::DocumentObjectGroupPython] G4_Zr  # scripted group (container) (typed FeaturePython)
  Dunit = g/cm3
  Dvalue = 6.506
  Group = -> [Zr_element001]
  conduct = 2
  density = 1
  expand = 3
  formula = Zr
  name = G4_Zr
  specific = 4
FEATURE [App::DocumentObjectGroupPython] Nb_element001  label="Nb_element : 1"  # scripted group (container) (typed FeaturePython)
  n = 1
  ref = Nb_element
FEATURE [App::DocumentObjectGroupPython] G4_Nb  # scripted group (container) (typed FeaturePython)
  Dunit = g/cm3
  Dvalue = 8.57
  Group = -> [Nb_element001]
  conduct = 2
  density = 1
  expand = 3
  formula = Nb
  name = G4_Nb
  specific = 4
FEATURE [App::DocumentObjectGroupPython] Mo_element001  label="Mo_element : 1"  # scripted group (container) (typed FeaturePython)
  n = 1
  ref = Mo_element
FEATURE [App::DocumentObjectGroupPython] G4_Mo  # scripted group (container) (typed FeaturePython)
  Dunit = g/cm3
  Dvalue = 10.22
  Group = -> [Mo_element001]
  conduct = 2
  density = 1
  expand = 3
  formula = Mo
  name = G4_Mo
  specific = 4
FEATURE [App::DocumentObjectGroupPython] Tc_element001  label="Tc_element : 1"  # scripted group (container) (typed FeaturePython)
  n = 1
  ref = Tc_element
FEATURE [App::DocumentObjectGroupPython] G4_Tc  # scripted group (container) (typed FeaturePython)
  Dunit = g/cm3
  Dvalue = 11.5
  Group = -> [Tc_element001]
  conduct = 2
  density = 1
  expand = 3
  formula = Tc
  name = G4_Tc
  specific = 4
FEATURE [App::DocumentObjectGroupPython] Ru_element001  label="Ru_element : 1"  # scripted group (container) (typed FeaturePython)
  n = 1
  ref = Ru_element
FEATURE [App::DocumentObjectGroupPython] G4_Ru  # scripted group (container) (typed FeaturePython)
  Dunit = g/cm3
  Dvalue = 12.41
  Group = -> [Ru_element001]
  conduct = 2
  density = 1
  expand = 3
  formula = Ru
  name = G4_Ru
  specific = 4
FEATURE [App::DocumentObjectGroupPython] Rh_element001  label="Rh_element : 1"  # scripted group (container) (typed FeaturePython)
  n = 1
  ref = Rh_element
FEATURE [App::DocumentObjectGroupPython] G4_Rh  # scripted group (container) (typed FeaturePython)
  Dunit = g/cm3
  Dvalue = 12.41
  Group = -> [Rh_element001]
  conduct = 2
  density = 1
  expand = 3
  formula = Rh
  name = G4_Rh
  specific = 4
FEATURE [App::DocumentObjectGroupPython] Pd_element001  label="Pd_element : 1"  # scripted group (container) (typed FeaturePython)
  n = 1
  ref = Pd_element
FEATURE [App::DocumentObjectGroupPython] G4_Pd  # scripted group (container) (typed FeaturePython)
  Dunit = g/cm3
  Dvalue = 12.02
  Group = -> [Pd_element001]
  conduct = 2
  density = 1
  expand = 3
  formula = Pd
  name = G4_Pd
  specific = 4
FEATURE [App::DocumentObjectGroupPython] Ag_element006  label="Ag_element : 004"  # scripted group (container) (typed FeaturePython)
  n = 1
  ref = Ag_element
FEATURE [App::DocumentObjectGroupPython] G4_Ag  # scripted group (container) (typed FeaturePython)
  Dunit = g/cm3
  Dvalue = 10.5
  Group = -> [Ag_element006]
  conduct = 2
  density = 1
  expand = 3
  formula = Ag
  name = G4_Ag
  specific = 4
FEATURE [App::DocumentObjectGroupPython] Cd_element003  label="Cd_element : 003"  # scripted group (container) (typed FeaturePython)
  n = 1
  ref = Cd_element
FEATURE [App::DocumentObjectGroupPython] G4_Cd  # scripted group (container) (typed FeaturePython)
  Dunit = g/cm3
  Dvalue = 8.65
  Group = -> [Cd_element003]
  conduct = 2
  density = 1
  expand = 3
  formula = Cd
  name = G4_Cd
  specific = 4
FEATURE [App::DocumentObjectGroupPython] In_element001  label="In_element : 1"  # scripted group (container) (typed FeaturePython)
  n = 1
  ref = In_element
FEATURE [App::DocumentObjectGroupPython] G4_In  # scripted group (container) (typed FeaturePython)
  Dunit = g/cm3
  Dvalue = 7.31
  Group = -> [In_element001]
  conduct = 2
  density = 1
  expand = 3
  formula = In
  name = G4_In
  specific = 4
FEATURE [App::DocumentObjectGroupPython] Sn_element001  label="Sn_element : 1"  # scripted group (container) (typed FeaturePython)
  n = 1
  ref = Sn_element
FEATURE [App::DocumentObjectGroupPython] G4_Sn  # scripted group (container) (typed FeaturePython)
  Dunit = g/cm3
  Dvalue = 7.31
  Group = -> [Sn_element001]
  conduct = 2
  density = 1
  expand = 3
  formula = Sn
  name = G4_Sn
  specific = 4
FEATURE [App::DocumentObjectGroupPython] Sb_element001  label="Sb_element : 1"  # scripted group (container) (typed FeaturePython)
  n = 1
  ref = Sb_element
FEATURE [App::DocumentObjectGroupPython] G4_Sb  # scripted group (container) (typed FeaturePython)
  Dunit = g/cm3
  Dvalue = 6.691
  Group = -> [Sb_element001]
  conduct = 2
  density = 1
  expand = 3
  formula = Sb
  name = G4_Sb
  specific = 4
FEATURE [App::DocumentObjectGroupPython] Te_element002  label="Te_element : 002"  # scripted group (container) (typed FeaturePython)
  n = 1
  ref = Te_element
FEATURE [App::DocumentObjectGroupPython] G4_Te  # scripted group (container) (typed FeaturePython)
  Dunit = g/cm3
  Dvalue = 6.24
  Group = -> [Te_element002]
  conduct = 2
  density = 1
  expand = 3
  formula = Te
  name = G4_Te
  specific = 4
FEATURE [App::DocumentObjectGroupPython] I_element010  label="I_element : 006"  # scripted group (container) (typed FeaturePython)
  n = 1
  ref = I_element
FEATURE [App::DocumentObjectGroupPython] G4_I  # scripted group (container) (typed FeaturePython)
  Dunit = g/cm3
  Dvalue = 4.93
  Group = -> [I_element010]
  conduct = 2
  density = 1
  expand = 3
  formula = I
  name = G4_I
  specific = 4
FEATURE [App::DocumentObjectGroupPython] Xe_element001  label="Xe_element : 1"  # scripted group (container) (typed FeaturePython)
  n = 1
  ref = Xe_element
FEATURE [App::DocumentObjectGroupPython] G4_Xe  # scripted group (container) (typed FeaturePython)
  Dunit = g/cm3
  Dvalue = 0.00548536
  Group = -> [Xe_element001]
  conduct = 2
  density = 1
  expand = 3
  formula = Xe
  name = G4_Xe
  specific = 4
FEATURE [App::DocumentObjectGroupPython] Cs_element003  label="Cs_element : 003"  # scripted group (container) (typed FeaturePython)
  n = 1
  ref = Cs_element
FEATURE [App::DocumentObjectGroupPython] G4_Cs  # scripted group (container) (typed FeaturePython)
  Dunit = g/cm3
  Dvalue = 1.873
  Group = -> [Cs_element003]
  conduct = 2
  density = 1
  expand = 3
  formula = Cs
  name = G4_Cs
  specific = 4
FEATURE [App::DocumentObjectGroupPython] Ba_element003  label="Ba_element : 003"  # scripted group (container) (typed FeaturePython)
  n = 1
  ref = Ba_element
FEATURE [App::DocumentObjectGroupPython] G4_Ba  # scripted group (container) (typed FeaturePython)
  Dunit = g/cm3
  Dvalue = 3.5
  Group = -> [Ba_element003]
  conduct = 2
  density = 1
  expand = 3
  formula = Ba
  name = G4_Ba
  specific = 4
FEATURE [App::DocumentObjectGroupPython] La_element003  label="La_element : 003"  # scripted group (container) (typed FeaturePython)
  n = 1
  ref = La_element
FEATURE [App::DocumentObjectGroupPython] G4_La  # scripted group (container) (typed FeaturePython)
  Dunit = g/cm3
  Dvalue = 6.154
  Group = -> [La_element003]
  conduct = 2
  density = 1
  expand = 3
  formula = La
  name = G4_La
  specific = 4
FEATURE [App::DocumentObjectGroupPython] Ce_element002  label="Ce_element : 1"  # scripted group (container) (typed FeaturePython)
  n = 1
  ref = Ce_element
FEATURE [App::DocumentObjectGroupPython] G4_Ce  # scripted group (container) (typed FeaturePython)
  Dunit = g/cm3
  Dvalue = 6.657
  Group = -> [Ce_element002]
  conduct = 2
  density = 1
  expand = 3
  formula = Ce
  name = G4_Ce
  specific = 4
FEATURE [App::DocumentObjectGroupPython] Pr_element001  label="Pr_element : 1"  # scripted group (container) (typed FeaturePython)
  n = 1
  ref = Pr_element
FEATURE [App::DocumentObjectGroupPython] G4_Pr  # scripted group (container) (typed FeaturePython)
  Dunit = g/cm3
  Dvalue = 6.71
  Group = -> [Pr_element001]
  conduct = 2
  density = 1
  expand = 3
  formula = Pr
  name = G4_Pr
  specific = 4
FEATURE [App::DocumentObjectGroupPython] Nd_element001  label="Nd_element : 1"  # scripted group (container) (typed FeaturePython)
  n = 1
  ref = Nd_element
FEATURE [App::DocumentObjectGroupPython] G4_Nd  # scripted group (container) (typed FeaturePython)
  Dunit = g/cm3
  Dvalue = 6.9
  Group = -> [Nd_element001]
  conduct = 2
  density = 1
  expand = 3
  formula = Nd
  name = G4_Nd
  specific = 4
FEATURE [App::DocumentObjectGroupPython] Pm_element001  label="Pm_element : 1"  # scripted group (container) (typed FeaturePython)
  n = 1
  ref = Pm_element
FEATURE [App::DocumentObjectGroupPython] G4_Pm  # scripted group (container) (typed FeaturePython)
  Dunit = g/cm3
  Dvalue = 7.22
  Group = -> [Pm_element001]
  conduct = 2
  density = 1
  expand = 3
  formula = Pm
  name = G4_Pm
  specific = 4
FEATURE [App::DocumentObjectGroupPython] Sm_element001  label="Sm_element : 1"  # scripted group (container) (typed FeaturePython)
  n = 1
  ref = Sm_element
FEATURE [App::DocumentObjectGroupPython] G4_Sm  # scripted group (container) (typed FeaturePython)
  Dunit = g/cm3
  Dvalue = 7.46
  Group = -> [Sm_element001]
  conduct = 2
  density = 1
  expand = 3
  formula = Sm
  name = G4_Sm
  specific = 4
FEATURE [App::DocumentObjectGroupPython] Eu_element001  label="Eu_element : 1"  # scripted group (container) (typed FeaturePython)
  n = 1
  ref = Eu_element
FEATURE [App::DocumentObjectGroupPython] G4_Eu  # scripted group (container) (typed FeaturePython)
  Dunit = g/cm3
  Dvalue = 5.243
  Group = -> [Eu_element001]
  conduct = 2
  density = 1
  expand = 3
  formula = Eu
  name = G4_Eu
  specific = 4
FEATURE [App::DocumentObjectGroupPython] Gd_element002  label="Gd_element : 1"  # scripted group (container) (typed FeaturePython)
  n = 1
  ref = Gd_element
FEATURE [App::DocumentObjectGroupPython] G4_Gd  # scripted group (container) (typed FeaturePython)
  Dunit = g/cm3
  Dvalue = 7.9004
  Group = -> [Gd_element002]
  conduct = 2
  density = 1
  expand = 3
  formula = Gd
  name = G4_Gd
  specific = 4
FEATURE [App::DocumentObjectGroupPython] Tb_element001  label="Tb_element : 1"  # scripted group (container) (typed FeaturePython)
  n = 1
  ref = Tb_element
FEATURE [App::DocumentObjectGroupPython] G4_Tb  # scripted group (container) (typed FeaturePython)
  Dunit = g/cm3
  Dvalue = 8.229
  Group = -> [Tb_element001]
  conduct = 2
  density = 1
  expand = 3
  formula = Tb
  name = G4_Tb
  specific = 4
FEATURE [App::DocumentObjectGroupPython] Dy_element001  label="Dy_element : 1"  # scripted group (container) (typed FeaturePython)
  n = 1
  ref = Dy_element
FEATURE [App::DocumentObjectGroupPython] G4_Dy  # scripted group (container) (typed FeaturePython)
  Dunit = g/cm3
  Dvalue = 8.55
  Group = -> [Dy_element001]
  conduct = 2
  density = 1
  expand = 3
  formula = Dy
  name = G4_Dy
  specific = 4
FEATURE [App::DocumentObjectGroupPython] Ho_element001  label="Ho_element : 1"  # scripted group (container) (typed FeaturePython)
  n = 1
  ref = Ho_element
FEATURE [App::DocumentObjectGroupPython] G4_Ho  # scripted group (container) (typed FeaturePython)
  Dunit = g/cm3
  Dvalue = 8.795
  Group = -> [Ho_element001]
  conduct = 2
  density = 1
  expand = 3
  formula = Ho
  name = G4_Ho
  specific = 4
FEATURE [App::DocumentObjectGroupPython] Er_element001  label="Er_element : 1"  # scripted group (container) (typed FeaturePython)
  n = 1
  ref = Er_element
FEATURE [App::DocumentObjectGroupPython] G4_Er  # scripted group (container) (typed FeaturePython)
  Dunit = g/cm3
  Dvalue = 9.066
  Group = -> [Er_element001]
  conduct = 2
  density = 1
  expand = 3
  formula = Er
  name = G4_Er
  specific = 4
FEATURE [App::DocumentObjectGroupPython] Tm_element001  label="Tm_element : 1"  # scripted group (container) (typed FeaturePython)
  n = 1
  ref = Tm_element
FEATURE [App::DocumentObjectGroupPython] G4_Tm  # scripted group (container) (typed FeaturePython)
  Dunit = g/cm3
  Dvalue = 9.321
  Group = -> [Tm_element001]
  conduct = 2
  density = 1
  expand = 3
  formula = Tm
  name = G4_Tm
  specific = 4
FEATURE [App::DocumentObjectGroupPython] Yb_element001  label="Yb_element : 1"  # scripted group (container) (typed FeaturePython)
  n = 1
  ref = Yb_element
FEATURE [App::DocumentObjectGroupPython] G4_Yb  # scripted group (container) (typed FeaturePython)
  Dunit = g/cm3
  Dvalue = 6.73
  Group = -> [Yb_element001]
  conduct = 2
  density = 1
  expand = 3
  formula = Yb
  name = G4_Yb
  specific = 4
FEATURE [App::DocumentObjectGroupPython] Lu_element001  label="Lu_element : 1"  # scripted group (container) (typed FeaturePython)
  n = 1
  ref = Lu_element
FEATURE [App::DocumentObjectGroupPython] G4_Lu  # scripted group (container) (typed FeaturePython)
  Dunit = g/cm3
  Dvalue = 9.84
  Group = -> [Lu_element001]
  conduct = 2
  density = 1
  expand = 3
  formula = Lu
  name = G4_Lu
  specific = 4
FEATURE [App::DocumentObjectGroupPython] Hf_element001  label="Hf_element : 1"  # scripted group (container) (typed FeaturePython)
  n = 1
  ref = Hf_element
FEATURE [App::DocumentObjectGroupPython] G4_Hf  # scripted group (container) (typed FeaturePython)
  Dunit = g/cm3
  Dvalue = 13.31
  Group = -> [Hf_element001]
  conduct = 2
  density = 1
  expand = 3
  formula = Hf
  name = G4_Hf
  specific = 4
FEATURE [App::DocumentObjectGroupPython] Ta_element001  label="Ta_element : 1"  # scripted group (container) (typed FeaturePython)
  n = 1
  ref = Ta_element
FEATURE [App::DocumentObjectGroupPython] G4_Ta  # scripted group (container) (typed FeaturePython)
  Dunit = g/cm3
  Dvalue = 16.654
  Group = -> [Ta_element001]
  conduct = 2
  density = 1
  expand = 3
  formula = Ta
  name = G4_Ta
  specific = 4
FEATURE [App::DocumentObjectGroupPython] W_element004  label="W_element : 004"  # scripted group (container) (typed FeaturePython)
  n = 1
  ref = W_element
FEATURE [App::DocumentObjectGroupPython] G4_W  # scripted group (container) (typed FeaturePython)
  Dunit = g/cm3
  Dvalue = 19.3
  Group = -> [W_element004]
  conduct = 2
  density = 1
  expand = 3
  formula = W
  name = G4_W
  specific = 4
FEATURE [App::DocumentObjectGroupPython] Re_element001  label="Re_element : 1"  # scripted group (container) (typed FeaturePython)
  n = 1
  ref = Re_element
FEATURE [App::DocumentObjectGroupPython] G4_Re  # scripted group (container) (typed FeaturePython)
  Dunit = g/cm3
  Dvalue = 21.02
  Group = -> [Re_element001]
  conduct = 2
  density = 1
  expand = 3
  formula = Re
  name = G4_Re
  specific = 4
FEATURE [App::DocumentObjectGroupPython] Os_element001  label="Os_element : 1"  # scripted group (container) (typed FeaturePython)
  n = 1
  ref = Os_element
FEATURE [App::DocumentObjectGroupPython] G4_Os  # scripted group (container) (typed FeaturePython)
  Dunit = g/cm3
  Dvalue = 22.57
  Group = -> [Os_element001]
  conduct = 2
  density = 1
  expand = 3
  formula = Os
  name = G4_Os
  specific = 4
FEATURE [App::DocumentObjectGroupPython] Ir_element001  label="Ir_element : 1"  # scripted group (container) (typed FeaturePython)
  n = 1
  ref = Ir_element
FEATURE [App::DocumentObjectGroupPython] G4_Ir  # scripted group (container) (typed FeaturePython)
  Dunit = g/cm3
  Dvalue = 22.42
  Group = -> [Ir_element001]
  conduct = 2
  density = 1
  expand = 3
  formula = Ir
  name = G4_Ir
  specific = 4
FEATURE [App::DocumentObjectGroupPython] Pt_element001  label="Pt_element : 1"  # scripted group (container) (typed FeaturePython)
  n = 1
  ref = Pt_element
FEATURE [App::DocumentObjectGroupPython] G4_Pt  # scripted group (container) (typed FeaturePython)
  Dunit = g/cm3
  Dvalue = 21.45
  Group = -> [Pt_element001]
  conduct = 2
  density = 1
  expand = 3
  formula = Pt
  name = G4_Pt
  specific = 4
FEATURE [App::DocumentObjectGroupPython] Au_element001  label="Au_element : 1"  # scripted group (container) (typed FeaturePython)
  n = 1
  ref = Au_element
FEATURE [App::DocumentObjectGroupPython] G4_Au  # scripted group (container) (typed FeaturePython)
  Dunit = g/cm3
  Dvalue = 19.32
  Group = -> [Au_element001]
  conduct = 2
  density = 1
  expand = 3
  formula = Au
  name = G4_Au
  specific = 4
FEATURE [App::DocumentObjectGroupPython] Hg_element002  label="Hg_element : 002"  # scripted group (container) (typed FeaturePython)
  n = 1
  ref = Hg_element
FEATURE [App::DocumentObjectGroupPython] G4_Hg  # scripted group (container) (typed FeaturePython)
  Dunit = g/cm3
  Dvalue = 13.546
  Group = -> [Hg_element002]
  conduct = 2
  density = 1
  expand = 3
  formula = Hg
  name = G4_Hg
  specific = 4
FEATURE [App::DocumentObjectGroupPython] Tl_element002  label="Tl_element : 002"  # scripted group (container) (typed FeaturePython)
  n = 1
  ref = Tl_element
FEATURE [App::DocumentObjectGroupPython] G4_Tl  # scripted group (container) (typed FeaturePython)
  Dunit = g/cm3
  Dvalue = 11.72
  Group = -> [Tl_element002]
  conduct = 2
  density = 1
  expand = 3
  formula = Tl
  name = G4_Tl
  specific = 4
FEATURE [App::DocumentObjectGroupPython] Pb_element003  label="Pb_element : 1"  # scripted group (container) (typed FeaturePython)
  n = 1
  ref = Pb_element
FEATURE [App::DocumentObjectGroupPython] G4_Pb  # scripted group (container) (typed FeaturePython)
  Dunit = g/cm3
  Dvalue = 11.35
  Group = -> [Pb_element003]
  conduct = 2
  density = 1
  expand = 3
  formula = Pb
  name = G4_Pb
  specific = 4
FEATURE [App::DocumentObjectGroupPython] Bi_element002  label="Bi_element : 1"  # scripted group (container) (typed FeaturePython)
  n = 1
  ref = Bi_element
FEATURE [App::DocumentObjectGroupPython] G4_Bi  # scripted group (container) (typed FeaturePython)
  Dunit = g/cm3
  Dvalue = 9.747
  Group = -> [Bi_element002]
  conduct = 2
  density = 1
  expand = 3
  formula = Bi
  name = G4_Bi
  specific = 4
FEATURE [App::DocumentObjectGroupPython] Po_element001  label="Po_element : 1"  # scripted group (container) (typed FeaturePython)
  n = 1
  ref = Po_element
FEATURE [App::DocumentObjectGroupPython] G4_Po  # scripted group (container) (typed FeaturePython)
  Dunit = g/cm3
  Dvalue = 9.32
  Group = -> [Po_element001]
  conduct = 2
  density = 1
  expand = 3
  formula = Po
  name = G4_Po
  specific = 4
FEATURE [App::DocumentObjectGroupPython] At_element001  label="At_element : 1"  # scripted group (container) (typed FeaturePython)
  n = 1
  ref = At_element
FEATURE [App::DocumentObjectGroupPython] G4_At  # scripted group (container) (typed FeaturePython)
  Dunit = g/cm3
  Dvalue = 9.32
  Group = -> [At_element001]
  conduct = 2
  density = 1
  expand = 3
  formula = At
  name = G4_At
  specific = 4
FEATURE [App::DocumentObjectGroupPython] Rn_element001  label="Rn_element : 1"  # scripted group (container) (typed FeaturePython)
  n = 1
  ref = Rn_element
FEATURE [App::DocumentObjectGroupPython] G4_Rn  # scripted group (container) (typed FeaturePython)
  Dunit = g/cm3
  Dvalue = 0.00900662
  Group = -> [Rn_element001]
  conduct = 2
  density = 1
  expand = 3
  formula = Rn
  name = G4_Rn
  specific = 4
FEATURE [App::DocumentObjectGroupPython] Fr_element001  label="Fr_element : 1"  # scripted group (container) (typed FeaturePython)
  n = 1
  ref = Fr_element
FEATURE [App::DocumentObjectGroupPython] G4_Fr  # scripted group (container) (typed FeaturePython)
  Dunit = g/cm3
  Dvalue = 1
  Group = -> [Fr_element001]
  conduct = 2
  density = 1
  expand = 3
  formula = Fr
  name = G4_Fr
  specific = 4
FEATURE [App::DocumentObjectGroupPython] Ra_element001  label="Ra_element : 1"  # scripted group (container) (typed FeaturePython)
  n = 1
  ref = Ra_element
FEATURE [App::DocumentObjectGroupPython] G4_Ra  # scripted group (container) (typed FeaturePython)
  Dunit = g/cm3
  Dvalue = 5
  Group = -> [Ra_element001]
  conduct = 2
  density = 1
  expand = 3
  formula = Ra
  name = G4_Ra
  specific = 4
FEATURE [App::DocumentObjectGroupPython] Ac_element001  label="Ac_element : 1"  # scripted group (container) (typed FeaturePython)
  n = 1
  ref = Ac_element
FEATURE [App::DocumentObjectGroupPython] G4_Ac  # scripted group (container) (typed FeaturePython)
  Dunit = g/cm3
  Dvalue = 10.07
  Group = -> [Ac_element001]
  conduct = 2
  density = 1
  expand = 3
  formula = Ac
  name = G4_Ac
  specific = 4
FEATURE [App::DocumentObjectGroupPython] Th_element001  label="Th_element : 1"  # scripted group (container) (typed FeaturePython)
  n = 1
  ref = Th_element
FEATURE [App::DocumentObjectGroupPython] G4_Th  # scripted group (container) (typed FeaturePython)
  Dunit = g/cm3
  Dvalue = 11.72
  Group = -> [Th_element001]
  conduct = 2
  density = 1
  expand = 3
  formula = Th
  name = G4_Th
  specific = 4
FEATURE [App::DocumentObjectGroupPython] Pa_element001  label="Pa_element : 1"  # scripted group (container) (typed FeaturePython)
  n = 1
  ref = Pa_element
FEATURE [App::DocumentObjectGroupPython] G4_Pa  # scripted group (container) (typed FeaturePython)
  Dunit = g/cm3
  Dvalue = 15.37
  Group = -> [Pa_element001]
  conduct = 2
  density = 1
  expand = 3
  formula = Pa
  name = G4_Pa
  specific = 4
FEATURE [App::DocumentObjectGroupPython] U_element004  label="U_element : 004"  # scripted group (container) (typed FeaturePython)
  n = 1
  ref = U_element
FEATURE [App::DocumentObjectGroupPython] G4_U  # scripted group (container) (typed FeaturePython)
  Dunit = g/cm3
  Dvalue = 18.95
  Group = -> [U_element004]
  conduct = 2
  density = 1
  expand = 3
  formula = U
  name = G4_U
  specific = 4
FEATURE [App::DocumentObjectGroupPython] Np_element001  label="Np_element : 1"  # scripted group (container) (typed FeaturePython)
  n = 1
  ref = Np_element
FEATURE [App::DocumentObjectGroupPython] G4_Np  # scripted group (container) (typed FeaturePython)
  Dunit = g/cm3
  Dvalue = 20.25
  Group = -> [Np_element001]
  conduct = 2
  density = 1
  expand = 3
  formula = Np
  name = G4_Np
  specific = 4
FEATURE [App::DocumentObjectGroupPython] Pu_element002  label="Pu_element : 002"  # scripted group (container) (typed FeaturePython)
  n = 1
  ref = Pu_element
FEATURE [App::DocumentObjectGroupPython] G4_Pu  # scripted group (container) (typed FeaturePython)
  Dunit = g/cm3
  Dvalue = 19.84
  Group = -> [Pu_element002]
  conduct = 2
  density = 1
  expand = 3
  formula = Pu
  name = G4_Pu
  specific = 4
FEATURE [App::DocumentObjectGroupPython] Am_element001  label="Am_element : 1"  # scripted group (container) (typed FeaturePython)
  n = 1
  ref = Am_element
FEATURE [App::DocumentObjectGroupPython] G4_Am  # scripted group (container) (typed FeaturePython)
  Dunit = g/cm3
  Dvalue = 13.67
  Group = -> [Am_element001]
  conduct = 2
  density = 1
  expand = 3
  formula = Am
  name = G4_Am
  specific = 4
FEATURE [App::DocumentObjectGroupPython] Cm_element001  label="Cm_element : 1"  # scripted group (container) (typed FeaturePython)
  n = 1
  ref = Cm_element
FEATURE [App::DocumentObjectGroupPython] G4_Cm  # scripted group (container) (typed FeaturePython)
  Dunit = g/cm3
  Dvalue = 13.51
  Group = -> [Cm_element001]
  conduct = 2
  density = 1
  expand = 3
  formula = Cm
  name = G4_Cm
  specific = 4
FEATURE [App::DocumentObjectGroupPython] Bk_element001  label="Bk_element : 1"  # scripted group (container) (typed FeaturePython)
  n = 1
  ref = Bk_element
FEATURE [App::DocumentObjectGroupPython] G4_Bk  # scripted group (container) (typed FeaturePython)
  Dunit = g/cm3
  Dvalue = 14
  Group = -> [Bk_element001]
  conduct = 2
  density = 1
  expand = 3
  formula = Bk
  name = G4_Bk
  specific = 4
FEATURE [App::DocumentObjectGroupPython] Cf_element001  label="Cf_element : 1"  # scripted group (container) (typed FeaturePython)
  n = 1
  ref = Cf_element
FEATURE [App::DocumentObjectGroupPython] G4_Cf  # scripted group (container) (typed FeaturePython)
  Dunit = g/cm3
  Dvalue = 10
  Group = -> [Cf_element001]
  conduct = 2
  density = 1
  expand = 3
  formula = Cf
  name = G4_Cf
  specific = 4
FEATURE [App::DocumentObjectGroupPython] Element  # scripted group (container) (typed FeaturePython)
  Group = -> [G4_H,G4_He,G4_Li,G4_Be,G4_B,G4_C,G4_N,G4_O,G4_F,G4_Ne,G4_Na,G4_Mg,G4_Al,G4_Si,G4_P,G4_S,G4_Cl,G4_Ar,G4_K,G4_Ca,G4_Sc,G4_Ti,G4_V,G4_Cr,G4_Mn,G4_Fe,G4_Co,G4_Ni,G4_Cu,G4_Zn,G4_Ga,G4_Ge,G4_As,G4_Se,G4_Br,G4_Kr,G4_Rb,G4_Sr,G4_Y,G4_Zr,G4_Nb,G4_Mo,G4_Tc,G4_Ru,G4_Rh,G4_Pd,G4_Ag,G4_Cd,G4_In,G4_Sn,G4_Sb,G4_Te,G4_I,G4_Xe,G4_Cs,G4_Ba,G4_La,G4_Ce,G4_Pr,G4_Nd,G4_Pm,G4_Sm,G4_Eu,G4_Gd,G4_Tb,G4_Dy,G4_Ho,G4_Er,+30 more]
FEATURE [App::DocumentObjectGroupPython] H_element114  label="H_element : 063"  # scripted group (container) (typed FeaturePython)
  n = 2
  ref = H_element
FEATURE [App::DocumentObjectGroupPython] G4_lH2  # scripted group (container) (typed FeaturePython)
  Dunit = g/cm3
  Dvalue = 0.0708
  Group = -> [H_element114]
  conduct = 2
  density = 1
  expand = 3
  formula = G4_lH2
  name = G4_lH2
  specific = 4
FEATURE [App::DocumentObjectGroupPython] N_element049  label="N_element : 022"  # scripted group (container) (typed FeaturePython)
  n = 2
  ref = N_element
FEATURE [App::DocumentObjectGroupPython] G4_lN2  # scripted group (container) (typed FeaturePython)
  Dunit = g/cm3
  Dvalue = 0.807
  Group = -> [N_element049]
  conduct = 2
  density = 1
  expand = 3
  formula = G4_lN2
  name = G4_lN2
  specific = 4
FEATURE [App::DocumentObjectGroupPython] O_element106  label="O_element : 060"  # scripted group (container) (typed FeaturePython)
  n = 2
  ref = O_element
FEATURE [App::DocumentObjectGroupPython] G4_lO2  # scripted group (container) (typed FeaturePython)
  Dunit = g/cm3
  Dvalue = 1.141
  Group = -> [O_element106]
  conduct = 2
  density = 1
  expand = 3
  formula = G4_lO2
  name = G4_lO2
  specific = 4
FEATURE [App::DocumentObjectGroupPython] Ar_element003  label="Ar_element : 002"  # scripted group (container) (typed FeaturePython)
  n = 1
  ref = Ar_element
FEATURE [App::DocumentObjectGroupPython] G4_lAr  # scripted group (container) (typed FeaturePython)
  Dunit = g/cm3
  Dvalue = 1.396
  Group = -> [Ar_element003]
  conduct = 2
  density = 1
  expand = 3
  formula = G4_lAr
  name = G4_lAr
  specific = 4
FEATURE [App::DocumentObjectGroupPython] Br_element008  label="Br_element : 005"  # scripted group (container) (typed FeaturePython)
  n = 1
  ref = Br_element
FEATURE [App::DocumentObjectGroupPython] G4_lBr  # scripted group (container) (typed FeaturePython)
  Dunit = g/cm3
  Dvalue = 3.1028
  Group = -> [Br_element008]
  conduct = 2
  density = 1
  expand = 3
  formula = G4_lBr
  name = G4_lBr
  specific = 4
FEATURE [App::DocumentObjectGroupPython] Kr_element002  label="Kr_element : 002"  # scripted group (container) (typed FeaturePython)
  n = 1
  ref = Kr_element
FEATURE [App::DocumentObjectGroupPython] G4_lKr  # scripted group (container) (typed FeaturePython)
  Dunit = g/cm3
  Dvalue = 2.418
  Group = -> [Kr_element002]
  conduct = 2
  density = 1
  expand = 3
  formula = G4_lKr
  name = G4_lKr
  specific = 4
FEATURE [App::DocumentObjectGroupPython] Xe_element002  label="Xe_element : 002"  # scripted group (container) (typed FeaturePython)
  n = 1
  ref = Xe_element
FEATURE [App::DocumentObjectGroupPython] G4_lXe  # scripted group (container) (typed FeaturePython)
  Dunit = g/cm3
  Dvalue = 2.953
  Group = -> [Xe_element002]
  conduct = 2
  density = 1
  expand = 3
  formula = G4_lXe
  name = G4_lXe
  specific = 4
FEATURE [App::DocumentObjectGroupPython] O_element107  label="O_element : 061"  # scripted group (container) (typed FeaturePython)
  n = 4
  ref = O_element
FEATURE [App::DocumentObjectGroupPython] Pb_element004  label="Pb_element : 002"  # scripted group (container) (typed FeaturePython)
  n = 1
  ref = Pb_element
FEATURE [App::DocumentObjectGroupPython] W_element005  label="W_element : 005"  # scripted group (container) (typed FeaturePython)
  n = 1
  ref = W_element
FEATURE [App::DocumentObjectGroupPython] G4_PbWO4  # scripted group (container) (typed FeaturePython)
  Dunit = g/cm3
  Dvalue = 8.28
  Group = -> [O_element107,Pb_element004,W_element005]
  conduct = 2
  density = 1
  expand = 3
  formula = G4_PbWO4
  name = G4_PbWO4
  specific = 4
FEATURE [App::DocumentObjectGroupPython] H_element115  label="H_element : 064"  # scripted group (container) (typed FeaturePython)
  n = 1
  ref = H_element
FEATURE [App::DocumentObjectGroupPython] G4_Galactic  # scripted group (container) (typed FeaturePython)
  Dunit = g/cm3
  Dvalue = 0
  Group = -> [H_element115]
  conduct = 2
  density = 1
  expand = 3
  formula = G4_Galactic
  name = G4_Galactic
  specific = 4
FEATURE [App::DocumentObjectGroupPython] C_element125  label="C_element : 071"  # scripted group (container) (typed FeaturePython)
  n = 1
  ref = C_element
FEATURE [App::DocumentObjectGroupPython] G4_GRAPHITE_POROUS  # scripted group (container) (typed FeaturePython)
  Dunit = g/cm3
  Dvalue = 1.7
  Group = -> [C_element125]
  conduct = 2
  density = 1
  expand = 3
  formula = G4_GRAPHITE_POROUS
  name = G4_GRAPHITE_POROUS
  specific = 4
FEATURE [App::DocumentObjectGroupPython] H_element116  label="H_element : 0.150"  # scripted group (container) (typed FeaturePython)
  n = 0.080538
FEATURE [App::DocumentObjectGroupPython] C_element126  label="C_element : 0.600"  # scripted group (container) (typed FeaturePython)
  n = 0.599848
FEATURE [App::DocumentObjectGroupPython] O_element108  label="O_element : 0.320"  # scripted group (container) (typed FeaturePython)
  n = 0.319614
FEATURE [App::DocumentObjectGroupPython] G4_LUCITE  # scripted group (container) (typed FeaturePython)
  Dunit = g/cm3
  Dvalue = 1.19
  Group = -> [H_element116,C_element126,O_element108]
  conduct = 2
  density = 1
  expand = 3
  formula = G4_LUCITE
  name = G4_LUCITE
  specific = 4
FEATURE [App::DocumentObjectGroupPython] Cu_element002  label="Cu_element : 62"  # scripted group (container) (typed FeaturePython)
  n = 62
  ref = Cu_element
FEATURE [App::DocumentObjectGroupPython] Zn_element002  label="Zn_element : 35"  # scripted group (container) (typed FeaturePython)
  n = 35
  ref = Zn_element
FEATURE [App::DocumentObjectGroupPython] Pb_element005  label="Pb_element : 3"  # scripted group (container) (typed FeaturePython)
  n = 3
  ref = Pb_element
FEATURE [App::DocumentObjectGroupPython] G4_BRASS  # scripted group (container) (typed FeaturePython)
  Dunit = g/cm3
  Dvalue = 8.52
  Group = -> [Cu_element002,Zn_element002,Pb_element005]
  conduct = 2
  density = 1
  expand = 3
  formula = G4_BRASS
  name = G4_BRASS
  specific = 4
FEATURE [App::DocumentObjectGroupPython] Cu_element003  label="Cu_element : 89"  # scripted group (container) (typed FeaturePython)
  n = 89
  ref = Cu_element
FEATURE [App::DocumentObjectGroupPython] Zn_element003  label="Zn_element : 9"  # scripted group (container) (typed FeaturePython)
  n = 9
  ref = Zn_element
FEATURE [App::DocumentObjectGroupPython] Pb_element006  label="Pb_element : 2"  # scripted group (container) (typed FeaturePython)
  n = 2
  ref = Pb_element
FEATURE [App::DocumentObjectGroupPython] G4_BRONZE  # scripted group (container) (typed FeaturePython)
  Dunit = g/cm3
  Dvalue = 8.82
  Group = -> [Cu_element003,Zn_element003,Pb_element006]
  conduct = 2
  density = 1
  expand = 3
  formula = G4_BRONZE
  name = G4_BRONZE
  specific = 4
FEATURE [App::DocumentObjectGroupPython] Fe_element008  label="Fe_element : 74"  # scripted group (container) (typed FeaturePython)
  n = 74
  ref = Fe_element
FEATURE [App::DocumentObjectGroupPython] Cr_element002  label="Cr_element : 18"  # scripted group (container) (typed FeaturePython)
  n = 18
  ref = Cr_element
FEATURE [App::DocumentObjectGroupPython] Ni_element002  label="Ni_element : 8"  # scripted group (container) (typed FeaturePython)
  n = 8
  ref = Ni_element
FEATURE [App::DocumentObjectGroupPython] G4_STAINLESS_STEEL  label="G4_STAINLESS-STEEL"  # scripted group (container) (typed FeaturePython)
  Dunit = g/cm3
  Dvalue = 8
  Group = -> [Fe_element008,Cr_element002,Ni_element002]
  conduct = 2
  density = 1
  expand = 3
  formula = G4_STAINLESS-STEEL
  name = G4_STAINLESS-STEEL
  specific = 4
FEATURE [App::DocumentObjectGroupPython] H_element117  label="H_element : 065"  # scripted group (container) (typed FeaturePython)
  n = 18
  ref = H_element
FEATURE [App::DocumentObjectGroupPython] C_element127  label="C_element : 072"  # scripted group (container) (typed FeaturePython)
  n = 12
  ref = C_element
FEATURE [App::DocumentObjectGroupPython] O_element109  label="O_element : 062"  # scripted group (container) (typed FeaturePython)
  n = 7
  ref = O_element
FEATURE [App::DocumentObjectGroupPython] G4_CR39  # scripted group (container) (typed FeaturePython)
  Dunit = g/cm3
  Dvalue = 1.32
  Group = -> [H_element117,C_element127,O_element109]
  conduct = 2
  density = 1
  expand = 3
  formula = G4_CR39
  name = G4_CR39
  specific = 4
FEATURE [App::DocumentObjectGroupPython] H_element118  label="H_element : 38"  # scripted group (container) (typed FeaturePython)
  n = 38
  ref = H_element
FEATURE [App::DocumentObjectGroupPython] C_element128  label="C_element : 073"  # scripted group (container) (typed FeaturePython)
  n = 18
  ref = C_element
FEATURE [App::DocumentObjectGroupPython] O_element110  label="O_element : 063"  # scripted group (container) (typed FeaturePython)
  n = 1
  ref = O_element
FEATURE [App::DocumentObjectGroupPython] G4_OCTADECANOL  # scripted group (container) (typed FeaturePython)
  Dunit = g/cm3
  Dvalue = 0.812
  Group = -> [H_element118,C_element128,O_element110]
  conduct = 2
  density = 1
  expand = 3
  formula = G4_OCTADECANOL
  name = G4_OCTADECANOL
  specific = 4
FEATURE [App::DocumentObjectGroupPython] HEP  # scripted group (container) (typed FeaturePython)
  Group = -> [G4_lH2,G4_lN2,G4_lO2,G4_lAr,G4_lBr,G4_lKr,G4_lXe,G4_PbWO4,G4_Galactic,G4_GRAPHITE_POROUS,G4_LUCITE,G4_BRASS,G4_BRONZE,G4_STAINLESS_STEEL,G4_CR39,G4_OCTADECANOL]
FEATURE [App::DocumentObjectGroupPython] C_element129  label="C_element : 074"  # scripted group (container) (typed FeaturePython)
  n = 14
  ref = C_element
FEATURE [App::DocumentObjectGroupPython] H_element119  label="H_element : 066"  # scripted group (container) (typed FeaturePython)
  n = 10
  ref = H_element
FEATURE [App::DocumentObjectGroupPython] O_element111  label="O_element : 064"  # scripted group (container) (typed FeaturePython)
  n = 2
  ref = O_element
FEATURE [App::DocumentObjectGroupPython] N_element050  label="N_element : 023"  # scripted group (container) (typed FeaturePython)
  n = 2
  ref = N_element
FEATURE [App::DocumentObjectGroupPython] G4_KEVLAR  # scripted group (container) (typed FeaturePython)
  Dunit = g/cm3
  Dvalue = 1.44
  Group = -> [C_element129,H_element119,O_element111,N_element050]
  conduct = 2
  density = 1
  expand = 3
  formula = G4_KEVLAR
  name = G4_KEVLAR
  specific = 4
FEATURE [App::DocumentObjectGroupPython] C_element130  label="C_element : 075"  # scripted group (container) (typed FeaturePython)
  n = 10
  ref = C_element
FEATURE [App::DocumentObjectGroupPython] H_element120  label="H_element : 067"  # scripted group (container) (typed FeaturePython)
  n = 8
  ref = H_element
FEATURE [App::DocumentObjectGroupPython] O_element112  label="O_element : 065"  # scripted group (container) (typed FeaturePython)
  n = 4
  ref = O_element
FEATURE [App::DocumentObjectGroupPython] G4_DACRON  # scripted group (container) (typed FeaturePython)
  Dunit = g/cm3
  Dvalue = 1.4
  Group = -> [C_element130,H_element120,O_element112]
  conduct = 2
  density = 1
  expand = 3
  formula = G4_DACRON
  name = G4_DACRON
  specific = 4
FEATURE [App::DocumentObjectGroupPython] C_element131  label="C_element : 076"  # scripted group (container) (typed FeaturePython)
  n = 4
  ref = C_element
FEATURE [App::DocumentObjectGroupPython] H_element121  label="H_element : 068"  # scripted group (container) (typed FeaturePython)
  n = 5
  ref = H_element
FEATURE [App::DocumentObjectGroupPython] Cl_element030  label="Cl_element : 016"  # scripted group (container) (typed FeaturePython)
  n = 1
  ref = Cl_element
FEATURE [App::DocumentObjectGroupPython] G4_NEOPRENE  # scripted group (container) (typed FeaturePython)
  Dunit = g/cm3
  Dvalue = 1.23
  Group = -> [C_element131,H_element121,Cl_element030]
  conduct = 2
  density = 1
  expand = 3
  formula = G4_NEOPRENE
  name = G4_NEOPRENE
  specific = 4
FEATURE [App::DocumentObjectGroupPython] Space  # scripted group (container) (typed FeaturePython)
  Group = -> [G4_KEVLAR,G4_DACRON,G4_NEOPRENE]
FEATURE [App::DocumentObjectGroupPython] H_element122  label="H_element : 069"  # scripted group (container) (typed FeaturePython)
  n = 5
  ref = H_element
FEATURE [App::DocumentObjectGroupPython] C_element132  label="C_element : 077"  # scripted group (container) (typed FeaturePython)
  n = 4
  ref = C_element
FEATURE [App::DocumentObjectGroupPython] N_element051  label="N_element : 3"  # scripted group (container) (typed FeaturePython)
  n = 3
  ref = N_element
FEATURE [App::DocumentObjectGroupPython] O_element113  label="O_element : 066"  # scripted group (container) (typed FeaturePython)
  n = 1
  ref = O_element
FEATURE [App::DocumentObjectGroupPython] G4_CYTOSINE  # scripted group (container) (typed FeaturePython)
  Dunit = g/cm3
  Dvalue = 1.55
  Group = -> [H_element122,C_element132,N_element051,O_element113]
  conduct = 2
  density = 1
  expand = 3
  formula = G4_CYTOSINE
  name = G4_CYTOSINE
  specific = 4
FEATURE [App::DocumentObjectGroupPython] H_element123  label="H_element : 070"  # scripted group (container) (typed FeaturePython)
  n = 6
  ref = H_element
FEATURE [App::DocumentObjectGroupPython] C_element133  label="C_element : 078"  # scripted group (container) (typed FeaturePython)
  n = 5
  ref = C_element
FEATURE [App::DocumentObjectGroupPython] N_element052  label="N_element : 024"  # scripted group (container) (typed FeaturePython)
  n = 2
  ref = N_element
FEATURE [App::DocumentObjectGroupPython] O_element114  label="O_element : 067"  # scripted group (container) (typed FeaturePython)
  n = 2
  ref = O_element
FEATURE [App::DocumentObjectGroupPython] G4_THYMINE  # scripted group (container) (typed FeaturePython)
  Dunit = g/cm3
  Dvalue = 1.23
  Group = -> [H_element123,C_element133,N_element052,O_element114]
  conduct = 2
  density = 1
  expand = 3
  formula = G4_THYMINE
  name = G4_THYMINE
  specific = 4
FEATURE [App::DocumentObjectGroupPython] H_element124  label="H_element : 071"  # scripted group (container) (typed FeaturePython)
  n = 4
  ref = H_element
FEATURE [App::DocumentObjectGroupPython] C_element134  label="C_element : 079"  # scripted group (container) (typed FeaturePython)
  n = 4
  ref = C_element
FEATURE [App::DocumentObjectGroupPython] N_element053  label="N_element : 025"  # scripted group (container) (typed FeaturePython)
  n = 2
  ref = N_element
FEATURE [App::DocumentObjectGroupPython] O_element115  label="O_element : 068"  # scripted group (container) (typed FeaturePython)
  n = 2
  ref = O_element
FEATURE [App::DocumentObjectGroupPython] G4_URACIL  # scripted group (container) (typed FeaturePython)
  Dunit = g/cm3
  Dvalue = 1.32
  Group = -> [H_element124,C_element134,N_element053,O_element115]
  conduct = 2
  density = 1
  expand = 3
  formula = G4_URACIL
  name = G4_URACIL
  specific = 4
FEATURE [App::DocumentObjectGroupPython] H_element125  label="H_element : 072"  # scripted group (container) (typed FeaturePython)
  n = 4
  ref = H_element
FEATURE [App::DocumentObjectGroupPython] C_element135  label="C_element : 080"  # scripted group (container) (typed FeaturePython)
  n = 5
  ref = C_element
FEATURE [App::DocumentObjectGroupPython] N_element054  label="N_element : 026"  # scripted group (container) (typed FeaturePython)
  n = 5
  ref = N_element
FEATURE [App::DocumentObjectGroupPython] G4_DNA_ADENINE  # scripted group (container) (typed FeaturePython)
  Dunit = g/cm3
  Dvalue = 1
  Group = -> [H_element125,C_element135,N_element054]
  conduct = 2
  density = 1
  expand = 3
  formula = G4_DNA_ADENINE
  name = G4_DNA_ADENINE
  specific = 4
FEATURE [App::DocumentObjectGroupPython] H_element126  label="H_element : 073"  # scripted group (container) (typed FeaturePython)
  n = 4
  ref = H_element
FEATURE [App::DocumentObjectGroupPython] C_element136  label="C_element : 081"  # scripted group (container) (typed FeaturePython)
  n = 5
  ref = C_element
FEATURE [App::DocumentObjectGroupPython] N_element055  label="N_element : 027"  # scripted group (container) (typed FeaturePython)
  n = 5
  ref = N_element
FEATURE [App::DocumentObjectGroupPython] O_element116  label="O_element : 069"  # scripted group (container) (typed FeaturePython)
  n = 1
  ref = O_element
FEATURE [App::DocumentObjectGroupPython] G4_DNA_GUANINE  # scripted group (container) (typed FeaturePython)
  Dunit = g/cm3
  Dvalue = 1
  Group = -> [H_element126,C_element136,N_element055,O_element116]
  conduct = 2
  density = 1
  expand = 3
  formula = G4_DNA_GUANINE
  name = G4_DNA_GUANINE
  specific = 4
FEATURE [App::DocumentObjectGroupPython] H_element127  label="H_element : 074"  # scripted group (container) (typed FeaturePython)
  n = 4
  ref = H_element
FEATURE [App::DocumentObjectGroupPython] C_element137  label="C_element : 082"  # scripted group (container) (typed FeaturePython)
  n = 4
  ref = C_element
FEATURE [App::DocumentObjectGroupPython] N_element056  label="N_element : 028"  # scripted group (container) (typed FeaturePython)
  n = 3
  ref = N_element
FEATURE [App::DocumentObjectGroupPython] O_element117  label="O_element : 070"  # scripted group (container) (typed FeaturePython)
  n = 1
  ref = O_element
FEATURE [App::DocumentObjectGroupPython] G4_DNA_CYTOSINE  # scripted group (container) (typed FeaturePython)
  Dunit = g/cm3
  Dvalue = 1
  Group = -> [H_element127,C_element137,N_element056,O_element117]
  conduct = 2
  density = 1
  expand = 3
  formula = G4_DNA_CYTOSINE
  name = G4_DNA_CYTOSINE
  specific = 4
FEATURE [App::DocumentObjectGroupPython] H_element128  label="H_element : 075"  # scripted group (container) (typed FeaturePython)
  n = 5
  ref = H_element
FEATURE [App::DocumentObjectGroupPython] C_element138  label="C_element : 083"  # scripted group (container) (typed FeaturePython)
  n = 5
  ref = C_element
FEATURE [App::DocumentObjectGroupPython] N_element057  label="N_element : 029"  # scripted group (container) (typed FeaturePython)
  n = 2
  ref = N_element
FEATURE [App::DocumentObjectGroupPython] O_element118  label="O_element : 071"  # scripted group (container) (typed FeaturePython)
  n = 2
  ref = O_element
FEATURE [App::DocumentObjectGroupPython] G4_DNA_THYMINE  # scripted group (container) (typed FeaturePython)
  Dunit = g/cm3
  Dvalue = 1
  Group = -> [H_element128,C_element138,N_element057,O_element118]
  conduct = 2
  density = 1
  expand = 3
  formula = G4_DNA_THYMINE
  name = G4_DNA_THYMINE
  specific = 4
FEATURE [App::DocumentObjectGroupPython] H_element129  label="H_element : 076"  # scripted group (container) (typed FeaturePython)
  n = 3
  ref = H_element
FEATURE [App::DocumentObjectGroupPython] C_element139  label="C_element : 084"  # scripted group (container) (typed FeaturePython)
  n = 4
  ref = C_element
FEATURE [App::DocumentObjectGroupPython] N_element058  label="N_element : 030"  # scripted group (container) (typed FeaturePython)
  n = 2
  ref = N_element
FEATURE [App::DocumentObjectGroupPython] O_element119  label="O_element : 072"  # scripted group (container) (typed FeaturePython)
  n = 2
  ref = O_element
FEATURE [App::DocumentObjectGroupPython] G4_DNA_URACIL  # scripted group (container) (typed FeaturePython)
  Dunit = g/cm3
  Dvalue = 1
  Group = -> [H_element129,C_element139,N_element058,O_element119]
  conduct = 2
  density = 1
  expand = 3
  formula = G4_DNA_URACIL
  name = G4_DNA_URACIL
  specific = 4
FEATURE [App::DocumentObjectGroupPython] H_element130  label="H_element : 077"  # scripted group (container) (typed FeaturePython)
  n = 10
  ref = H_element
FEATURE [App::DocumentObjectGroupPython] C_element140  label="C_element : 085"  # scripted group (container) (typed FeaturePython)
  n = 10
  ref = C_element
FEATURE [App::DocumentObjectGroupPython] N_element059  label="N_element : 031"  # scripted group (container) (typed FeaturePython)
  n = 5
  ref = N_element
FEATURE [App::DocumentObjectGroupPython] O_element120  label="O_element : 073"  # scripted group (container) (typed FeaturePython)
  n = 4
  ref = O_element
FEATURE [App::DocumentObjectGroupPython] G4_DNA_ADENOSINE  # scripted group (container) (typed FeaturePython)
  Dunit = g/cm3
  Dvalue = 1
  Group = -> [H_element130,C_element140,N_element059,O_element120]
  conduct = 2
  density = 1
  expand = 3
  formula = G4_DNA_ADENOSINE
  name = G4_DNA_ADENOSINE
  specific = 4
FEATURE [App::DocumentObjectGroupPython] H_element131  label="H_element : 078"  # scripted group (container) (typed FeaturePython)
  n = 10
  ref = H_element
FEATURE [App::DocumentObjectGroupPython] C_element141  label="C_element : 086"  # scripted group (container) (typed FeaturePython)
  n = 10
  ref = C_element
FEATURE [App::DocumentObjectGroupPython] N_element060  label="N_element : 032"  # scripted group (container) (typed FeaturePython)
  n = 5
  ref = N_element
FEATURE [App::DocumentObjectGroupPython] O_element121  label="O_element : 074"  # scripted group (container) (typed FeaturePython)
  n = 5
  ref = O_element
FEATURE [App::DocumentObjectGroupPython] G4_DNA_GUANOSINE  # scripted group (container) (typed FeaturePython)
  Dunit = g/cm3
  Dvalue = 1
  Group = -> [H_element131,C_element141,N_element060,O_element121]
  conduct = 2
  density = 1
  expand = 3
  formula = G4_DNA_GUANOSINE
  name = G4_DNA_GUANOSINE
  specific = 4
FEATURE [App::DocumentObjectGroupPython] H_element132  label="H_element : 079"  # scripted group (container) (typed FeaturePython)
  n = 10
  ref = H_element
FEATURE [App::DocumentObjectGroupPython] C_element142  label="C_element : 087"  # scripted group (container) (typed FeaturePython)
  n = 9
  ref = C_element
FEATURE [App::DocumentObjectGroupPython] N_element061  label="N_element : 033"  # scripted group (container) (typed FeaturePython)
  n = 3
  ref = N_element
FEATURE [App::DocumentObjectGroupPython] O_element122  label="O_element : 075"  # scripted group (container) (typed FeaturePython)
  n = 5
  ref = O_element
FEATURE [App::DocumentObjectGroupPython] G4_DNA_CYTIDINE  # scripted group (container) (typed FeaturePython)
  Dunit = g/cm3
  Dvalue = 1
  Group = -> [H_element132,C_element142,N_element061,O_element122]
  conduct = 2
  density = 1
  expand = 3
  formula = G4_DNA_CYTIDINE
  name = G4_DNA_CYTIDINE
  specific = 4
FEATURE [App::DocumentObjectGroupPython] H_element133  label="H_element : 080"  # scripted group (container) (typed FeaturePython)
  n = 9
  ref = H_element
FEATURE [App::DocumentObjectGroupPython] C_element143  label="C_element : 088"  # scripted group (container) (typed FeaturePython)
  n = 9
  ref = C_element
FEATURE [App::DocumentObjectGroupPython] N_element062  label="N_element : 034"  # scripted group (container) (typed FeaturePython)
  n = 2
  ref = N_element
FEATURE [App::DocumentObjectGroupPython] O_element123  label="O_element : 076"  # scripted group (container) (typed FeaturePython)
  n = 6
  ref = O_element
FEATURE [App::DocumentObjectGroupPython] G4_DNA_URIDINE  # scripted group (container) (typed FeaturePython)
  Dunit = g/cm3
  Dvalue = 1
  Group = -> [H_element133,C_element143,N_element062,O_element123]
  conduct = 2
  density = 1
  expand = 3
  formula = G4_DNA_URIDINE
  name = G4_DNA_URIDINE
  specific = 4
FEATURE [App::DocumentObjectGroupPython] H_element134  label="H_element : 081"  # scripted group (container) (typed FeaturePython)
  n = 11
  ref = H_element
FEATURE [App::DocumentObjectGroupPython] C_element144  label="C_element : 089"  # scripted group (container) (typed FeaturePython)
  n = 10
  ref = C_element
FEATURE [App::DocumentObjectGroupPython] N_element063  label="N_element : 035"  # scripted group (container) (typed FeaturePython)
  n = 2
  ref = N_element
FEATURE [App::DocumentObjectGroupPython] O_element124  label="O_element : 077"  # scripted group (container) (typed FeaturePython)
  n = 6
  ref = O_element
FEATURE [App::DocumentObjectGroupPython] G4_DNA_METHYLURIDINE  # scripted group (container) (typed FeaturePython)
  Dunit = g/cm3
  Dvalue = 1
  Group = -> [H_element134,C_element144,N_element063,O_element124]
  conduct = 2
  density = 1
  expand = 3
  formula = G4_DNA_METHYLURIDINE
  name = G4_DNA_METHYLURIDINE
  specific = 4
FEATURE [App::DocumentObjectGroupPython] P_element014  label="P_element : 003"  # scripted group (container) (typed FeaturePython)
  n = 1
  ref = P_element
FEATURE [App::DocumentObjectGroupPython] O_element125  label="O_element : 078"  # scripted group (container) (typed FeaturePython)
  n = 3
  ref = O_element
FEATURE [App::DocumentObjectGroupPython] G4_DNA_MONOPHOSPHATE  # scripted group (container) (typed FeaturePython)
  Dunit = g/cm3
  Dvalue = 1
  Group = -> [P_element014,O_element125]
  conduct = 2
  density = 1
  expand = 3
  formula = G4_DNA_MONOPHOSPHATE
  name = G4_DNA_MONOPHOSPHATE
  specific = 4
FEATURE [App::DocumentObjectGroupPython] H_element135  label="H_element : 082"  # scripted group (container) (typed FeaturePython)
  n = 10
  ref = H_element
FEATURE [App::DocumentObjectGroupPython] C_element145  label="C_element : 090"  # scripted group (container) (typed FeaturePython)
  n = 10
  ref = C_element
FEATURE [App::DocumentObjectGroupPython] N_element064  label="N_element : 036"  # scripted group (container) (typed FeaturePython)
  n = 5
  ref = N_element
FEATURE [App::DocumentObjectGroupPython] O_element126  label="O_element : 079"  # scripted group (container) (typed FeaturePython)
  n = 7
  ref = O_element
FEATURE [App::DocumentObjectGroupPython] P_element015  label="P_element : 004"  # scripted group (container) (typed FeaturePython)
  n = 1
  ref = P_element
FEATURE [App::DocumentObjectGroupPython] G4_DNA_A  # scripted group (container) (typed FeaturePython)
  Dunit = g/cm3
  Dvalue = 1
  Group = -> [H_element135,C_element145,N_element064,O_element126,P_element015]
  conduct = 2
  density = 1
  expand = 3
  formula = G4_DNA_A
  name = G4_DNA_A
  specific = 4
FEATURE [App::DocumentObjectGroupPython] H_element136  label="H_element : 083"  # scripted group (container) (typed FeaturePython)
  n = 10
  ref = H_element
FEATURE [App::DocumentObjectGroupPython] C_element146  label="C_element : 091"  # scripted group (container) (typed FeaturePython)
  n = 10
  ref = C_element
FEATURE [App::DocumentObjectGroupPython] N_element065  label="N_element : 037"  # scripted group (container) (typed FeaturePython)
  n = 5
  ref = N_element
FEATURE [App::DocumentObjectGroupPython] O_element127  label="O_element : 8"  # scripted group (container) (typed FeaturePython)
  n = 8
  ref = O_element
FEATURE [App::DocumentObjectGroupPython] P_element016  label="P_element : 005"  # scripted group (container) (typed FeaturePython)
  n = 1
  ref = P_element
FEATURE [App::DocumentObjectGroupPython] G4_DNA_G  # scripted group (container) (typed FeaturePython)
  Dunit = g/cm3
  Dvalue = 1
  Group = -> [H_element136,C_element146,N_element065,O_element127,P_element016]
  conduct = 2
  density = 1
  expand = 3
  formula = G4_DNA_G
  name = G4_DNA_G
  specific = 4
FEATURE [App::DocumentObjectGroupPython] H_element137  label="H_element : 084"  # scripted group (container) (typed FeaturePython)
  n = 10
  ref = H_element
FEATURE [App::DocumentObjectGroupPython] C_element147  label="C_element : 092"  # scripted group (container) (typed FeaturePython)
  n = 9
  ref = C_element
FEATURE [App::DocumentObjectGroupPython] N_element066  label="N_element : 038"  # scripted group (container) (typed FeaturePython)
  n = 3
  ref = N_element
FEATURE [App::DocumentObjectGroupPython] O_element128  label="O_element : 080"  # scripted group (container) (typed FeaturePython)
  n = 8
  ref = O_element
FEATURE [App::DocumentObjectGroupPython] P_element017  label="P_element : 006"  # scripted group (container) (typed FeaturePython)
  n = 1
  ref = P_element
FEATURE [App::DocumentObjectGroupPython] G4_DNA_C  # scripted group (container) (typed FeaturePython)
  Dunit = g/cm3
  Dvalue = 1
  Group = -> [H_element137,C_element147,N_element066,O_element128,P_element017]
  conduct = 2
  density = 1
  expand = 3
  formula = G4_DNA_C
  name = G4_DNA_C
  specific = 4
FEATURE [App::DocumentObjectGroupPython] H_element138  label="H_element : 085"  # scripted group (container) (typed FeaturePython)
  n = 9
  ref = H_element
FEATURE [App::DocumentObjectGroupPython] C_element148  label="C_element : 093"  # scripted group (container) (typed FeaturePython)
  n = 9
  ref = C_element
FEATURE [App::DocumentObjectGroupPython] N_element067  label="N_element : 039"  # scripted group (container) (typed FeaturePython)
  n = 2
  ref = N_element
FEATURE [App::DocumentObjectGroupPython] O_element129  label="O_element : 9"  # scripted group (container) (typed FeaturePython)
  n = 9
  ref = O_element
FEATURE [App::DocumentObjectGroupPython] P_element018  label="P_element : 007"  # scripted group (container) (typed FeaturePython)
  n = 1
  ref = P_element
FEATURE [App::DocumentObjectGroupPython] G4_DNA_U  # scripted group (container) (typed FeaturePython)
  Dunit = g/cm3
  Dvalue = 1
  Group = -> [H_element138,C_element148,N_element067,O_element129,P_element018]
  conduct = 2
  density = 1
  expand = 3
  formula = G4_DNA_U
  name = G4_DNA_U
  specific = 4
FEATURE [App::DocumentObjectGroupPython] H_element139  label="H_element : 086"  # scripted group (container) (typed FeaturePython)
  n = 11
  ref = H_element
FEATURE [App::DocumentObjectGroupPython] C_element149  label="C_element : 094"  # scripted group (container) (typed FeaturePython)
  n = 10
  ref = C_element
FEATURE [App::DocumentObjectGroupPython] N_element068  label="N_element : 040"  # scripted group (container) (typed FeaturePython)
  n = 2
  ref = N_element
FEATURE [App::DocumentObjectGroupPython] O_element130  label="O_element : 081"  # scripted group (container) (typed FeaturePython)
  n = 9
  ref = O_element
FEATURE [App::DocumentObjectGroupPython] P_element019  label="P_element : 008"  # scripted group (container) (typed FeaturePython)
  n = 1
  ref = P_element
FEATURE [App::DocumentObjectGroupPython] G4_DNA_MU  # scripted group (container) (typed FeaturePython)
  Dunit = g/cm3
  Dvalue = 1
  Group = -> [H_element139,C_element149,N_element068,O_element130,P_element019]
  conduct = 2
  density = 1
  expand = 3
  formula = G4_DNA_MU
  name = G4_DNA_MU
  specific = 4
FEATURE [App::DocumentObjectGroupPython] BioChemical  # scripted group (container) (typed FeaturePython)
  Group = -> [G4_CYTOSINE,G4_THYMINE,G4_URACIL,G4_DNA_ADENINE,G4_DNA_GUANINE,G4_DNA_CYTOSINE,G4_DNA_THYMINE,G4_DNA_URACIL,G4_DNA_ADENOSINE,G4_DNA_GUANOSINE,G4_DNA_CYTIDINE,G4_DNA_URIDINE,G4_DNA_METHYLURIDINE,G4_DNA_MONOPHOSPHATE,G4_DNA_A,G4_DNA_G,G4_DNA_C,G4_DNA_U,G4_DNA_MU]
FEATURE [App::DocumentObjectGroupPython] G4Materials  # scripted group (container) (typed FeaturePython)
  Group = -> [NIST,Element,HEP,Space,BioChemical]
  version = 1
FEATURE [App::DocumentObjectGroupPython] Geant4  # scripted group (container) (typed FeaturePython)
  Group = -> [G4Isotopes,G4Elements,G4Materials]
FEATURE [App::DocumentObjectGroupPython] Materials  # scripted group (container) (typed FeaturePython)
  Group = -> [Geant4]
FEATURE [Part::FeaturePython] GDMLBox_WorldBox  # WARN: FeaturePython — macro-defined, semantics opaque (R4)
  lunit = 2
  material = 5
  x = 200.2
  y = 130
  z = 130
FEATURE [Part::FeaturePython] GDMLBox_Box  # WARN: FeaturePython — macro-defined, semantics opaque (R4)
  Placement = pos=(30,0,0) rot=(0,0,1;0rad)
  lunit = 2
  material = 0
  x = 10
  y = 10
  z = 10
FEATURE [Part::FeaturePython] GDMLTorus  # WARN: FeaturePython — macro-defined, semantics opaque (R4)
  Placement = pos=(30,0,0) rot=(0,1,0;1.5708rad)
  aunit = deg
  deltaphi = 360
  lunit = 2
  material = 0
  rmax = 2
  rmin = 0
  rtor = 8
  startphi = 0
FEATURE [Part::MultiFuse] Fusion
  Shapes = -> [GDMLBox_Box,GDMLTorus]
FEATURE [Part::FeaturePython] Array  # Draft array (typed FeaturePython)
  AlwaysSyncPlacement = false
  Angle = 180
  ArrayType = 1
  Axis = (0,0,1)
  Base = -> Fusion
  Center = (0,0,0)
  Count = 5
  ExpandArray = false
  Fuse = false
  IntervalAxis = (0,0,0)
  IntervalX = (50,0,0)
  IntervalY = (0,50,0)
  IntervalZ = (0,0,50)
  NumberCircles = 3
  NumberPolar = 5
  NumberX = 2
  NumberY = 2
  NumberZ = 1
  Placement = pos=(0,0,0) rot=(0,0,1;0.785398rad)
  PlacementList = 5 placements: [(0,0,0),(0,0,0),(0,0,0),(0,0,0),(0,0,0)]
  RadialDistance = 50
  ScaleList = (5) [(1,1,1),(1,1,1),(1,1,1),(1,1,1),(1,1,1)]
  Symmetry = 1
  TangentialDistance = 25
FEATURE [App::Part] Part001
  Group = -> [Array]
  Origin = -> Origin004
FEATURE [App::Part] worldVOL
  Group = -> [GDMLBox_WorldBox,Part001]
  Origin = -> Origin
